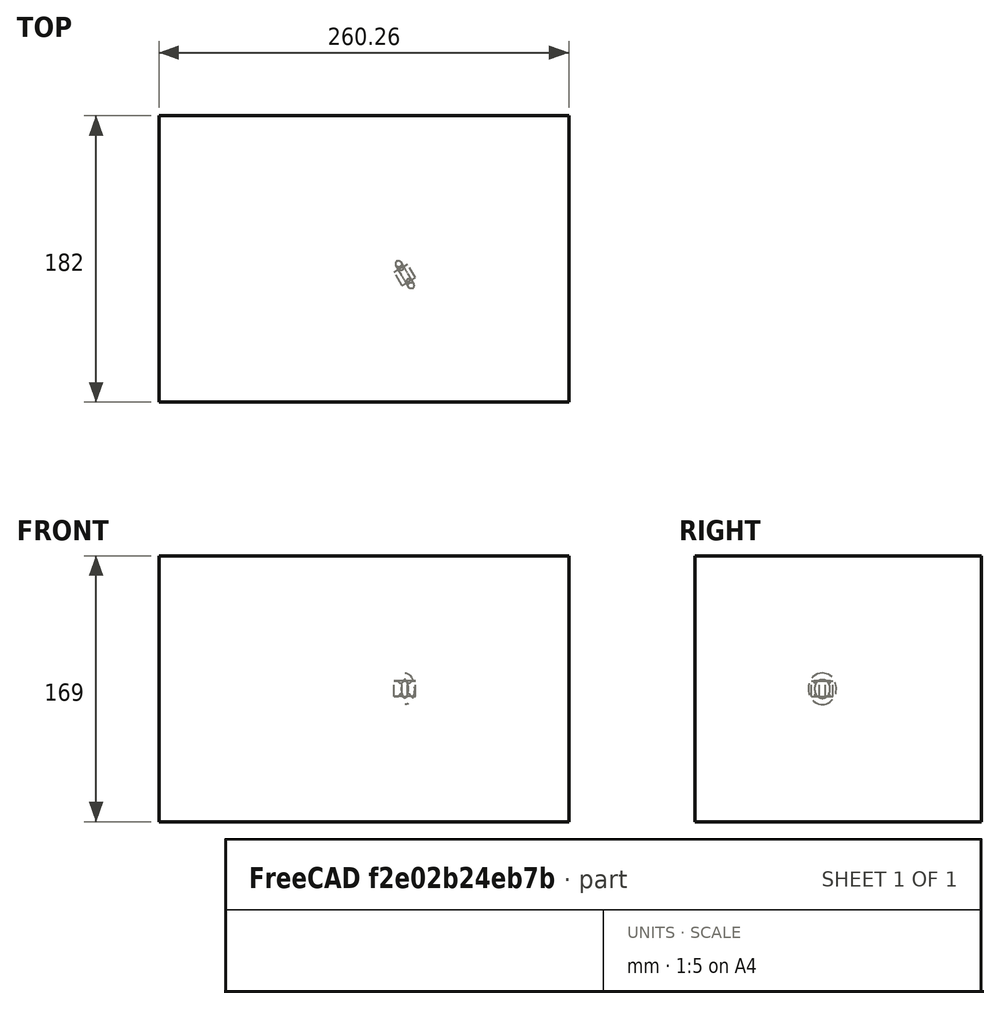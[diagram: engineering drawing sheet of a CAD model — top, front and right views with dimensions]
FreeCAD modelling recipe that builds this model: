
FCSTD DOCUMENT  (FreeCAD 1.0R39109 (Git))
Label: polarArray-7-Base-rotated-translated
License: All rights reserved
objects: App::DocumentObjectGroupPython×1251, Part::FeaturePython×4, App::Part×2, Part::MultiFuse×1
note: 4 computed .brp shape members not serialized (recipe doc carries the construction recipe); baked Part::Feature solids carry a one-line shape summary decoded from their .brp

FEATURE [App::DocumentObjectGroupPython] HALFPI  # scripted group (container) (typed FeaturePython)
  name = HALFPI
  value = pi/2.
FEATURE [App::DocumentObjectGroupPython] PI  # scripted group (container) (typed FeaturePython)
  name = PI
  value = 1.*pi
FEATURE [App::DocumentObjectGroupPython] TWOPI  # scripted group (container) (typed FeaturePython)
  name = TWOPI
  value = 2.*pi
FEATURE [App::DocumentObjectGroupPython] Constants  # scripted group (container) (typed FeaturePython)
  Group = -> [HALFPI,PI,TWOPI]
FEATURE [App::DocumentObjectGroupPython] Variables  # scripted group (container) (typed FeaturePython)
FEATURE [App::DocumentObjectGroupPython] Quantities  # scripted group (container) (typed FeaturePython)
FEATURE [App::DocumentObjectGroupPython] Isotopes  # scripted group (container) (typed FeaturePython)
FEATURE [App::DocumentObjectGroupPython] Elements  # scripted group (container) (typed FeaturePython)
FEATURE [App::DocumentObjectGroupPython] Matrix  # scripted group (container) (typed FeaturePython)
FEATURE [App::DocumentObjectGroupPython] Surfaces  # scripted group (container) (typed FeaturePython)
FEATURE [App::DocumentObjectGroupPython] Opticals  # scripted group (container) (typed FeaturePython)
  Group = -> [Matrix,Surfaces]
FEATURE [App::DocumentObjectGroupPython] G4Isotopes  # scripted group (container) (typed FeaturePython)
FEATURE [App::DocumentObjectGroupPython] H_element  # scripted group (container) (typed FeaturePython)
  Z = 1
  atom_value = 1.008
  formula = H
  name = H_element
FEATURE [App::DocumentObjectGroupPython] He_element  # scripted group (container) (typed FeaturePython)
  Z = 2
  atom_value = 4.0026
  formula = He
  name = He_element
FEATURE [App::DocumentObjectGroupPython] Li_element  # scripted group (container) (typed FeaturePython)
  Z = 3
  atom_value = 6.94
  formula = Li
  name = Li_element
FEATURE [App::DocumentObjectGroupPython] Be_element  # scripted group (container) (typed FeaturePython)
  Z = 4
  atom_value = 9.01218
  formula = Be
  name = Be_element
FEATURE [App::DocumentObjectGroupPython] B_element  # scripted group (container) (typed FeaturePython)
  Z = 5
  atom_value = 10.81
  formula = B
  name = B_element
FEATURE [App::DocumentObjectGroupPython] C_element  # scripted group (container) (typed FeaturePython)
  Z = 6
  atom_value = 12.011
  formula = C
  name = C_element
FEATURE [App::DocumentObjectGroupPython] N_element  # scripted group (container) (typed FeaturePython)
  Z = 7
  atom_value = 14.007
  formula = N
  name = N_element
FEATURE [App::DocumentObjectGroupPython] O_element  # scripted group (container) (typed FeaturePython)
  Z = 8
  atom_value = 15.999
  formula = O
  name = O_element
FEATURE [App::DocumentObjectGroupPython] F_element  # scripted group (container) (typed FeaturePython)
  Z = 9
  atom_value = 18.9984
  formula = F
  name = F_element
FEATURE [App::DocumentObjectGroupPython] Ne_element  # scripted group (container) (typed FeaturePython)
  Z = 10
  atom_value = 20.1797
  formula = Ne
  name = Ne_element
FEATURE [App::DocumentObjectGroupPython] Na_element  # scripted group (container) (typed FeaturePython)
  Z = 11
  atom_value = 22.9898
  formula = Na
  name = Na_element
FEATURE [App::DocumentObjectGroupPython] Mg_element  # scripted group (container) (typed FeaturePython)
  Z = 12
  atom_value = 24.305
  formula = Mg
  name = Mg_element
FEATURE [App::DocumentObjectGroupPython] Al_element  # scripted group (container) (typed FeaturePython)
  Z = 13
  atom_value = 26.9815
  formula = Al
  name = Al_element
FEATURE [App::DocumentObjectGroupPython] Si_element  # scripted group (container) (typed FeaturePython)
  Z = 14
  atom_value = 28.085
  formula = Si
  name = Si_element
FEATURE [App::DocumentObjectGroupPython] P_element  # scripted group (container) (typed FeaturePython)
  Z = 15
  atom_value = 30.9738
  formula = P
  name = P_element
FEATURE [App::DocumentObjectGroupPython] S_element  # scripted group (container) (typed FeaturePython)
  Z = 16
  atom_value = 32.06
  formula = S
  name = S_element
FEATURE [App::DocumentObjectGroupPython] Cl_element  # scripted group (container) (typed FeaturePython)
  Z = 17
  atom_value = 35.45
  formula = Cl
  name = Cl_element
FEATURE [App::DocumentObjectGroupPython] Ar_element  # scripted group (container) (typed FeaturePython)
  Z = 18
  atom_value = 39.95
  formula = Ar
  name = Ar_element
FEATURE [App::DocumentObjectGroupPython] K_element  # scripted group (container) (typed FeaturePython)
  Z = 19
  atom_value = 39.0983
  formula = K
  name = K_element
FEATURE [App::DocumentObjectGroupPython] Ca_element  # scripted group (container) (typed FeaturePython)
  Z = 20
  atom_value = 40.078
  formula = Ca
  name = Ca_element
FEATURE [App::DocumentObjectGroupPython] Sc_element  # scripted group (container) (typed FeaturePython)
  Z = 21
  atom_value = 44.9559
  formula = Sc
  name = Sc_element
FEATURE [App::DocumentObjectGroupPython] Ti_element  # scripted group (container) (typed FeaturePython)
  Z = 22
  atom_value = 47.867
  formula = Ti
  name = Ti_element
FEATURE [App::DocumentObjectGroupPython] V_element  # scripted group (container) (typed FeaturePython)
  Z = 23
  atom_value = 50.9415
  formula = V
  name = V_element
FEATURE [App::DocumentObjectGroupPython] Cr_element  # scripted group (container) (typed FeaturePython)
  Z = 24
  atom_value = 51.9961
  formula = Cr
  name = Cr_element
FEATURE [App::DocumentObjectGroupPython] Mn_element  # scripted group (container) (typed FeaturePython)
  Z = 25
  atom_value = 54.938
  formula = Mn
  name = Mn_element
FEATURE [App::DocumentObjectGroupPython] Fe_element  # scripted group (container) (typed FeaturePython)
  Z = 26
  atom_value = 55.845
  formula = Fe
  name = Fe_element
FEATURE [App::DocumentObjectGroupPython] Co_element  # scripted group (container) (typed FeaturePython)
  Z = 27
  atom_value = 58.9332
  formula = Co
  name = Co_element
FEATURE [App::DocumentObjectGroupPython] Ni_element  # scripted group (container) (typed FeaturePython)
  Z = 28
  atom_value = 58.6934
  formula = Ni
  name = Ni_element
FEATURE [App::DocumentObjectGroupPython] Cu_element  # scripted group (container) (typed FeaturePython)
  Z = 29
  atom_value = 63.546
  formula = Cu
  name = Cu_element
FEATURE [App::DocumentObjectGroupPython] Zn_element  # scripted group (container) (typed FeaturePython)
  Z = 30
  atom_value = 65.38
  formula = Zn
  name = Zn_element
FEATURE [App::DocumentObjectGroupPython] Ga_element  # scripted group (container) (typed FeaturePython)
  Z = 31
  atom_value = 69.723
  formula = Ga
  name = Ga_element
FEATURE [App::DocumentObjectGroupPython] Ge_element  # scripted group (container) (typed FeaturePython)
  Z = 32
  atom_value = 72.63
  formula = Ge
  name = Ge_element
FEATURE [App::DocumentObjectGroupPython] As_element  # scripted group (container) (typed FeaturePython)
  Z = 33
  atom_value = 74.9216
  formula = As
  name = As_element
FEATURE [App::DocumentObjectGroupPython] Se_element  # scripted group (container) (typed FeaturePython)
  Z = 34
  atom_value = 78.971
  formula = Se
  name = Se_element
FEATURE [App::DocumentObjectGroupPython] Br_element  # scripted group (container) (typed FeaturePython)
  Z = 35
  atom_value = 79.904
  formula = Br
  name = Br_element
FEATURE [App::DocumentObjectGroupPython] Kr_element  # scripted group (container) (typed FeaturePython)
  Z = 36
  atom_value = 83.798
  formula = Kr
  name = Kr_element
FEATURE [App::DocumentObjectGroupPython] Rb_element  # scripted group (container) (typed FeaturePython)
  Z = 37
  atom_value = 85.4678
  formula = Rb
  name = Rb_element
FEATURE [App::DocumentObjectGroupPython] Sr_element  # scripted group (container) (typed FeaturePython)
  Z = 38
  atom_value = 87.62
  formula = Sr
  name = Sr_element
FEATURE [App::DocumentObjectGroupPython] Y_element  # scripted group (container) (typed FeaturePython)
  Z = 39
  atom_value = 88.9058
  formula = Y
  name = Y_element
FEATURE [App::DocumentObjectGroupPython] Zr_element  # scripted group (container) (typed FeaturePython)
  Z = 40
  atom_value = 91.224
  formula = Zr
  name = Zr_element
FEATURE [App::DocumentObjectGroupPython] Nb_element  # scripted group (container) (typed FeaturePython)
  Z = 41
  atom_value = 92.9064
  formula = Nb
  name = Nb_element
FEATURE [App::DocumentObjectGroupPython] Mo_element  # scripted group (container) (typed FeaturePython)
  Z = 42
  atom_value = 95.95
  formula = Mo
  name = Mo_element
FEATURE [App::DocumentObjectGroupPython] Tc_element  # scripted group (container) (typed FeaturePython)
  Z = 43
  atom_value = 97
  formula = Tc
  name = Tc_element
FEATURE [App::DocumentObjectGroupPython] Ru_element  # scripted group (container) (typed FeaturePython)
  Z = 44
  atom_value = 101.07
  formula = Ru
  name = Ru_element
FEATURE [App::DocumentObjectGroupPython] Rh_element  # scripted group (container) (typed FeaturePython)
  Z = 45
  atom_value = 102.905
  formula = Rh
  name = Rh_element
FEATURE [App::DocumentObjectGroupPython] Pd_element  # scripted group (container) (typed FeaturePython)
  Z = 46
  atom_value = 106.42
  formula = Pd
  name = Pd_element
FEATURE [App::DocumentObjectGroupPython] Ag_element  # scripted group (container) (typed FeaturePython)
  Z = 47
  atom_value = 107.868
  formula = Ag
  name = Ag_element
FEATURE [App::DocumentObjectGroupPython] Cd_element  # scripted group (container) (typed FeaturePython)
  Z = 48
  atom_value = 112.414
  formula = Cd
  name = Cd_element
FEATURE [App::DocumentObjectGroupPython] In_element  # scripted group (container) (typed FeaturePython)
  Z = 49
  atom_value = 114.818
  formula = In
  name = In_element
FEATURE [App::DocumentObjectGroupPython] Sn_element  # scripted group (container) (typed FeaturePython)
  Z = 50
  atom_value = 118.71
  formula = Sn
  name = Sn_element
FEATURE [App::DocumentObjectGroupPython] Sb_element  # scripted group (container) (typed FeaturePython)
  Z = 51
  atom_value = 121.76
  formula = Sb
  name = Sb_element
FEATURE [App::DocumentObjectGroupPython] Te_element  # scripted group (container) (typed FeaturePython)
  Z = 52
  atom_value = 127.6
  formula = Te
  name = Te_element
FEATURE [App::DocumentObjectGroupPython] I_element  # scripted group (container) (typed FeaturePython)
  Z = 53
  atom_value = 126.904
  formula = I
  name = I_element
FEATURE [App::DocumentObjectGroupPython] Xe_element  # scripted group (container) (typed FeaturePython)
  Z = 54
  atom_value = 131.293
  formula = Xe
  name = Xe_element
FEATURE [App::DocumentObjectGroupPython] Cs_element  # scripted group (container) (typed FeaturePython)
  Z = 55
  atom_value = 132.905
  formula = Cs
  name = Cs_element
FEATURE [App::DocumentObjectGroupPython] Ba_element  # scripted group (container) (typed FeaturePython)
  Z = 56
  atom_value = 137.327
  formula = Ba
  name = Ba_element
FEATURE [App::DocumentObjectGroupPython] La_element  # scripted group (container) (typed FeaturePython)
  Z = 57
  atom_value = 138.905
  formula = La
  name = La_element
FEATURE [App::DocumentObjectGroupPython] Ce_element  # scripted group (container) (typed FeaturePython)
  Z = 58
  atom_value = 140.116
  formula = Ce
  name = Ce_element
FEATURE [App::DocumentObjectGroupPython] Pr_element  # scripted group (container) (typed FeaturePython)
  Z = 59
  atom_value = 140.908
  formula = Pr
  name = Pr_element
FEATURE [App::DocumentObjectGroupPython] Nd_element  # scripted group (container) (typed FeaturePython)
  Z = 60
  atom_value = 144.242
  formula = Nd
  name = Nd_element
FEATURE [App::DocumentObjectGroupPython] Pm_element  # scripted group (container) (typed FeaturePython)
  Z = 61
  atom_value = 145
  formula = Pm
  name = Pm_element
FEATURE [App::DocumentObjectGroupPython] Sm_element  # scripted group (container) (typed FeaturePython)
  Z = 62
  atom_value = 150.36
  formula = Sm
  name = Sm_element
FEATURE [App::DocumentObjectGroupPython] Eu_element  # scripted group (container) (typed FeaturePython)
  Z = 63
  atom_value = 151.964
  formula = Eu
  name = Eu_element
FEATURE [App::DocumentObjectGroupPython] Gd_element  # scripted group (container) (typed FeaturePython)
  Z = 64
  atom_value = 157.25
  formula = Gd
  name = Gd_element
FEATURE [App::DocumentObjectGroupPython] Tb_element  # scripted group (container) (typed FeaturePython)
  Z = 65
  atom_value = 158.925
  formula = Tb
  name = Tb_element
FEATURE [App::DocumentObjectGroupPython] Dy_element  # scripted group (container) (typed FeaturePython)
  Z = 66
  atom_value = 162.5
  formula = Dy
  name = Dy_element
FEATURE [App::DocumentObjectGroupPython] Ho_element  # scripted group (container) (typed FeaturePython)
  Z = 67
  atom_value = 164.93
  formula = Ho
  name = Ho_element
FEATURE [App::DocumentObjectGroupPython] Er_element  # scripted group (container) (typed FeaturePython)
  Z = 68
  atom_value = 167.259
  formula = Er
  name = Er_element
FEATURE [App::DocumentObjectGroupPython] Tm_element  # scripted group (container) (typed FeaturePython)
  Z = 69
  atom_value = 168.934
  formula = Tm
  name = Tm_element
FEATURE [App::DocumentObjectGroupPython] Yb_element  # scripted group (container) (typed FeaturePython)
  Z = 70
  atom_value = 173.045
  formula = Yb
  name = Yb_element
FEATURE [App::DocumentObjectGroupPython] Lu_element  # scripted group (container) (typed FeaturePython)
  Z = 71
  atom_value = 174.967
  formula = Lu
  name = Lu_element
FEATURE [App::DocumentObjectGroupPython] Hf_element  # scripted group (container) (typed FeaturePython)
  Z = 72
  atom_value = 178.49
  formula = Hf
  name = Hf_element
FEATURE [App::DocumentObjectGroupPython] Ta_element  # scripted group (container) (typed FeaturePython)
  Z = 73
  atom_value = 180.948
  formula = Ta
  name = Ta_element
FEATURE [App::DocumentObjectGroupPython] W_element  # scripted group (container) (typed FeaturePython)
  Z = 74
  atom_value = 183.84
  formula = W
  name = W_element
FEATURE [App::DocumentObjectGroupPython] Re_element  # scripted group (container) (typed FeaturePython)
  Z = 75
  atom_value = 186.207
  formula = Re
  name = Re_element
FEATURE [App::DocumentObjectGroupPython] Os_element  # scripted group (container) (typed FeaturePython)
  Z = 76
  atom_value = 190.23
  formula = Os
  name = Os_element
FEATURE [App::DocumentObjectGroupPython] Ir_element  # scripted group (container) (typed FeaturePython)
  Z = 77
  atom_value = 192.217
  formula = Ir
  name = Ir_element
FEATURE [App::DocumentObjectGroupPython] Pt_element  # scripted group (container) (typed FeaturePython)
  Z = 78
  atom_value = 195.084
  formula = Pt
  name = Pt_element
FEATURE [App::DocumentObjectGroupPython] Au_element  # scripted group (container) (typed FeaturePython)
  Z = 79
  atom_value = 196.967
  formula = Au
  name = Au_element
FEATURE [App::DocumentObjectGroupPython] Hg_element  # scripted group (container) (typed FeaturePython)
  Z = 80
  atom_value = 200.592
  formula = Hg
  name = Hg_element
FEATURE [App::DocumentObjectGroupPython] Tl_element  # scripted group (container) (typed FeaturePython)
  Z = 81
  atom_value = 204.38
  formula = Tl
  name = Tl_element
FEATURE [App::DocumentObjectGroupPython] Pb_element  # scripted group (container) (typed FeaturePython)
  Z = 82
  atom_value = 207.2
  formula = Pb
  name = Pb_element
FEATURE [App::DocumentObjectGroupPython] Bi_element  # scripted group (container) (typed FeaturePython)
  Z = 83
  atom_value = 208.98
  formula = Bi
  name = Bi_element
FEATURE [App::DocumentObjectGroupPython] Po_element  # scripted group (container) (typed FeaturePython)
  Z = 84
  atom_value = 209
  formula = Po
  name = Po_element
FEATURE [App::DocumentObjectGroupPython] At_element  # scripted group (container) (typed FeaturePython)
  Z = 85
  atom_value = 210
  formula = At
  name = At_element
FEATURE [App::DocumentObjectGroupPython] Rn_element  # scripted group (container) (typed FeaturePython)
  Z = 86
  atom_value = 222
  formula = Rn
  name = Rn_element
FEATURE [App::DocumentObjectGroupPython] Fr_element  # scripted group (container) (typed FeaturePython)
  Z = 87
  atom_value = 223
  formula = Fr
  name = Fr_element
FEATURE [App::DocumentObjectGroupPython] Ra_element  # scripted group (container) (typed FeaturePython)
  Z = 88
  atom_value = 226
  formula = Ra
  name = Ra_element
FEATURE [App::DocumentObjectGroupPython] Ac_element  # scripted group (container) (typed FeaturePython)
  Z = 89
  atom_value = 227
  formula = Ac
  name = Ac_element
FEATURE [App::DocumentObjectGroupPython] Th_element  # scripted group (container) (typed FeaturePython)
  Z = 90
  atom_value = 232.038
  formula = Th
  name = Th_element
FEATURE [App::DocumentObjectGroupPython] Pa_element  # scripted group (container) (typed FeaturePython)
  Z = 91
  atom_value = 231.036
  formula = Pa
  name = Pa_element
FEATURE [App::DocumentObjectGroupPython] U_element  # scripted group (container) (typed FeaturePython)
  Z = 92
  atom_value = 238.029
  formula = U
  name = U_element
FEATURE [App::DocumentObjectGroupPython] Np_element  # scripted group (container) (typed FeaturePython)
  Z = 93
  atom_value = 237
  formula = Np
  name = Np_element
FEATURE [App::DocumentObjectGroupPython] Pu_element  # scripted group (container) (typed FeaturePython)
  Z = 94
  atom_value = 244
  formula = Pu
  name = Pu_element
FEATURE [App::DocumentObjectGroupPython] Am_element  # scripted group (container) (typed FeaturePython)
  Z = 95
  atom_value = 243
  formula = Am
  name = Am_element
FEATURE [App::DocumentObjectGroupPython] Cm_element  # scripted group (container) (typed FeaturePython)
  Z = 96
  atom_value = 247
  formula = Cm
  name = Cm_element
FEATURE [App::DocumentObjectGroupPython] Bk_element  # scripted group (container) (typed FeaturePython)
  Z = 97
  atom_value = 247
  formula = Bk
  name = Bk_element
FEATURE [App::DocumentObjectGroupPython] Cf_element  # scripted group (container) (typed FeaturePython)
  Z = 98
  atom_value = 251
  formula = Cf
  name = Cf_element
FEATURE [App::DocumentObjectGroupPython] G4Elements  # scripted group (container) (typed FeaturePython)
  Group = -> [H_element,He_element,Li_element,Be_element,B_element,C_element,N_element,O_element,F_element,Ne_element,Na_element,Mg_element,Al_element,Si_element,P_element,S_element,Cl_element,Ar_element,K_element,Ca_element,Sc_element,Ti_element,V_element,Cr_element,Mn_element,Fe_element,Co_element,Ni_element,Cu_element,Zn_element,Ga_element,Ge_element,As_element,Se_element,Br_element,Kr_element,Rb_element,+61 more]
FEATURE [App::DocumentObjectGroupPython] H_element001  label="H_element : 0.101"  # scripted group (container) (typed FeaturePython)
  n = 0.101327
FEATURE [App::DocumentObjectGroupPython] C_element001  label="C_element : 0.775"  # scripted group (container) (typed FeaturePython)
  n = 0.7755
FEATURE [App::DocumentObjectGroupPython] N_element001  label="N_element : 0.035"  # scripted group (container) (typed FeaturePython)
  n = 0.035057
FEATURE [App::DocumentObjectGroupPython] O_element001  label="O_element : 0.052"  # scripted group (container) (typed FeaturePython)
  n = 0.0523159
FEATURE [App::DocumentObjectGroupPython] F_element001  label="F_element : 0.017"  # scripted group (container) (typed FeaturePython)
  n = 0.017422
FEATURE [App::DocumentObjectGroupPython] Ca_element001  label="Ca_element : 0.018"  # scripted group (container) (typed FeaturePython)
  n = 0.018378
FEATURE [App::DocumentObjectGroupPython] G4_A_150_TISSUE  label="G4_A-150_TISSUE"  # scripted group (container) (typed FeaturePython)
  Dunit = g/cm3
  Dvalue = 1.127
  Group = -> [H_element001,C_element001,N_element001,O_element001,F_element001,Ca_element001]
  conduct = 2
  density = 1
  expand = 3
  formula = G4_A-150_TISSUE
  name = G4_A-150_TISSUE
  specific = 4
FEATURE [App::DocumentObjectGroupPython] C_element002  label="C_element : 3"  # scripted group (container) (typed FeaturePython)
  n = 3
  ref = C_element
FEATURE [App::DocumentObjectGroupPython] H_element002  label="H_element : 6"  # scripted group (container) (typed FeaturePython)
  n = 6
  ref = H_element
FEATURE [App::DocumentObjectGroupPython] O_element002  label="O_element : 1"  # scripted group (container) (typed FeaturePython)
  n = 1
  ref = O_element
FEATURE [App::DocumentObjectGroupPython] G4_ACETONE  # scripted group (container) (typed FeaturePython)
  Dunit = g/cm3
  Dvalue = 0.7899
  Group = -> [C_element002,H_element002,O_element002]
  conduct = 2
  density = 1
  expand = 3
  formula = G4_ACETONE
  name = G4_ACETONE
  specific = 4
FEATURE [App::DocumentObjectGroupPython] C_element003  label="C_element : 2"  # scripted group (container) (typed FeaturePython)
  n = 2
  ref = C_element
FEATURE [App::DocumentObjectGroupPython] H_element003  label="H_element : 2"  # scripted group (container) (typed FeaturePython)
  n = 2
  ref = H_element
FEATURE [App::DocumentObjectGroupPython] G4_ACETYLENE  # scripted group (container) (typed FeaturePython)
  Dunit = g/cm3
  Dvalue = 0.0010967
  Group = -> [C_element003,H_element003]
  conduct = 2
  density = 1
  expand = 3
  formula = G4_ACETYLENE
  name = G4_ACETYLENE
  specific = 4
FEATURE [App::DocumentObjectGroupPython] C_element004  label="C_element : 5"  # scripted group (container) (typed FeaturePython)
  n = 5
  ref = C_element
FEATURE [App::DocumentObjectGroupPython] H_element004  label="H_element : 5"  # scripted group (container) (typed FeaturePython)
  n = 5
  ref = H_element
FEATURE [App::DocumentObjectGroupPython] N_element002  label="N_element : 5"  # scripted group (container) (typed FeaturePython)
  n = 5
  ref = N_element
FEATURE [App::DocumentObjectGroupPython] G4_ADENINE  # scripted group (container) (typed FeaturePython)
  Dunit = g/cm3
  Dvalue = 1.6
  Group = -> [C_element004,H_element004,N_element002]
  conduct = 2
  density = 1
  expand = 3
  formula = G4_ADENINE
  name = G4_ADENINE
  specific = 4
FEATURE [App::DocumentObjectGroupPython] H_element005  label="H_element : 0.114"  # scripted group (container) (typed FeaturePython)
  n = 0.114
FEATURE [App::DocumentObjectGroupPython] C_element005  label="C_element : 0.598"  # scripted group (container) (typed FeaturePython)
  n = 0.598
FEATURE [App::DocumentObjectGroupPython] N_element003  label="N_element : 0.007"  # scripted group (container) (typed FeaturePython)
  n = 0.007
FEATURE [App::DocumentObjectGroupPython] O_element003  label="O_element : 0.278"  # scripted group (container) (typed FeaturePython)
  n = 0.278
FEATURE [App::DocumentObjectGroupPython] Na_element001  label="Na_element : 0.001"  # scripted group (container) (typed FeaturePython)
  n = 0.001
FEATURE [App::DocumentObjectGroupPython] S_element001  label="S_element : 0.001"  # scripted group (container) (typed FeaturePython)
  n = 0.001
FEATURE [App::DocumentObjectGroupPython] Cl_element001  label="Cl_element : 0.001"  # scripted group (container) (typed FeaturePython)
  n = 0.001
FEATURE [App::DocumentObjectGroupPython] G4_ADIPOSE_TISSUE_ICRP  # scripted group (container) (typed FeaturePython)
  Dunit = g/cm3
  Dvalue = 0.95
  Group = -> [H_element005,C_element005,N_element003,O_element003,Na_element001,S_element001,Cl_element001]
  conduct = 2
  density = 1
  expand = 3
  formula = G4_ADIPOSE_TISSUE_ICRP
  name = G4_ADIPOSE_TISSUE_ICRP
  specific = 4
FEATURE [App::DocumentObjectGroupPython] C_element006  label="C_element : 0.000"  # scripted group (container) (typed FeaturePython)
  n = 0.000124
FEATURE [App::DocumentObjectGroupPython] N_element004  label="N_element : 0.755"  # scripted group (container) (typed FeaturePython)
  n = 0.755268
FEATURE [App::DocumentObjectGroupPython] O_element004  label="O_element : 0.232"  # scripted group (container) (typed FeaturePython)
  n = 0.231781
FEATURE [App::DocumentObjectGroupPython] Ar_element001  label="Ar_element : 0.013"  # scripted group (container) (typed FeaturePython)
  n = 0.012827
FEATURE [App::DocumentObjectGroupPython] G4_AIR  # scripted group (container) (typed FeaturePython)
  Dunit = g/cm3
  Dvalue = 0.00120479
  Group = -> [C_element006,N_element004,O_element004,Ar_element001]
  conduct = 2
  density = 1
  expand = 3
  formula = G4_AIR
  name = G4_AIR
  specific = 4
FEATURE [App::DocumentObjectGroupPython] C_element007  label="C_element : 006"  # scripted group (container) (typed FeaturePython)
  n = 3
  ref = C_element
FEATURE [App::DocumentObjectGroupPython] H_element006  label="H_element : 7"  # scripted group (container) (typed FeaturePython)
  n = 7
  ref = H_element
FEATURE [App::DocumentObjectGroupPython] N_element005  label="N_element : 1"  # scripted group (container) (typed FeaturePython)
  n = 1
  ref = N_element
FEATURE [App::DocumentObjectGroupPython] O_element005  label="O_element : 2"  # scripted group (container) (typed FeaturePython)
  n = 2
  ref = O_element
FEATURE [App::DocumentObjectGroupPython] G4_ALANINE  # scripted group (container) (typed FeaturePython)
  Dunit = g/cm3
  Dvalue = 1.42
  Group = -> [C_element007,H_element006,N_element005,O_element005]
  conduct = 2
  density = 1
  expand = 3
  formula = G4_ALANINE
  name = G4_ALANINE
  specific = 4
FEATURE [App::DocumentObjectGroupPython] Al_element001  label="Al_element : 2"  # scripted group (container) (typed FeaturePython)
  n = 2
  ref = Al_element
FEATURE [App::DocumentObjectGroupPython] O_element006  label="O_element : 3"  # scripted group (container) (typed FeaturePython)
  n = 3
  ref = O_element
FEATURE [App::DocumentObjectGroupPython] G4_ALUMINUM_OXIDE  # scripted group (container) (typed FeaturePython)
  Dunit = g/cm3
  Dvalue = 3.97
  Group = -> [Al_element001,O_element006]
  conduct = 2
  density = 1
  expand = 3
  formula = G4_ALUMINUM_OXIDE
  name = G4_ALUMINUM_OXIDE
  specific = 4
FEATURE [App::DocumentObjectGroupPython] H_element007  label="H_element : 0.106"  # scripted group (container) (typed FeaturePython)
  n = 0.10593
FEATURE [App::DocumentObjectGroupPython] C_element008  label="C_element : 0.789"  # scripted group (container) (typed FeaturePython)
  n = 0.788974
FEATURE [App::DocumentObjectGroupPython] O_element007  label="O_element : 0.105"  # scripted group (container) (typed FeaturePython)
  n = 0.105096
FEATURE [App::DocumentObjectGroupPython] G4_AMBER  # scripted group (container) (typed FeaturePython)
  Dunit = g/cm3
  Dvalue = 1.1
  Group = -> [H_element007,C_element008,O_element007]
  conduct = 2
  density = 1
  expand = 3
  formula = G4_AMBER
  name = G4_AMBER
  specific = 4
FEATURE [App::DocumentObjectGroupPython] N_element006  label="N_element : 006"  # scripted group (container) (typed FeaturePython)
  n = 1
  ref = N_element
FEATURE [App::DocumentObjectGroupPython] H_element008  label="H_element : 3"  # scripted group (container) (typed FeaturePython)
  n = 3
  ref = H_element
FEATURE [App::DocumentObjectGroupPython] G4_AMMONIA  # scripted group (container) (typed FeaturePython)
  Dunit = g/cm3
  Dvalue = 0.000826019
  Group = -> [N_element006,H_element008]
  conduct = 2
  density = 1
  expand = 3
  formula = G4_AMMONIA
  name = G4_AMMONIA
  specific = 4
FEATURE [App::DocumentObjectGroupPython] C_element009  label="C_element : 6"  # scripted group (container) (typed FeaturePython)
  n = 6
  ref = C_element
FEATURE [App::DocumentObjectGroupPython] H_element009  label="H_element : 008"  # scripted group (container) (typed FeaturePython)
  n = 7
  ref = H_element
FEATURE [App::DocumentObjectGroupPython] N_element007  label="N_element : 007"  # scripted group (container) (typed FeaturePython)
  n = 1
  ref = N_element
FEATURE [App::DocumentObjectGroupPython] G4_ANILINE  # scripted group (container) (typed FeaturePython)
  Dunit = g/cm3
  Dvalue = 1.0235
  Group = -> [C_element009,H_element009,N_element007]
  conduct = 2
  density = 1
  expand = 3
  formula = G4_ANILINE
  name = G4_ANILINE
  specific = 4
FEATURE [App::DocumentObjectGroupPython] C_element010  label="C_element : 14"  # scripted group (container) (typed FeaturePython)
  n = 14
  ref = C_element
FEATURE [App::DocumentObjectGroupPython] H_element010  label="H_element : 10"  # scripted group (container) (typed FeaturePython)
  n = 10
  ref = H_element
FEATURE [App::DocumentObjectGroupPython] G4_ANTHRACENE  # scripted group (container) (typed FeaturePython)
  Dunit = g/cm3
  Dvalue = 1.283
  Group = -> [C_element010,H_element010]
  conduct = 2
  density = 1
  expand = 3
  formula = G4_ANTHRACENE
  name = G4_ANTHRACENE
  specific = 4
FEATURE [App::DocumentObjectGroupPython] H_element011  label="H_element : 0.065"  # scripted group (container) (typed FeaturePython)
  n = 0.0654709
FEATURE [App::DocumentObjectGroupPython] C_element011  label="C_element : 0.537"  # scripted group (container) (typed FeaturePython)
  n = 0.536944
FEATURE [App::DocumentObjectGroupPython] N_element008  label="N_element : 0.021"  # scripted group (container) (typed FeaturePython)
  n = 0.0215
FEATURE [App::DocumentObjectGroupPython] O_element008  label="O_element : 0.032"  # scripted group (container) (typed FeaturePython)
  n = 0.032085
FEATURE [App::DocumentObjectGroupPython] F_element002  label="F_element : 0.167"  # scripted group (container) (typed FeaturePython)
  n = 0.167411
FEATURE [App::DocumentObjectGroupPython] Ca_element002  label="Ca_element : 0.177"  # scripted group (container) (typed FeaturePython)
  n = 0.176589
FEATURE [App::DocumentObjectGroupPython] G4_B_100_BONE  label="G4_B-100_BONE"  # scripted group (container) (typed FeaturePython)
  Dunit = g/cm3
  Dvalue = 1.45
  Group = -> [H_element011,C_element011,N_element008,O_element008,F_element002,Ca_element002]
  conduct = 2
  density = 1
  expand = 3
  formula = G4_B-100_BONE
  name = G4_B-100_BONE
  specific = 4
FEATURE [App::DocumentObjectGroupPython] H_element012  label="H_element : 0.057"  # scripted group (container) (typed FeaturePython)
  n = 0.057441
FEATURE [App::DocumentObjectGroupPython] C_element012  label="C_element : 0.790"  # scripted group (container) (typed FeaturePython)
  n = 0.774591
FEATURE [App::DocumentObjectGroupPython] O_element009  label="O_element : 0.168"  # scripted group (container) (typed FeaturePython)
  n = 0.167968
FEATURE [App::DocumentObjectGroupPython] G4_BAKELITE  # scripted group (container) (typed FeaturePython)
  Dunit = g/cm3
  Dvalue = 1.25
  Group = -> [H_element012,C_element012,O_element009]
  conduct = 2
  density = 1
  expand = 3
  formula = G4_BAKELITE
  name = G4_BAKELITE
  specific = 4
FEATURE [App::DocumentObjectGroupPython] Ba_element001  label="Ba_element : 1"  # scripted group (container) (typed FeaturePython)
  n = 1
  ref = Ba_element
FEATURE [App::DocumentObjectGroupPython] F_element003  label="F_element : 2"  # scripted group (container) (typed FeaturePython)
  n = 2
  ref = F_element
FEATURE [App::DocumentObjectGroupPython] G4_BARIUM_FLUORIDE  # scripted group (container) (typed FeaturePython)
  Dunit = g/cm3
  Dvalue = 4.89
  Group = -> [Ba_element001,F_element003]
  conduct = 2
  density = 1
  expand = 3
  formula = G4_BARIUM_FLUORIDE
  name = G4_BARIUM_FLUORIDE
  specific = 4
FEATURE [App::DocumentObjectGroupPython] Ba_element002  label="Ba_element : 002"  # scripted group (container) (typed FeaturePython)
  n = 1
  ref = Ba_element
FEATURE [App::DocumentObjectGroupPython] S_element002  label="S_element : 1"  # scripted group (container) (typed FeaturePython)
  n = 1
  ref = S_element
FEATURE [App::DocumentObjectGroupPython] O_element010  label="O_element : 4"  # scripted group (container) (typed FeaturePython)
  n = 4
  ref = O_element
FEATURE [App::DocumentObjectGroupPython] G4_BARIUM_SULFATE  # scripted group (container) (typed FeaturePython)
  Dunit = g/cm3
  Dvalue = 4.5
  Group = -> [Ba_element002,S_element002,O_element010]
  conduct = 2
  density = 1
  expand = 3
  formula = G4_BARIUM_SULFATE
  name = G4_BARIUM_SULFATE
  specific = 4
FEATURE [App::DocumentObjectGroupPython] C_element013  label="C_element : 007"  # scripted group (container) (typed FeaturePython)
  n = 6
  ref = C_element
FEATURE [App::DocumentObjectGroupPython] H_element013  label="H_element : 009"  # scripted group (container) (typed FeaturePython)
  n = 6
  ref = H_element
FEATURE [App::DocumentObjectGroupPython] G4_BENZENE  # scripted group (container) (typed FeaturePython)
  Dunit = g/cm3
  Dvalue = 0.87865
  Group = -> [C_element013,H_element013]
  conduct = 2
  density = 1
  expand = 3
  formula = G4_BENZENE
  name = G4_BENZENE
  specific = 4
FEATURE [App::DocumentObjectGroupPython] Be_element001  label="Be_element : 1"  # scripted group (container) (typed FeaturePython)
  n = 1
  ref = Be_element
FEATURE [App::DocumentObjectGroupPython] O_element011  label="O_element : 005"  # scripted group (container) (typed FeaturePython)
  n = 1
  ref = O_element
FEATURE [App::DocumentObjectGroupPython] G4_BERYLLIUM_OXIDE  # scripted group (container) (typed FeaturePython)
  Dunit = g/cm3
  Dvalue = 3.01
  Group = -> [Be_element001,O_element011]
  conduct = 2
  density = 1
  expand = 3
  formula = G4_BERYLLIUM_OXIDE
  name = G4_BERYLLIUM_OXIDE
  specific = 4
FEATURE [App::DocumentObjectGroupPython] Bi_element001  label="Bi_element : 4"  # scripted group (container) (typed FeaturePython)
  n = 4
  ref = Bi_element
FEATURE [App::DocumentObjectGroupPython] Ge_element001  label="Ge_element : 3"  # scripted group (container) (typed FeaturePython)
  n = 3
  ref = Ge_element
FEATURE [App::DocumentObjectGroupPython] O_element012  label="O_element : 12"  # scripted group (container) (typed FeaturePython)
  n = 12
  ref = O_element
FEATURE [App::DocumentObjectGroupPython] G4_BGO  # scripted group (container) (typed FeaturePython)
  Dunit = g/cm3
  Dvalue = 7.13
  Group = -> [Bi_element001,Ge_element001,O_element012]
  conduct = 2
  density = 1
  expand = 3
  formula = G4_BGO
  name = G4_BGO
  specific = 4
FEATURE [App::DocumentObjectGroupPython] H_element014  label="H_element : 0.102"  # scripted group (container) (typed FeaturePython)
  n = 0.102
FEATURE [App::DocumentObjectGroupPython] C_element014  label="C_element : 0.110"  # scripted group (container) (typed FeaturePython)
  n = 0.11
FEATURE [App::DocumentObjectGroupPython] N_element009  label="N_element : 0.033"  # scripted group (container) (typed FeaturePython)
  n = 0.033
FEATURE [App::DocumentObjectGroupPython] O_element013  label="O_element : 0.745"  # scripted group (container) (typed FeaturePython)
  n = 0.745
FEATURE [App::DocumentObjectGroupPython] Na_element002  label="Na_element : 0.002"  # scripted group (container) (typed FeaturePython)
  n = 0.001
FEATURE [App::DocumentObjectGroupPython] P_element001  label="P_element : 0.001"  # scripted group (container) (typed FeaturePython)
  n = 0.001
FEATURE [App::DocumentObjectGroupPython] S_element003  label="S_element : 0.002"  # scripted group (container) (typed FeaturePython)
  n = 0.002
FEATURE [App::DocumentObjectGroupPython] Cl_element002  label="Cl_element : 0.003"  # scripted group (container) (typed FeaturePython)
  n = 0.003
FEATURE [App::DocumentObjectGroupPython] K_element001  label="K_element : 0.002"  # scripted group (container) (typed FeaturePython)
  n = 0.002
FEATURE [App::DocumentObjectGroupPython] Fe_element001  label="Fe_element : 0.001"  # scripted group (container) (typed FeaturePython)
  n = 0.001
FEATURE [App::DocumentObjectGroupPython] G4_BLOOD_ICRP  # scripted group (container) (typed FeaturePython)
  Dunit = g/cm3
  Dvalue = 1.06
  Group = -> [H_element014,C_element014,N_element009,O_element013,Na_element002,P_element001,S_element003,Cl_element002,K_element001,Fe_element001]
  conduct = 2
  density = 1
  expand = 3
  formula = G4_BLOOD_ICRP
  name = G4_BLOOD_ICRP
  specific = 4
FEATURE [App::DocumentObjectGroupPython] H_element015  label="H_element : 0.064"  # scripted group (container) (typed FeaturePython)
  n = 0.064
FEATURE [App::DocumentObjectGroupPython] C_element015  label="C_element : 0.278"  # scripted group (container) (typed FeaturePython)
  n = 0.278
FEATURE [App::DocumentObjectGroupPython] N_element010  label="N_element : 0.027"  # scripted group (container) (typed FeaturePython)
  n = 0.027
FEATURE [App::DocumentObjectGroupPython] O_element014  label="O_element : 0.410"  # scripted group (container) (typed FeaturePython)
  n = 0.41
FEATURE [App::DocumentObjectGroupPython] Mg_element001  label="Mg_element : 0.002"  # scripted group (container) (typed FeaturePython)
  n = 0.002
FEATURE [App::DocumentObjectGroupPython] P_element002  label="P_element : 0.070"  # scripted group (container) (typed FeaturePython)
  n = 0.07
FEATURE [App::DocumentObjectGroupPython] S_element004  label="S_element : 0.003"  # scripted group (container) (typed FeaturePython)
  n = 0.002
FEATURE [App::DocumentObjectGroupPython] Ca_element003  label="Ca_element : 0.147"  # scripted group (container) (typed FeaturePython)
  n = 0.147
FEATURE [App::DocumentObjectGroupPython] G4_BONE_COMPACT_ICRU  # scripted group (container) (typed FeaturePython)
  Dunit = g/cm3
  Dvalue = 1.85
  Group = -> [H_element015,C_element015,N_element010,O_element014,Mg_element001,P_element002,S_element004,Ca_element003]
  conduct = 2
  density = 1
  expand = 3
  formula = G4_BONE_COMPACT_ICRU
  name = G4_BONE_COMPACT_ICRU
  specific = 4
FEATURE [App::DocumentObjectGroupPython] H_element016  label="H_element : 0.034"  # scripted group (container) (typed FeaturePython)
  n = 0.034
FEATURE [App::DocumentObjectGroupPython] C_element016  label="C_element : 0.155"  # scripted group (container) (typed FeaturePython)
  n = 0.155
FEATURE [App::DocumentObjectGroupPython] N_element011  label="N_element : 0.042"  # scripted group (container) (typed FeaturePython)
  n = 0.042
FEATURE [App::DocumentObjectGroupPython] O_element015  label="O_element : 0.435"  # scripted group (container) (typed FeaturePython)
  n = 0.435
FEATURE [App::DocumentObjectGroupPython] Na_element003  label="Na_element : 0.003"  # scripted group (container) (typed FeaturePython)
  n = 0.001
FEATURE [App::DocumentObjectGroupPython] Mg_element002  label="Mg_element : 0.003"  # scripted group (container) (typed FeaturePython)
  n = 0.002
FEATURE [App::DocumentObjectGroupPython] P_element003  label="P_element : 0.103"  # scripted group (container) (typed FeaturePython)
  n = 0.103
FEATURE [App::DocumentObjectGroupPython] S_element005  label="S_element : 0.004"  # scripted group (container) (typed FeaturePython)
  n = 0.003
FEATURE [App::DocumentObjectGroupPython] Ca_element004  label="Ca_element : 0.225"  # scripted group (container) (typed FeaturePython)
  n = 0.225
FEATURE [App::DocumentObjectGroupPython] G4_BONE_CORTICAL_ICRP  # scripted group (container) (typed FeaturePython)
  Dunit = g/cm3
  Dvalue = 1.92
  Group = -> [H_element016,C_element016,N_element011,O_element015,Na_element003,Mg_element002,P_element003,S_element005,Ca_element004]
  conduct = 2
  density = 1
  expand = 3
  formula = G4_BONE_CORTICAL_ICRP
  name = G4_BONE_CORTICAL_ICRP
  specific = 4
FEATURE [App::DocumentObjectGroupPython] B_element001  label="B_element : 4"  # scripted group (container) (typed FeaturePython)
  n = 4
  ref = B_element
FEATURE [App::DocumentObjectGroupPython] C_element017  label="C_element : 1"  # scripted group (container) (typed FeaturePython)
  n = 1
  ref = C_element
FEATURE [App::DocumentObjectGroupPython] G4_BORON_CARBIDE  # scripted group (container) (typed FeaturePython)
  Dunit = g/cm3
  Dvalue = 2.52
  Group = -> [B_element001,C_element017]
  conduct = 2
  density = 1
  expand = 3
  formula = G4_BORON_CARBIDE
  name = G4_BORON_CARBIDE
  specific = 4
FEATURE [App::DocumentObjectGroupPython] B_element002  label="B_element : 2"  # scripted group (container) (typed FeaturePython)
  n = 2
  ref = B_element
FEATURE [App::DocumentObjectGroupPython] O_element016  label="O_element : 006"  # scripted group (container) (typed FeaturePython)
  n = 3
  ref = O_element
FEATURE [App::DocumentObjectGroupPython] G4_BORON_OXIDE  # scripted group (container) (typed FeaturePython)
  Dunit = g/cm3
  Dvalue = 1.812
  Group = -> [B_element002,O_element016]
  conduct = 2
  density = 1
  expand = 3
  formula = G4_BORON_OXIDE
  name = G4_BORON_OXIDE
  specific = 4
FEATURE [App::DocumentObjectGroupPython] H_element017  label="H_element : 0.107"  # scripted group (container) (typed FeaturePython)
  n = 0.107
FEATURE [App::DocumentObjectGroupPython] C_element018  label="C_element : 0.145"  # scripted group (container) (typed FeaturePython)
  n = 0.145
FEATURE [App::DocumentObjectGroupPython] N_element012  label="N_element : 0.022"  # scripted group (container) (typed FeaturePython)
  n = 0.022
FEATURE [App::DocumentObjectGroupPython] O_element017  label="O_element : 0.712"  # scripted group (container) (typed FeaturePython)
  n = 0.712
FEATURE [App::DocumentObjectGroupPython] Na_element004  label="Na_element : 0.004"  # scripted group (container) (typed FeaturePython)
  n = 0.002
FEATURE [App::DocumentObjectGroupPython] P_element004  label="P_element : 0.004"  # scripted group (container) (typed FeaturePython)
  n = 0.004
FEATURE [App::DocumentObjectGroupPython] S_element006  label="S_element : 0.005"  # scripted group (container) (typed FeaturePython)
  n = 0.002
FEATURE [App::DocumentObjectGroupPython] Cl_element003  label="Cl_element : 0.004"  # scripted group (container) (typed FeaturePython)
  n = 0.003
FEATURE [App::DocumentObjectGroupPython] K_element002  label="K_element : 0.003"  # scripted group (container) (typed FeaturePython)
  n = 0.003
FEATURE [App::DocumentObjectGroupPython] G4_BRAIN_ICRP  # scripted group (container) (typed FeaturePython)
  Dunit = g/cm3
  Dvalue = 1.04
  Group = -> [H_element017,C_element018,N_element012,O_element017,Na_element004,P_element004,S_element006,Cl_element003,K_element002]
  conduct = 2
  density = 1
  expand = 3
  formula = G4_BRAIN_ICRP
  name = G4_BRAIN_ICRP
  specific = 4
FEATURE [App::DocumentObjectGroupPython] C_element019  label="C_element : 4"  # scripted group (container) (typed FeaturePython)
  n = 4
  ref = C_element
FEATURE [App::DocumentObjectGroupPython] H_element018  label="H_element : 010"  # scripted group (container) (typed FeaturePython)
  n = 10
  ref = H_element
FEATURE [App::DocumentObjectGroupPython] G4_BUTANE  # scripted group (container) (typed FeaturePython)
  Dunit = g/cm3
  Dvalue = 0.00249343
  Group = -> [C_element019,H_element018]
  conduct = 2
  density = 1
  expand = 3
  formula = G4_BUTANE
  name = G4_BUTANE
  specific = 4
FEATURE [App::DocumentObjectGroupPython] C_element020  label="C_element : 008"  # scripted group (container) (typed FeaturePython)
  n = 4
  ref = C_element
FEATURE [App::DocumentObjectGroupPython] H_element019  label="H_element : 011"  # scripted group (container) (typed FeaturePython)
  n = 10
  ref = H_element
FEATURE [App::DocumentObjectGroupPython] O_element018  label="O_element : 007"  # scripted group (container) (typed FeaturePython)
  n = 1
  ref = O_element
FEATURE [App::DocumentObjectGroupPython] G4_N_BUTYL_ALCOHOL  label="G4_N-BUTYL_ALCOHOL"  # scripted group (container) (typed FeaturePython)
  Dunit = g/cm3
  Dvalue = 0.8098
  Group = -> [C_element020,H_element019,O_element018]
  conduct = 2
  density = 1
  expand = 3
  formula = G4_N-BUTYL_ALCOHOL
  name = G4_N-BUTYL_ALCOHOL
  specific = 4
FEATURE [App::DocumentObjectGroupPython] H_element020  label="H_element : 0.025"  # scripted group (container) (typed FeaturePython)
  n = 0.02468
FEATURE [App::DocumentObjectGroupPython] C_element021  label="C_element : 0.502"  # scripted group (container) (typed FeaturePython)
  n = 0.501611
FEATURE [App::DocumentObjectGroupPython] O_element019  label="O_element : 0.005"  # scripted group (container) (typed FeaturePython)
  n = 0.004527
FEATURE [App::DocumentObjectGroupPython] F_element004  label="F_element : 0.465"  # scripted group (container) (typed FeaturePython)
  n = 0.465209
FEATURE [App::DocumentObjectGroupPython] Si_element001  label="Si_element : 0.004"  # scripted group (container) (typed FeaturePython)
  n = 0.003973
FEATURE [App::DocumentObjectGroupPython] G4_C_552  label="G4_C-552"  # scripted group (container) (typed FeaturePython)
  Dunit = g/cm3
  Dvalue = 1.76
  Group = -> [H_element020,C_element021,O_element019,F_element004,Si_element001]
  conduct = 2
  density = 1
  expand = 3
  formula = G4_C-552
  name = G4_C-552
  specific = 4
FEATURE [App::DocumentObjectGroupPython] Cd_element001  label="Cd_element : 1"  # scripted group (container) (typed FeaturePython)
  n = 1
  ref = Cd_element
FEATURE [App::DocumentObjectGroupPython] Te_element001  label="Te_element : 1"  # scripted group (container) (typed FeaturePython)
  n = 1
  ref = Te_element
FEATURE [App::DocumentObjectGroupPython] G4_CADMIUM_TELLURIDE  # scripted group (container) (typed FeaturePython)
  Dunit = g/cm3
  Dvalue = 6.2
  Group = -> [Cd_element001,Te_element001]
  conduct = 2
  density = 1
  expand = 3
  formula = G4_CADMIUM_TELLURIDE
  name = G4_CADMIUM_TELLURIDE
  specific = 4
FEATURE [App::DocumentObjectGroupPython] Cd_element002  label="Cd_element : 002"  # scripted group (container) (typed FeaturePython)
  n = 1
  ref = Cd_element
FEATURE [App::DocumentObjectGroupPython] W_element001  label="W_element : 1"  # scripted group (container) (typed FeaturePython)
  n = 1
  ref = W_element
FEATURE [App::DocumentObjectGroupPython] O_element020  label="O_element : 008"  # scripted group (container) (typed FeaturePython)
  n = 4
  ref = O_element
FEATURE [App::DocumentObjectGroupPython] G4_CADMIUM_TUNGSTATE  # scripted group (container) (typed FeaturePython)
  Dunit = g/cm3
  Dvalue = 7.9
  Group = -> [Cd_element002,W_element001,O_element020]
  conduct = 2
  density = 1
  expand = 3
  formula = G4_CADMIUM_TUNGSTATE
  name = G4_CADMIUM_TUNGSTATE
  specific = 4
FEATURE [App::DocumentObjectGroupPython] Ca_element005  label="Ca_element : 1"  # scripted group (container) (typed FeaturePython)
  n = 1
  ref = Ca_element
FEATURE [App::DocumentObjectGroupPython] C_element022  label="C_element : 009"  # scripted group (container) (typed FeaturePython)
  n = 1
  ref = C_element
FEATURE [App::DocumentObjectGroupPython] O_element021  label="O_element : 009"  # scripted group (container) (typed FeaturePython)
  n = 3
  ref = O_element
FEATURE [App::DocumentObjectGroupPython] G4_CALCIUM_CARBONATE  # scripted group (container) (typed FeaturePython)
  Dunit = g/cm3
  Dvalue = 2.8
  Group = -> [Ca_element005,C_element022,O_element021]
  conduct = 2
  density = 1
  expand = 3
  formula = G4_CALCIUM_CARBONATE
  name = G4_CALCIUM_CARBONATE
  specific = 4
FEATURE [App::DocumentObjectGroupPython] Ca_element006  label="Ca_element : 002"  # scripted group (container) (typed FeaturePython)
  n = 1
  ref = Ca_element
FEATURE [App::DocumentObjectGroupPython] F_element005  label="F_element : 003"  # scripted group (container) (typed FeaturePython)
  n = 2
  ref = F_element
FEATURE [App::DocumentObjectGroupPython] G4_CALCIUM_FLUORIDE  # scripted group (container) (typed FeaturePython)
  Dunit = g/cm3
  Dvalue = 3.18
  Group = -> [Ca_element006,F_element005]
  conduct = 2
  density = 1
  expand = 3
  formula = G4_CALCIUM_FLUORIDE
  name = G4_CALCIUM_FLUORIDE
  specific = 4
FEATURE [App::DocumentObjectGroupPython] Ca_element007  label="Ca_element : 003"  # scripted group (container) (typed FeaturePython)
  n = 1
  ref = Ca_element
FEATURE [App::DocumentObjectGroupPython] O_element022  label="O_element : 010"  # scripted group (container) (typed FeaturePython)
  n = 1
  ref = O_element
FEATURE [App::DocumentObjectGroupPython] G4_CALCIUM_OXIDE  # scripted group (container) (typed FeaturePython)
  Dunit = g/cm3
  Dvalue = 3.3
  Group = -> [Ca_element007,O_element022]
  conduct = 2
  density = 1
  expand = 3
  formula = G4_CALCIUM_OXIDE
  name = G4_CALCIUM_OXIDE
  specific = 4
FEATURE [App::DocumentObjectGroupPython] Ca_element008  label="Ca_element : 004"  # scripted group (container) (typed FeaturePython)
  n = 1
  ref = Ca_element
FEATURE [App::DocumentObjectGroupPython] S_element007  label="S_element : 002"  # scripted group (container) (typed FeaturePython)
  n = 1
  ref = S_element
FEATURE [App::DocumentObjectGroupPython] O_element023  label="O_element : 011"  # scripted group (container) (typed FeaturePython)
  n = 4
  ref = O_element
FEATURE [App::DocumentObjectGroupPython] G4_CALCIUM_SULFATE  # scripted group (container) (typed FeaturePython)
  Dunit = g/cm3
  Dvalue = 2.96
  Group = -> [Ca_element008,S_element007,O_element023]
  conduct = 2
  density = 1
  expand = 3
  formula = G4_CALCIUM_SULFATE
  name = G4_CALCIUM_SULFATE
  specific = 4
FEATURE [App::DocumentObjectGroupPython] Ca_element009  label="Ca_element : 005"  # scripted group (container) (typed FeaturePython)
  n = 1
  ref = Ca_element
FEATURE [App::DocumentObjectGroupPython] W_element002  label="W_element : 002"  # scripted group (container) (typed FeaturePython)
  n = 1
  ref = W_element
FEATURE [App::DocumentObjectGroupPython] O_element024  label="O_element : 012"  # scripted group (container) (typed FeaturePython)
  n = 4
  ref = O_element
FEATURE [App::DocumentObjectGroupPython] G4_CALCIUM_TUNGSTATE  # scripted group (container) (typed FeaturePython)
  Dunit = g/cm3
  Dvalue = 6.062
  Group = -> [Ca_element009,W_element002,O_element024]
  conduct = 2
  density = 1
  expand = 3
  formula = G4_CALCIUM_TUNGSTATE
  name = G4_CALCIUM_TUNGSTATE
  specific = 4
FEATURE [App::DocumentObjectGroupPython] C_element023  label="C_element : 010"  # scripted group (container) (typed FeaturePython)
  n = 1
  ref = C_element
FEATURE [App::DocumentObjectGroupPython] O_element025  label="O_element : 013"  # scripted group (container) (typed FeaturePython)
  n = 2
  ref = O_element
FEATURE [App::DocumentObjectGroupPython] G4_CARBON_DIOXIDE  # scripted group (container) (typed FeaturePython)
  Dunit = g/cm3
  Dvalue = 0.00184212
  Group = -> [C_element023,O_element025]
  conduct = 2
  density = 1
  expand = 3
  formula = G4_CARBON_DIOXIDE
  name = G4_CARBON_DIOXIDE
  specific = 4
FEATURE [App::DocumentObjectGroupPython] C_element024  label="C_element : 011"  # scripted group (container) (typed FeaturePython)
  n = 1
  ref = C_element
FEATURE [App::DocumentObjectGroupPython] Cl_element004  label="Cl_element : 4"  # scripted group (container) (typed FeaturePython)
  n = 4
  ref = Cl_element
FEATURE [App::DocumentObjectGroupPython] G4_CARBON_TETRACHLORIDE  # scripted group (container) (typed FeaturePython)
  Dunit = g/cm3
  Dvalue = 1.594
  Group = -> [C_element024,Cl_element004]
  conduct = 2
  density = 1
  expand = 3
  formula = G4_CARBON_TETRACHLORIDE
  name = G4_CARBON_TETRACHLORIDE
  specific = 4
FEATURE [App::DocumentObjectGroupPython] C_element025  label="C_element : 012"  # scripted group (container) (typed FeaturePython)
  n = 6
  ref = C_element
FEATURE [App::DocumentObjectGroupPython] H_element021  label="H_element : 012"  # scripted group (container) (typed FeaturePython)
  n = 10
  ref = H_element
FEATURE [App::DocumentObjectGroupPython] O_element026  label="O_element : 5"  # scripted group (container) (typed FeaturePython)
  n = 5
  ref = O_element
FEATURE [App::DocumentObjectGroupPython] G4_CELLULOSE_CELLOPHANE  # scripted group (container) (typed FeaturePython)
  Dunit = g/cm3
  Dvalue = 1.42
  Group = -> [C_element025,H_element021,O_element026]
  conduct = 2
  density = 1
  expand = 3
  formula = G4_CELLULOSE_CELLOPHANE
  name = G4_CELLULOSE_CELLOPHANE
  specific = 4
FEATURE [App::DocumentObjectGroupPython] H_element022  label="H_element : 0.067"  # scripted group (container) (typed FeaturePython)
  n = 0.067125
FEATURE [App::DocumentObjectGroupPython] C_element026  label="C_element : 0.545"  # scripted group (container) (typed FeaturePython)
  n = 0.545403
FEATURE [App::DocumentObjectGroupPython] O_element027  label="O_element : 0.387"  # scripted group (container) (typed FeaturePython)
  n = 0.387472
FEATURE [App::DocumentObjectGroupPython] G4_CELLULOSE_BUTYRATE  # scripted group (container) (typed FeaturePython)
  Dunit = g/cm3
  Dvalue = 1.2
  Group = -> [H_element022,C_element026,O_element027]
  conduct = 2
  density = 1
  expand = 3
  formula = G4_CELLULOSE_BUTYRATE
  name = G4_CELLULOSE_BUTYRATE
  specific = 4
FEATURE [App::DocumentObjectGroupPython] H_element023  label="H_element : 0.029"  # scripted group (container) (typed FeaturePython)
  n = 0.029216
FEATURE [App::DocumentObjectGroupPython] C_element027  label="C_element : 0.271"  # scripted group (container) (typed FeaturePython)
  n = 0.271296
FEATURE [App::DocumentObjectGroupPython] N_element013  label="N_element : 0.121"  # scripted group (container) (typed FeaturePython)
  n = 0.121276
FEATURE [App::DocumentObjectGroupPython] O_element028  label="O_element : 0.578"  # scripted group (container) (typed FeaturePython)
  n = 0.578212
FEATURE [App::DocumentObjectGroupPython] G4_CELLULOSE_NITRATE  # scripted group (container) (typed FeaturePython)
  Dunit = g/cm3
  Dvalue = 1.49
  Group = -> [H_element023,C_element027,N_element013,O_element028]
  conduct = 2
  density = 1
  expand = 3
  formula = G4_CELLULOSE_NITRATE
  name = G4_CELLULOSE_NITRATE
  specific = 4
FEATURE [App::DocumentObjectGroupPython] H_element024  label="H_element : 0.108"  # scripted group (container) (typed FeaturePython)
  n = 0.107596
FEATURE [App::DocumentObjectGroupPython] N_element014  label="N_element : 0.001"  # scripted group (container) (typed FeaturePython)
  n = 0.0008
FEATURE [App::DocumentObjectGroupPython] O_element029  label="O_element : 0.875"  # scripted group (container) (typed FeaturePython)
  n = 0.874976
FEATURE [App::DocumentObjectGroupPython] S_element008  label="S_element : 0.015"  # scripted group (container) (typed FeaturePython)
  n = 0.014627
FEATURE [App::DocumentObjectGroupPython] Ce_element001  label="Ce_element : 0.002"  # scripted group (container) (typed FeaturePython)
  n = 0.002001
FEATURE [App::DocumentObjectGroupPython] G4_CERIC_SULFATE  # scripted group (container) (typed FeaturePython)
  Dunit = g/cm3
  Dvalue = 1.03
  Group = -> [H_element024,N_element014,O_element029,S_element008,Ce_element001]
  conduct = 2
  density = 1
  expand = 3
  formula = G4_CERIC_SULFATE
  name = G4_CERIC_SULFATE
  specific = 4
FEATURE [App::DocumentObjectGroupPython] Cs_element001  label="Cs_element : 1"  # scripted group (container) (typed FeaturePython)
  n = 1
  ref = Cs_element
FEATURE [App::DocumentObjectGroupPython] F_element006  label="F_element : 1"  # scripted group (container) (typed FeaturePython)
  n = 1
  ref = F_element
FEATURE [App::DocumentObjectGroupPython] G4_CESIUM_FLUORIDE  # scripted group (container) (typed FeaturePython)
  Dunit = g/cm3
  Dvalue = 4.115
  Group = -> [Cs_element001,F_element006]
  conduct = 2
  density = 1
  expand = 3
  formula = G4_CESIUM_FLUORIDE
  name = G4_CESIUM_FLUORIDE
  specific = 4
FEATURE [App::DocumentObjectGroupPython] Cs_element002  label="Cs_element : 002"  # scripted group (container) (typed FeaturePython)
  n = 1
  ref = Cs_element
FEATURE [App::DocumentObjectGroupPython] I_element001  label="I_element : 1"  # scripted group (container) (typed FeaturePython)
  n = 1
  ref = I_element
FEATURE [App::DocumentObjectGroupPython] G4_CESIUM_IODIDE  # scripted group (container) (typed FeaturePython)
  Dunit = g/cm3
  Dvalue = 4.51
  Group = -> [Cs_element002,I_element001]
  conduct = 2
  density = 1
  expand = 3
  formula = G4_CESIUM_IODIDE
  name = G4_CESIUM_IODIDE
  specific = 4
FEATURE [App::DocumentObjectGroupPython] C_element028  label="C_element : 013"  # scripted group (container) (typed FeaturePython)
  n = 6
  ref = C_element
FEATURE [App::DocumentObjectGroupPython] H_element025  label="H_element : 013"  # scripted group (container) (typed FeaturePython)
  n = 5
  ref = H_element
FEATURE [App::DocumentObjectGroupPython] Cl_element005  label="Cl_element : 1"  # scripted group (container) (typed FeaturePython)
  n = 1
  ref = Cl_element
FEATURE [App::DocumentObjectGroupPython] G4_CHLOROBENZENE  # scripted group (container) (typed FeaturePython)
  Dunit = g/cm3
  Dvalue = 1.1058
  Group = -> [C_element028,H_element025,Cl_element005]
  conduct = 2
  density = 1
  expand = 3
  formula = G4_CHLOROBENZENE
  name = G4_CHLOROBENZENE
  specific = 4
FEATURE [App::DocumentObjectGroupPython] C_element029  label="C_element : 014"  # scripted group (container) (typed FeaturePython)
  n = 1
  ref = C_element
FEATURE [App::DocumentObjectGroupPython] H_element026  label="H_element : 1"  # scripted group (container) (typed FeaturePython)
  n = 1
  ref = H_element
FEATURE [App::DocumentObjectGroupPython] Cl_element006  label="Cl_element : 3"  # scripted group (container) (typed FeaturePython)
  n = 3
  ref = Cl_element
FEATURE [App::DocumentObjectGroupPython] G4_CHLOROFORM  # scripted group (container) (typed FeaturePython)
  Dunit = g/cm3
  Dvalue = 1.4832
  Group = -> [C_element029,H_element026,Cl_element006]
  conduct = 2
  density = 1
  expand = 3
  formula = G4_CHLOROFORM
  name = G4_CHLOROFORM
  specific = 4
FEATURE [App::DocumentObjectGroupPython] H_element027  label="H_element : 0.010"  # scripted group (container) (typed FeaturePython)
  n = 0.01
FEATURE [App::DocumentObjectGroupPython] C_element030  label="C_element : 0.001"  # scripted group (container) (typed FeaturePython)
  n = 0.001
FEATURE [App::DocumentObjectGroupPython] O_element030  label="O_element : 0.529"  # scripted group (container) (typed FeaturePython)
  n = 0.529107
FEATURE [App::DocumentObjectGroupPython] Na_element005  label="Na_element : 0.016"  # scripted group (container) (typed FeaturePython)
  n = 0.016
FEATURE [App::DocumentObjectGroupPython] Mg_element003  label="Mg_element : 0.004"  # scripted group (container) (typed FeaturePython)
  n = 0.002
FEATURE [App::DocumentObjectGroupPython] Al_element002  label="Al_element : 0.034"  # scripted group (container) (typed FeaturePython)
  n = 0.033872
FEATURE [App::DocumentObjectGroupPython] Si_element002  label="Si_element : 0.337"  # scripted group (container) (typed FeaturePython)
  n = 0.337021
FEATURE [App::DocumentObjectGroupPython] K_element003  label="K_element : 0.013"  # scripted group (container) (typed FeaturePython)
  n = 0.013
FEATURE [App::DocumentObjectGroupPython] Ca_element010  label="Ca_element : 0.044"  # scripted group (container) (typed FeaturePython)
  n = 0.044
FEATURE [App::DocumentObjectGroupPython] Fe_element002  label="Fe_element : 0.014"  # scripted group (container) (typed FeaturePython)
  n = 0.014
FEATURE [App::DocumentObjectGroupPython] G4_CONCRETE  # scripted group (container) (typed FeaturePython)
  Dunit = g/cm3
  Dvalue = 2.3
  Group = -> [H_element027,C_element030,O_element030,Na_element005,Mg_element003,Al_element002,Si_element002,K_element003,Ca_element010,Fe_element002]
  conduct = 2
  density = 1
  expand = 3
  formula = G4_CONCRETE
  name = G4_CONCRETE
  specific = 4
FEATURE [App::DocumentObjectGroupPython] C_element031  label="C_element : 015"  # scripted group (container) (typed FeaturePython)
  n = 6
  ref = C_element
FEATURE [App::DocumentObjectGroupPython] H_element028  label="H_element : 12"  # scripted group (container) (typed FeaturePython)
  n = 12
  ref = H_element
FEATURE [App::DocumentObjectGroupPython] G4_CYCLOHEXANE  # scripted group (container) (typed FeaturePython)
  Dunit = g/cm3
  Dvalue = 0.779
  Group = -> [C_element031,H_element028]
  conduct = 2
  density = 1
  expand = 3
  formula = G4_CYCLOHEXANE
  name = G4_CYCLOHEXANE
  specific = 4
FEATURE [App::DocumentObjectGroupPython] C_element032  label="C_element : 016"  # scripted group (container) (typed FeaturePython)
  n = 6
  ref = C_element
FEATURE [App::DocumentObjectGroupPython] H_element029  label="H_element : 4"  # scripted group (container) (typed FeaturePython)
  n = 4
  ref = H_element
FEATURE [App::DocumentObjectGroupPython] Cl_element007  label="Cl_element : 2"  # scripted group (container) (typed FeaturePython)
  n = 2
  ref = Cl_element
FEATURE [App::DocumentObjectGroupPython] G4_1_2_DICHLOROBENZENE  label="G4_1.2-DICHLOROBENZENE"  # scripted group (container) (typed FeaturePython)
  Dunit = g/cm3
  Dvalue = 1.3048
  Group = -> [C_element032,H_element029,Cl_element007]
  conduct = 2
  density = 1
  expand = 3
  formula = G4_1.2-DICHLOROBENZENE
  name = G4_1.2-DICHLOROBENZENE
  specific = 4
FEATURE [App::DocumentObjectGroupPython] C_element033  label="C_element : 017"  # scripted group (container) (typed FeaturePython)
  n = 4
  ref = C_element
FEATURE [App::DocumentObjectGroupPython] H_element030  label="H_element : 8"  # scripted group (container) (typed FeaturePython)
  n = 8
  ref = H_element
FEATURE [App::DocumentObjectGroupPython] O_element031  label="O_element : 014"  # scripted group (container) (typed FeaturePython)
  n = 1
  ref = O_element
FEATURE [App::DocumentObjectGroupPython] Cl_element008  label="Cl_element : 005"  # scripted group (container) (typed FeaturePython)
  n = 2
  ref = Cl_element
FEATURE [App::DocumentObjectGroupPython] G4_DICHLORODIETHYL_ETHER  # scripted group (container) (typed FeaturePython)
  Dunit = g/cm3
  Dvalue = 1.2199
  Group = -> [C_element033,H_element030,O_element031,Cl_element008]
  conduct = 2
  density = 1
  expand = 3
  formula = G4_DICHLORODIETHYL_ETHER
  name = G4_DICHLORODIETHYL_ETHER
  specific = 4
FEATURE [App::DocumentObjectGroupPython] C_element034  label="C_element : 018"  # scripted group (container) (typed FeaturePython)
  n = 2
  ref = C_element
FEATURE [App::DocumentObjectGroupPython] H_element031  label="H_element : 014"  # scripted group (container) (typed FeaturePython)
  n = 4
  ref = H_element
FEATURE [App::DocumentObjectGroupPython] Cl_element009  label="Cl_element : 006"  # scripted group (container) (typed FeaturePython)
  n = 2
  ref = Cl_element
FEATURE [App::DocumentObjectGroupPython] G4_1_2_DICHLOROETHANE  label="G4_1.2-DICHLOROETHANE"  # scripted group (container) (typed FeaturePython)
  Dunit = g/cm3
  Dvalue = 1.2351
  Group = -> [C_element034,H_element031,Cl_element009]
  conduct = 2
  density = 1
  expand = 3
  formula = G4_1.2-DICHLOROETHANE
  name = G4_1.2-DICHLOROETHANE
  specific = 4
FEATURE [App::DocumentObjectGroupPython] C_element035  label="C_element : 019"  # scripted group (container) (typed FeaturePython)
  n = 4
  ref = C_element
FEATURE [App::DocumentObjectGroupPython] H_element032  label="H_element : 015"  # scripted group (container) (typed FeaturePython)
  n = 10
  ref = H_element
FEATURE [App::DocumentObjectGroupPython] O_element032  label="O_element : 015"  # scripted group (container) (typed FeaturePython)
  n = 1
  ref = O_element
FEATURE [App::DocumentObjectGroupPython] G4_DIETHYL_ETHER  # scripted group (container) (typed FeaturePython)
  Dunit = g/cm3
  Dvalue = 0.71378
  Group = -> [C_element035,H_element032,O_element032]
  conduct = 2
  density = 1
  expand = 3
  formula = G4_DIETHYL_ETHER
  name = G4_DIETHYL_ETHER
  specific = 4
FEATURE [App::DocumentObjectGroupPython] C_element036  label="C_element : 020"  # scripted group (container) (typed FeaturePython)
  n = 3
  ref = C_element
FEATURE [App::DocumentObjectGroupPython] H_element033  label="H_element : 016"  # scripted group (container) (typed FeaturePython)
  n = 7
  ref = H_element
FEATURE [App::DocumentObjectGroupPython] N_element015  label="N_element : 008"  # scripted group (container) (typed FeaturePython)
  n = 1
  ref = N_element
FEATURE [App::DocumentObjectGroupPython] O_element033  label="O_element : 016"  # scripted group (container) (typed FeaturePython)
  n = 1
  ref = O_element
FEATURE [App::DocumentObjectGroupPython] G4_N_N_DIMETHYL_FORMAMIDE  label="G4_N.N-DIMETHYL_FORMAMIDE"  # scripted group (container) (typed FeaturePython)
  Dunit = g/cm3
  Dvalue = 0.9487
  Group = -> [C_element036,H_element033,N_element015,O_element033]
  conduct = 2
  density = 1
  expand = 3
  formula = G4_N.N-DIMETHYL_FORMAMIDE
  name = G4_N.N-DIMETHYL_FORMAMIDE
  specific = 4
FEATURE [App::DocumentObjectGroupPython] C_element037  label="C_element : 021"  # scripted group (container) (typed FeaturePython)
  n = 2
  ref = C_element
FEATURE [App::DocumentObjectGroupPython] H_element034  label="H_element : 017"  # scripted group (container) (typed FeaturePython)
  n = 6
  ref = H_element
FEATURE [App::DocumentObjectGroupPython] O_element034  label="O_element : 017"  # scripted group (container) (typed FeaturePython)
  n = 1
  ref = O_element
FEATURE [App::DocumentObjectGroupPython] S_element009  label="S_element : 003"  # scripted group (container) (typed FeaturePython)
  n = 1
  ref = S_element
FEATURE [App::DocumentObjectGroupPython] G4_DIMETHYL_SULFOXIDE  # scripted group (container) (typed FeaturePython)
  Dunit = g/cm3
  Dvalue = 1.1014
  Group = -> [C_element037,H_element034,O_element034,S_element009]
  conduct = 2
  density = 1
  expand = 3
  formula = G4_DIMETHYL_SULFOXIDE
  name = G4_DIMETHYL_SULFOXIDE
  specific = 4
FEATURE [App::DocumentObjectGroupPython] C_element038  label="C_element : 022"  # scripted group (container) (typed FeaturePython)
  n = 2
  ref = C_element
FEATURE [App::DocumentObjectGroupPython] H_element035  label="H_element : 018"  # scripted group (container) (typed FeaturePython)
  n = 6
  ref = H_element
FEATURE [App::DocumentObjectGroupPython] G4_ETHANE  # scripted group (container) (typed FeaturePython)
  Dunit = g/cm3
  Dvalue = 0.00125324
  Group = -> [C_element038,H_element035]
  conduct = 2
  density = 1
  expand = 3
  formula = G4_ETHANE
  name = G4_ETHANE
  specific = 4
FEATURE [App::DocumentObjectGroupPython] C_element039  label="C_element : 023"  # scripted group (container) (typed FeaturePython)
  n = 2
  ref = C_element
FEATURE [App::DocumentObjectGroupPython] H_element036  label="H_element : 019"  # scripted group (container) (typed FeaturePython)
  n = 6
  ref = H_element
FEATURE [App::DocumentObjectGroupPython] O_element035  label="O_element : 018"  # scripted group (container) (typed FeaturePython)
  n = 1
  ref = O_element
FEATURE [App::DocumentObjectGroupPython] G4_ETHYL_ALCOHOL  # scripted group (container) (typed FeaturePython)
  Dunit = g/cm3
  Dvalue = 0.7893
  Group = -> [C_element039,H_element036,O_element035]
  conduct = 2
  density = 1
  expand = 3
  formula = G4_ETHYL_ALCOHOL
  name = G4_ETHYL_ALCOHOL
  specific = 4
FEATURE [App::DocumentObjectGroupPython] H_element037  label="H_element : 0.090"  # scripted group (container) (typed FeaturePython)
  n = 0.090027
FEATURE [App::DocumentObjectGroupPython] C_element040  label="C_element : 0.585"  # scripted group (container) (typed FeaturePython)
  n = 0.585182
FEATURE [App::DocumentObjectGroupPython] O_element036  label="O_element : 0.325"  # scripted group (container) (typed FeaturePython)
  n = 0.324791
FEATURE [App::DocumentObjectGroupPython] G4_ETHYL_CELLULOSE  # scripted group (container) (typed FeaturePython)
  Dunit = g/cm3
  Dvalue = 1.13
  Group = -> [H_element037,C_element040,O_element036]
  conduct = 2
  density = 1
  expand = 3
  formula = G4_ETHYL_CELLULOSE
  name = G4_ETHYL_CELLULOSE
  specific = 4
FEATURE [App::DocumentObjectGroupPython] C_element041  label="C_element : 024"  # scripted group (container) (typed FeaturePython)
  n = 2
  ref = C_element
FEATURE [App::DocumentObjectGroupPython] H_element038  label="H_element : 020"  # scripted group (container) (typed FeaturePython)
  n = 4
  ref = H_element
FEATURE [App::DocumentObjectGroupPython] G4_ETHYLENE  # scripted group (container) (typed FeaturePython)
  Dunit = g/cm3
  Dvalue = 0.00117497
  Group = -> [C_element041,H_element038]
  conduct = 2
  density = 1
  expand = 3
  formula = G4_ETHYLENE
  name = G4_ETHYLENE
  specific = 4
FEATURE [App::DocumentObjectGroupPython] H_element039  label="H_element : 0.096"  # scripted group (container) (typed FeaturePython)
  n = 0.096
FEATURE [App::DocumentObjectGroupPython] C_element042  label="C_element : 0.195"  # scripted group (container) (typed FeaturePython)
  n = 0.195
FEATURE [App::DocumentObjectGroupPython] N_element016  label="N_element : 0.057"  # scripted group (container) (typed FeaturePython)
  n = 0.057
FEATURE [App::DocumentObjectGroupPython] O_element037  label="O_element : 0.646"  # scripted group (container) (typed FeaturePython)
  n = 0.646
FEATURE [App::DocumentObjectGroupPython] Na_element006  label="Na_element : 0.017"  # scripted group (container) (typed FeaturePython)
  n = 0.001
FEATURE [App::DocumentObjectGroupPython] P_element005  label="P_element : 0.104"  # scripted group (container) (typed FeaturePython)
  n = 0.001
FEATURE [App::DocumentObjectGroupPython] S_element010  label="S_element : 0.016"  # scripted group (container) (typed FeaturePython)
  n = 0.003
FEATURE [App::DocumentObjectGroupPython] Cl_element010  label="Cl_element : 0.005"  # scripted group (container) (typed FeaturePython)
  n = 0.001
FEATURE [App::DocumentObjectGroupPython] G4_EYE_LENS_ICRP  # scripted group (container) (typed FeaturePython)
  Dunit = g/cm3
  Dvalue = 1.07
  Group = -> [H_element039,C_element042,N_element016,O_element037,Na_element006,P_element005,S_element010,Cl_element010]
  conduct = 2
  density = 1
  expand = 3
  formula = G4_EYE_LENS_ICRP
  name = G4_EYE_LENS_ICRP
  specific = 4
FEATURE [App::DocumentObjectGroupPython] Fe_element003  label="Fe_element : 2"  # scripted group (container) (typed FeaturePython)
  n = 2
  ref = Fe_element
FEATURE [App::DocumentObjectGroupPython] O_element038  label="O_element : 019"  # scripted group (container) (typed FeaturePython)
  n = 3
  ref = O_element
FEATURE [App::DocumentObjectGroupPython] G4_FERRIC_OXIDE  # scripted group (container) (typed FeaturePython)
  Dunit = g/cm3
  Dvalue = 5.2
  Group = -> [Fe_element003,O_element038]
  conduct = 2
  density = 1
  expand = 3
  formula = G4_FERRIC_OXIDE
  name = G4_FERRIC_OXIDE
  specific = 4
FEATURE [App::DocumentObjectGroupPython] Fe_element004  label="Fe_element : 1"  # scripted group (container) (typed FeaturePython)
  n = 1
  ref = Fe_element
FEATURE [App::DocumentObjectGroupPython] B_element003  label="B_element : 1"  # scripted group (container) (typed FeaturePython)
  n = 1
  ref = B_element
FEATURE [App::DocumentObjectGroupPython] G4_FERROBORIDE  # scripted group (container) (typed FeaturePython)
  Dunit = g/cm3
  Dvalue = 7.15
  Group = -> [Fe_element004,B_element003]
  conduct = 2
  density = 1
  expand = 3
  formula = G4_FERROBORIDE
  name = G4_FERROBORIDE
  specific = 4
FEATURE [App::DocumentObjectGroupPython] Fe_element005  label="Fe_element : 003"  # scripted group (container) (typed FeaturePython)
  n = 1
  ref = Fe_element
FEATURE [App::DocumentObjectGroupPython] O_element039  label="O_element : 020"  # scripted group (container) (typed FeaturePython)
  n = 1
  ref = O_element
FEATURE [App::DocumentObjectGroupPython] G4_FERROUS_OXIDE  # scripted group (container) (typed FeaturePython)
  Dunit = g/cm3
  Dvalue = 5.7
  Group = -> [Fe_element005,O_element039]
  conduct = 2
  density = 1
  expand = 3
  formula = G4_FERROUS_OXIDE
  name = G4_FERROUS_OXIDE
  specific = 4
FEATURE [App::DocumentObjectGroupPython] H_element040  label="H_element : 0.115"  # scripted group (container) (typed FeaturePython)
  n = 0.108259
FEATURE [App::DocumentObjectGroupPython] N_element017  label="N_element : 0.000"  # scripted group (container) (typed FeaturePython)
  n = 2.7e-05
FEATURE [App::DocumentObjectGroupPython] O_element040  label="O_element : 0.879"  # scripted group (container) (typed FeaturePython)
  n = 0.878636
FEATURE [App::DocumentObjectGroupPython] Na_element007  label="Na_element : 0.000"  # scripted group (container) (typed FeaturePython)
  n = 2.2e-05
FEATURE [App::DocumentObjectGroupPython] S_element011  label="S_element : 0.013"  # scripted group (container) (typed FeaturePython)
  n = 0.012968
FEATURE [App::DocumentObjectGroupPython] Cl_element011  label="Cl_element : 0.000"  # scripted group (container) (typed FeaturePython)
  n = 3.4e-05
FEATURE [App::DocumentObjectGroupPython] Fe_element006  label="Fe_element : 0.000"  # scripted group (container) (typed FeaturePython)
  n = 5.4e-05
FEATURE [App::DocumentObjectGroupPython] G4_FERROUS_SULFATE  # scripted group (container) (typed FeaturePython)
  Dunit = g/cm3
  Dvalue = 1.024
  Group = -> [H_element040,N_element017,O_element040,Na_element007,S_element011,Cl_element011,Fe_element006]
  conduct = 2
  density = 1
  expand = 3
  formula = G4_FERROUS_SULFATE
  name = G4_FERROUS_SULFATE
  specific = 4
FEATURE [App::DocumentObjectGroupPython] C_element043  label="C_element : 0.099"  # scripted group (container) (typed FeaturePython)
  n = 0.099335
FEATURE [App::DocumentObjectGroupPython] F_element007  label="F_element : 0.314"  # scripted group (container) (typed FeaturePython)
  n = 0.314247
FEATURE [App::DocumentObjectGroupPython] Cl_element012  label="Cl_element : 0.586"  # scripted group (container) (typed FeaturePython)
  n = 0.586418
FEATURE [App::DocumentObjectGroupPython] G4_FREON_12  label="G4_FREON-12"  # scripted group (container) (typed FeaturePython)
  Dunit = g/cm3
  Dvalue = 1.12
  Group = -> [C_element043,F_element007,Cl_element012]
  conduct = 2
  density = 1
  expand = 3
  formula = G4_FREON-12
  name = G4_FREON-12
  specific = 4
FEATURE [App::DocumentObjectGroupPython] C_element044  label="C_element : 0.057"  # scripted group (container) (typed FeaturePython)
  n = 0.057245
FEATURE [App::DocumentObjectGroupPython] F_element008  label="F_element : 0.181"  # scripted group (container) (typed FeaturePython)
  n = 0.181096
FEATURE [App::DocumentObjectGroupPython] Br_element001  label="Br_element : 0.762"  # scripted group (container) (typed FeaturePython)
  n = 0.761659
FEATURE [App::DocumentObjectGroupPython] G4_FREON_12B2  label="G4_FREON-12B2"  # scripted group (container) (typed FeaturePython)
  Dunit = g/cm3
  Dvalue = 1.8
  Group = -> [C_element044,F_element008,Br_element001]
  conduct = 2
  density = 1
  expand = 3
  formula = G4_FREON-12B2
  name = G4_FREON-12B2
  specific = 4
FEATURE [App::DocumentObjectGroupPython] C_element045  label="C_element : 0.115"  # scripted group (container) (typed FeaturePython)
  n = 0.114983
FEATURE [App::DocumentObjectGroupPython] F_element009  label="F_element : 0.546"  # scripted group (container) (typed FeaturePython)
  n = 0.545621
FEATURE [App::DocumentObjectGroupPython] Cl_element013  label="Cl_element : 0.339"  # scripted group (container) (typed FeaturePython)
  n = 0.339396
FEATURE [App::DocumentObjectGroupPython] G4_FREON_13  label="G4_FREON-13"  # scripted group (container) (typed FeaturePython)
  Dunit = g/cm3
  Dvalue = 0.95
  Group = -> [C_element045,F_element009,Cl_element013]
  conduct = 2
  density = 1
  expand = 3
  formula = G4_FREON-13
  name = G4_FREON-13
  specific = 4
FEATURE [App::DocumentObjectGroupPython] C_element046  label="C_element : 025"  # scripted group (container) (typed FeaturePython)
  n = 1
  ref = C_element
FEATURE [App::DocumentObjectGroupPython] F_element010  label="F_element : 3"  # scripted group (container) (typed FeaturePython)
  n = 3
  ref = F_element
FEATURE [App::DocumentObjectGroupPython] Br_element002  label="Br_element : 1"  # scripted group (container) (typed FeaturePython)
  n = 1
  ref = Br_element
FEATURE [App::DocumentObjectGroupPython] G4_FREON_13B1  label="G4_FREON-13B1"  # scripted group (container) (typed FeaturePython)
  Dunit = g/cm3
  Dvalue = 1.5
  Group = -> [C_element046,F_element010,Br_element002]
  conduct = 2
  density = 1
  expand = 3
  formula = G4_FREON-13B1
  name = G4_FREON-13B1
  specific = 4
FEATURE [App::DocumentObjectGroupPython] C_element047  label="C_element : 0.061"  # scripted group (container) (typed FeaturePython)
  n = 0.061309
FEATURE [App::DocumentObjectGroupPython] F_element011  label="F_element : 0.291"  # scripted group (container) (typed FeaturePython)
  n = 0.290924
FEATURE [App::DocumentObjectGroupPython] I_element002  label="I_element : 0.648"  # scripted group (container) (typed FeaturePython)
  n = 0.647767
FEATURE [App::DocumentObjectGroupPython] G4_FREON_13I1  label="G4_FREON-13I1"  # scripted group (container) (typed FeaturePython)
  Dunit = g/cm3
  Dvalue = 1.8
  Group = -> [C_element047,F_element011,I_element002]
  conduct = 2
  density = 1
  expand = 3
  formula = G4_FREON-13I1
  name = G4_FREON-13I1
  specific = 4
FEATURE [App::DocumentObjectGroupPython] Gd_element001  label="Gd_element : 2"  # scripted group (container) (typed FeaturePython)
  n = 2
  ref = Gd_element
FEATURE [App::DocumentObjectGroupPython] O_element041  label="O_element : 021"  # scripted group (container) (typed FeaturePython)
  n = 2
  ref = O_element
FEATURE [App::DocumentObjectGroupPython] S_element012  label="S_element : 004"  # scripted group (container) (typed FeaturePython)
  n = 1
  ref = S_element
FEATURE [App::DocumentObjectGroupPython] G4_GADOLINIUM_OXYSULFIDE  # scripted group (container) (typed FeaturePython)
  Dunit = g/cm3
  Dvalue = 7.44
  Group = -> [Gd_element001,O_element041,S_element012]
  conduct = 2
  density = 1
  expand = 3
  formula = G4_GADOLINIUM_OXYSULFIDE
  name = G4_GADOLINIUM_OXYSULFIDE
  specific = 4
FEATURE [App::DocumentObjectGroupPython] Ga_element001  label="Ga_element : 1"  # scripted group (container) (typed FeaturePython)
  n = 1
  ref = Ga_element
FEATURE [App::DocumentObjectGroupPython] As_element001  label="As_element : 1"  # scripted group (container) (typed FeaturePython)
  n = 1
  ref = As_element
FEATURE [App::DocumentObjectGroupPython] G4_GALLIUM_ARSENIDE  # scripted group (container) (typed FeaturePython)
  Dunit = g/cm3
  Dvalue = 5.31
  Group = -> [Ga_element001,As_element001]
  conduct = 2
  density = 1
  expand = 3
  formula = G4_GALLIUM_ARSENIDE
  name = G4_GALLIUM_ARSENIDE
  specific = 4
FEATURE [App::DocumentObjectGroupPython] H_element041  label="H_element : 0.081"  # scripted group (container) (typed FeaturePython)
  n = 0.08118
FEATURE [App::DocumentObjectGroupPython] C_element048  label="C_element : 0.416"  # scripted group (container) (typed FeaturePython)
  n = 0.41606
FEATURE [App::DocumentObjectGroupPython] N_element018  label="N_element : 0.111"  # scripted group (container) (typed FeaturePython)
  n = 0.11124
FEATURE [App::DocumentObjectGroupPython] O_element042  label="O_element : 0.381"  # scripted group (container) (typed FeaturePython)
  n = 0.38064
FEATURE [App::DocumentObjectGroupPython] S_element013  label="S_element : 0.011"  # scripted group (container) (typed FeaturePython)
  n = 0.01088
FEATURE [App::DocumentObjectGroupPython] G4_GEL_PHOTO_EMULSION  # scripted group (container) (typed FeaturePython)
  Dunit = g/cm3
  Dvalue = 1.2914
  Group = -> [H_element041,C_element048,N_element018,O_element042,S_element013]
  conduct = 2
  density = 1
  expand = 3
  formula = G4_GEL_PHOTO_EMULSION
  name = G4_GEL_PHOTO_EMULSION
  specific = 4
FEATURE [App::DocumentObjectGroupPython] B_element004  label="B_element : 0.040"  # scripted group (container) (typed FeaturePython)
  n = 0.0400639
FEATURE [App::DocumentObjectGroupPython] O_element043  label="O_element : 0.540"  # scripted group (container) (typed FeaturePython)
  n = 0.539561
FEATURE [App::DocumentObjectGroupPython] Na_element008  label="Na_element : 0.028"  # scripted group (container) (typed FeaturePython)
  n = 0.0281909
FEATURE [App::DocumentObjectGroupPython] Al_element003  label="Al_element : 0.012"  # scripted group (container) (typed FeaturePython)
  n = 0.011644
FEATURE [App::DocumentObjectGroupPython] Si_element003  label="Si_element : 0.377"  # scripted group (container) (typed FeaturePython)
  n = 0.377219
FEATURE [App::DocumentObjectGroupPython] K_element004  label="K_element : 0.014"  # scripted group (container) (typed FeaturePython)
  n = 0.00332099
FEATURE [App::DocumentObjectGroupPython] G4_Pyrex_Glass  # scripted group (container) (typed FeaturePython)
  Dunit = g/cm3
  Dvalue = 2.23
  Group = -> [B_element004,O_element043,Na_element008,Al_element003,Si_element003,K_element004]
  conduct = 2
  density = 1
  expand = 3
  formula = G4_Pyrex_Glass
  name = G4_Pyrex_Glass
  specific = 4
FEATURE [App::DocumentObjectGroupPython] O_element044  label="O_element : 0.156"  # scripted group (container) (typed FeaturePython)
  n = 0.156453
FEATURE [App::DocumentObjectGroupPython] Si_element004  label="Si_element : 0.081"  # scripted group (container) (typed FeaturePython)
  n = 0.080866
FEATURE [App::DocumentObjectGroupPython] Ti_element001  label="Ti_element : 0.008"  # scripted group (container) (typed FeaturePython)
  n = 0.008092
FEATURE [App::DocumentObjectGroupPython] As_element002  label="As_element : 0.003"  # scripted group (container) (typed FeaturePython)
  n = 0.002651
FEATURE [App::DocumentObjectGroupPython] Pb_element001  label="Pb_element : 0.752"  # scripted group (container) (typed FeaturePython)
  n = 0.751938
FEATURE [App::DocumentObjectGroupPython] G4_GLASS_LEAD  # scripted group (container) (typed FeaturePython)
  Dunit = g/cm3
  Dvalue = 6.22
  Group = -> [O_element044,Si_element004,Ti_element001,As_element002,Pb_element001]
  conduct = 2
  density = 1
  expand = 3
  formula = G4_GLASS_LEAD
  name = G4_GLASS_LEAD
  specific = 4
FEATURE [App::DocumentObjectGroupPython] O_element045  label="O_element : 0.460"  # scripted group (container) (typed FeaturePython)
  n = 0.4598
FEATURE [App::DocumentObjectGroupPython] Na_element009  label="Na_element : 0.096"  # scripted group (container) (typed FeaturePython)
  n = 0.0964411
FEATURE [App::DocumentObjectGroupPython] Si_element005  label="Si_element : 0.378"  # scripted group (container) (typed FeaturePython)
  n = 0.336553
FEATURE [App::DocumentObjectGroupPython] Ca_element011  label="Ca_element : 0.107"  # scripted group (container) (typed FeaturePython)
  n = 0.107205
FEATURE [App::DocumentObjectGroupPython] G4_GLASS_PLATE  # scripted group (container) (typed FeaturePython)
  Dunit = g/cm3
  Dvalue = 2.4
  Group = -> [O_element045,Na_element009,Si_element005,Ca_element011]
  conduct = 2
  density = 1
  expand = 3
  formula = G4_GLASS_PLATE
  name = G4_GLASS_PLATE
  specific = 4
FEATURE [App::DocumentObjectGroupPython] C_element049  label="C_element : 026"  # scripted group (container) (typed FeaturePython)
  n = 5
  ref = C_element
FEATURE [App::DocumentObjectGroupPython] H_element042  label="H_element : 021"  # scripted group (container) (typed FeaturePython)
  n = 10
  ref = H_element
FEATURE [App::DocumentObjectGroupPython] N_element019  label="N_element : 2"  # scripted group (container) (typed FeaturePython)
  n = 2
  ref = N_element
FEATURE [App::DocumentObjectGroupPython] O_element046  label="O_element : 022"  # scripted group (container) (typed FeaturePython)
  n = 3
  ref = O_element
FEATURE [App::DocumentObjectGroupPython] G4_GLUTAMINE  # scripted group (container) (typed FeaturePython)
  Dunit = g/cm3
  Dvalue = 1.46
  Group = -> [C_element049,H_element042,N_element019,O_element046]
  conduct = 2
  density = 1
  expand = 3
  formula = G4_GLUTAMINE
  name = G4_GLUTAMINE
  specific = 4
FEATURE [App::DocumentObjectGroupPython] C_element050  label="C_element : 027"  # scripted group (container) (typed FeaturePython)
  n = 3
  ref = C_element
FEATURE [App::DocumentObjectGroupPython] H_element043  label="H_element : 022"  # scripted group (container) (typed FeaturePython)
  n = 8
  ref = H_element
FEATURE [App::DocumentObjectGroupPython] O_element047  label="O_element : 023"  # scripted group (container) (typed FeaturePython)
  n = 3
  ref = O_element
FEATURE [App::DocumentObjectGroupPython] G4_GLYCEROL  # scripted group (container) (typed FeaturePython)
  Dunit = g/cm3
  Dvalue = 1.2613
  Group = -> [C_element050,H_element043,O_element047]
  conduct = 2
  density = 1
  expand = 3
  formula = G4_GLYCEROL
  name = G4_GLYCEROL
  specific = 4
FEATURE [App::DocumentObjectGroupPython] C_element051  label="C_element : 028"  # scripted group (container) (typed FeaturePython)
  n = 5
  ref = C_element
FEATURE [App::DocumentObjectGroupPython] H_element044  label="H_element : 023"  # scripted group (container) (typed FeaturePython)
  n = 5
  ref = H_element
FEATURE [App::DocumentObjectGroupPython] N_element020  label="N_element : 009"  # scripted group (container) (typed FeaturePython)
  n = 5
  ref = N_element
FEATURE [App::DocumentObjectGroupPython] O_element048  label="O_element : 024"  # scripted group (container) (typed FeaturePython)
  n = 1
  ref = O_element
FEATURE [App::DocumentObjectGroupPython] G4_GUANINE  # scripted group (container) (typed FeaturePython)
  Dunit = g/cm3
  Dvalue = 2.2
  Group = -> [C_element051,H_element044,N_element020,O_element048]
  conduct = 2
  density = 1
  expand = 3
  formula = G4_GUANINE
  name = G4_GUANINE
  specific = 4
FEATURE [App::DocumentObjectGroupPython] Ca_element012  label="Ca_element : 006"  # scripted group (container) (typed FeaturePython)
  n = 1
  ref = Ca_element
FEATURE [App::DocumentObjectGroupPython] S_element014  label="S_element : 005"  # scripted group (container) (typed FeaturePython)
  n = 1
  ref = S_element
FEATURE [App::DocumentObjectGroupPython] O_element049  label="O_element : 6"  # scripted group (container) (typed FeaturePython)
  n = 6
  ref = O_element
FEATURE [App::DocumentObjectGroupPython] H_element045  label="H_element : 024"  # scripted group (container) (typed FeaturePython)
  n = 4
  ref = H_element
FEATURE [App::DocumentObjectGroupPython] G4_GYPSUM  # scripted group (container) (typed FeaturePython)
  Dunit = g/cm3
  Dvalue = 2.32
  Group = -> [Ca_element012,S_element014,O_element049,H_element045]
  conduct = 2
  density = 1
  expand = 3
  formula = G4_GYPSUM
  name = G4_GYPSUM
  specific = 4
FEATURE [App::DocumentObjectGroupPython] C_element052  label="C_element : 7"  # scripted group (container) (typed FeaturePython)
  n = 7
  ref = C_element
FEATURE [App::DocumentObjectGroupPython] H_element046  label="H_element : 16"  # scripted group (container) (typed FeaturePython)
  n = 16
  ref = H_element
FEATURE [App::DocumentObjectGroupPython] G4_N_HEPTANE  label="G4_N-HEPTANE"  # scripted group (container) (typed FeaturePython)
  Dunit = g/cm3
  Dvalue = 0.68376
  Group = -> [C_element052,H_element046]
  conduct = 2
  density = 1
  expand = 3
  formula = G4_N-HEPTANE
  name = G4_N-HEPTANE
  specific = 4
FEATURE [App::DocumentObjectGroupPython] C_element053  label="C_element : 029"  # scripted group (container) (typed FeaturePython)
  n = 6
  ref = C_element
FEATURE [App::DocumentObjectGroupPython] H_element047  label="H_element : 14"  # scripted group (container) (typed FeaturePython)
  n = 14
  ref = H_element
FEATURE [App::DocumentObjectGroupPython] G4_N_HEXANE  label="G4_N-HEXANE"  # scripted group (container) (typed FeaturePython)
  Dunit = g/cm3
  Dvalue = 0.6603
  Group = -> [C_element053,H_element047]
  conduct = 2
  density = 1
  expand = 3
  formula = G4_N-HEXANE
  name = G4_N-HEXANE
  specific = 4
FEATURE [App::DocumentObjectGroupPython] C_element054  label="C_element : 22"  # scripted group (container) (typed FeaturePython)
  n = 22
  ref = C_element
FEATURE [App::DocumentObjectGroupPython] H_element048  label="H_element : 025"  # scripted group (container) (typed FeaturePython)
  n = 10
  ref = H_element
FEATURE [App::DocumentObjectGroupPython] N_element021  label="N_element : 010"  # scripted group (container) (typed FeaturePython)
  n = 2
  ref = N_element
FEATURE [App::DocumentObjectGroupPython] O_element050  label="O_element : 025"  # scripted group (container) (typed FeaturePython)
  n = 5
  ref = O_element
FEATURE [App::DocumentObjectGroupPython] G4_KAPTON  # scripted group (container) (typed FeaturePython)
  Dunit = g/cm3
  Dvalue = 1.42
  Group = -> [C_element054,H_element048,N_element021,O_element050]
  conduct = 2
  density = 1
  expand = 3
  formula = G4_KAPTON
  name = G4_KAPTON
  specific = 4
FEATURE [App::DocumentObjectGroupPython] La_element001  label="La_element : 1"  # scripted group (container) (typed FeaturePython)
  n = 1
  ref = La_element
FEATURE [App::DocumentObjectGroupPython] Br_element003  label="Br_element : 002"  # scripted group (container) (typed FeaturePython)
  n = 1
  ref = Br_element
FEATURE [App::DocumentObjectGroupPython] O_element051  label="O_element : 026"  # scripted group (container) (typed FeaturePython)
  n = 1
  ref = O_element
FEATURE [App::DocumentObjectGroupPython] G4_LANTHANUM_OXYBROMIDE  # scripted group (container) (typed FeaturePython)
  Dunit = g/cm3
  Dvalue = 6.28
  Group = -> [La_element001,Br_element003,O_element051]
  conduct = 2
  density = 1
  expand = 3
  formula = G4_LANTHANUM_OXYBROMIDE
  name = G4_LANTHANUM_OXYBROMIDE
  specific = 4
FEATURE [App::DocumentObjectGroupPython] La_element002  label="La_element : 2"  # scripted group (container) (typed FeaturePython)
  n = 2
  ref = La_element
FEATURE [App::DocumentObjectGroupPython] O_element052  label="O_element : 027"  # scripted group (container) (typed FeaturePython)
  n = 2
  ref = O_element
FEATURE [App::DocumentObjectGroupPython] S_element015  label="S_element : 006"  # scripted group (container) (typed FeaturePython)
  n = 1
  ref = S_element
FEATURE [App::DocumentObjectGroupPython] G4_LANTHANUM_OXYSULFIDE  # scripted group (container) (typed FeaturePython)
  Dunit = g/cm3
  Dvalue = 5.86
  Group = -> [La_element002,O_element052,S_element015]
  conduct = 2
  density = 1
  expand = 3
  formula = G4_LANTHANUM_OXYSULFIDE
  name = G4_LANTHANUM_OXYSULFIDE
  specific = 4
FEATURE [App::DocumentObjectGroupPython] O_element053  label="O_element : 0.072"  # scripted group (container) (typed FeaturePython)
  n = 0.071682
FEATURE [App::DocumentObjectGroupPython] Pb_element002  label="Pb_element : 0.928"  # scripted group (container) (typed FeaturePython)
  n = 0.928318
FEATURE [App::DocumentObjectGroupPython] G4_LEAD_OXIDE  # scripted group (container) (typed FeaturePython)
  Dunit = g/cm3
  Dvalue = 9.53
  Group = -> [O_element053,Pb_element002]
  conduct = 2
  density = 1
  expand = 3
  formula = G4_LEAD_OXIDE
  name = G4_LEAD_OXIDE
  specific = 4
FEATURE [App::DocumentObjectGroupPython] Li_element001  label="Li_element : 1"  # scripted group (container) (typed FeaturePython)
  n = 1
  ref = Li_element
FEATURE [App::DocumentObjectGroupPython] N_element022  label="N_element : 011"  # scripted group (container) (typed FeaturePython)
  n = 1
  ref = N_element
FEATURE [App::DocumentObjectGroupPython] H_element049  label="H_element : 026"  # scripted group (container) (typed FeaturePython)
  n = 2
  ref = H_element
FEATURE [App::DocumentObjectGroupPython] G4_LITHIUM_AMIDE  # scripted group (container) (typed FeaturePython)
  Dunit = g/cm3
  Dvalue = 1.178
  Group = -> [Li_element001,N_element022,H_element049]
  conduct = 2
  density = 1
  expand = 3
  formula = G4_LITHIUM_AMIDE
  name = G4_LITHIUM_AMIDE
  specific = 4
FEATURE [App::DocumentObjectGroupPython] Li_element002  label="Li_element : 2"  # scripted group (container) (typed FeaturePython)
  n = 2
  ref = Li_element
FEATURE [App::DocumentObjectGroupPython] C_element055  label="C_element : 030"  # scripted group (container) (typed FeaturePython)
  n = 1
  ref = C_element
FEATURE [App::DocumentObjectGroupPython] O_element054  label="O_element : 028"  # scripted group (container) (typed FeaturePython)
  n = 3
  ref = O_element
FEATURE [App::DocumentObjectGroupPython] G4_LITHIUM_CARBONATE  # scripted group (container) (typed FeaturePython)
  Dunit = g/cm3
  Dvalue = 2.11
  Group = -> [Li_element002,C_element055,O_element054]
  conduct = 2
  density = 1
  expand = 3
  formula = G4_LITHIUM_CARBONATE
  name = G4_LITHIUM_CARBONATE
  specific = 4
FEATURE [App::DocumentObjectGroupPython] Li_element003  label="Li_element : 003"  # scripted group (container) (typed FeaturePython)
  n = 1
  ref = Li_element
FEATURE [App::DocumentObjectGroupPython] F_element012  label="F_element : 004"  # scripted group (container) (typed FeaturePython)
  n = 1
  ref = F_element
FEATURE [App::DocumentObjectGroupPython] G4_LITHIUM_FLUORIDE  # scripted group (container) (typed FeaturePython)
  Dunit = g/cm3
  Dvalue = 2.635
  Group = -> [Li_element003,F_element012]
  conduct = 2
  density = 1
  expand = 3
  formula = G4_LITHIUM_FLUORIDE
  name = G4_LITHIUM_FLUORIDE
  specific = 4
FEATURE [App::DocumentObjectGroupPython] Li_element004  label="Li_element : 004"  # scripted group (container) (typed FeaturePython)
  n = 1
  ref = Li_element
FEATURE [App::DocumentObjectGroupPython] H_element050  label="H_element : 027"  # scripted group (container) (typed FeaturePython)
  n = 1
  ref = H_element
FEATURE [App::DocumentObjectGroupPython] G4_LITHIUM_HYDRIDE  # scripted group (container) (typed FeaturePython)
  Dunit = g/cm3
  Dvalue = 0.82
  Group = -> [Li_element004,H_element050]
  conduct = 2
  density = 1
  expand = 3
  formula = G4_LITHIUM_HYDRIDE
  name = G4_LITHIUM_HYDRIDE
  specific = 4
FEATURE [App::DocumentObjectGroupPython] Li_element005  label="Li_element : 005"  # scripted group (container) (typed FeaturePython)
  n = 1
  ref = Li_element
FEATURE [App::DocumentObjectGroupPython] I_element003  label="I_element : 002"  # scripted group (container) (typed FeaturePython)
  n = 1
  ref = I_element
FEATURE [App::DocumentObjectGroupPython] G4_LITHIUM_IODIDE  # scripted group (container) (typed FeaturePython)
  Dunit = g/cm3
  Dvalue = 3.494
  Group = -> [Li_element005,I_element003]
  conduct = 2
  density = 1
  expand = 3
  formula = G4_LITHIUM_IODIDE
  name = G4_LITHIUM_IODIDE
  specific = 4
FEATURE [App::DocumentObjectGroupPython] Li_element006  label="Li_element : 006"  # scripted group (container) (typed FeaturePython)
  n = 2
  ref = Li_element
FEATURE [App::DocumentObjectGroupPython] O_element055  label="O_element : 029"  # scripted group (container) (typed FeaturePython)
  n = 1
  ref = O_element
FEATURE [App::DocumentObjectGroupPython] G4_LITHIUM_OXIDE  # scripted group (container) (typed FeaturePython)
  Dunit = g/cm3
  Dvalue = 2.013
  Group = -> [Li_element006,O_element055]
  conduct = 2
  density = 1
  expand = 3
  formula = G4_LITHIUM_OXIDE
  name = G4_LITHIUM_OXIDE
  specific = 4
FEATURE [App::DocumentObjectGroupPython] Li_element007  label="Li_element : 007"  # scripted group (container) (typed FeaturePython)
  n = 2
  ref = Li_element
FEATURE [App::DocumentObjectGroupPython] B_element005  label="B_element : 005"  # scripted group (container) (typed FeaturePython)
  n = 4
  ref = B_element
FEATURE [App::DocumentObjectGroupPython] O_element056  label="O_element : 7"  # scripted group (container) (typed FeaturePython)
  n = 7
  ref = O_element
FEATURE [App::DocumentObjectGroupPython] G4_LITHIUM_TETRABORATE  # scripted group (container) (typed FeaturePython)
  Dunit = g/cm3
  Dvalue = 2.44
  Group = -> [Li_element007,B_element005,O_element056]
  conduct = 2
  density = 1
  expand = 3
  formula = G4_LITHIUM_TETRABORATE
  name = G4_LITHIUM_TETRABORATE
  specific = 4
FEATURE [App::DocumentObjectGroupPython] H_element051  label="H_element : 0.105"  # scripted group (container) (typed FeaturePython)
  n = 0.105
FEATURE [App::DocumentObjectGroupPython] C_element056  label="C_element : 0.083"  # scripted group (container) (typed FeaturePython)
  n = 0.083
FEATURE [App::DocumentObjectGroupPython] N_element023  label="N_element : 0.023"  # scripted group (container) (typed FeaturePython)
  n = 0.023
FEATURE [App::DocumentObjectGroupPython] O_element057  label="O_element : 0.779"  # scripted group (container) (typed FeaturePython)
  n = 0.779
FEATURE [App::DocumentObjectGroupPython] Na_element010  label="Na_element : 0.097"  # scripted group (container) (typed FeaturePython)
  n = 0.002
FEATURE [App::DocumentObjectGroupPython] P_element006  label="P_element : 0.105"  # scripted group (container) (typed FeaturePython)
  n = 0.001
FEATURE [App::DocumentObjectGroupPython] S_element016  label="S_element : 0.017"  # scripted group (container) (typed FeaturePython)
  n = 0.002
FEATURE [App::DocumentObjectGroupPython] Cl_element014  label="Cl_element : 0.587"  # scripted group (container) (typed FeaturePython)
  n = 0.003
FEATURE [App::DocumentObjectGroupPython] K_element005  label="K_element : 0.015"  # scripted group (container) (typed FeaturePython)
  n = 0.002
FEATURE [App::DocumentObjectGroupPython] G4_LUNG_ICRP  # scripted group (container) (typed FeaturePython)
  Dunit = g/cm3
  Dvalue = 1.04
  Group = -> [H_element051,C_element056,N_element023,O_element057,Na_element010,P_element006,S_element016,Cl_element014,K_element005]
  conduct = 2
  density = 1
  expand = 3
  formula = G4_LUNG_ICRP
  name = G4_LUNG_ICRP
  specific = 4
FEATURE [App::DocumentObjectGroupPython] H_element052  label="H_element : 0.116"  # scripted group (container) (typed FeaturePython)
  n = 0.114318
FEATURE [App::DocumentObjectGroupPython] C_element057  label="C_element : 0.656"  # scripted group (container) (typed FeaturePython)
  n = 0.655824
FEATURE [App::DocumentObjectGroupPython] O_element058  label="O_element : 0.092"  # scripted group (container) (typed FeaturePython)
  n = 0.0921831
FEATURE [App::DocumentObjectGroupPython] Mg_element004  label="Mg_element : 0.135"  # scripted group (container) (typed FeaturePython)
  n = 0.134792
FEATURE [App::DocumentObjectGroupPython] Ca_element013  label="Ca_element : 0.003"  # scripted group (container) (typed FeaturePython)
  n = 0.002883
FEATURE [App::DocumentObjectGroupPython] G4_M3_WAX  # scripted group (container) (typed FeaturePython)
  Dunit = g/cm3
  Dvalue = 1.05
  Group = -> [H_element052,C_element057,O_element058,Mg_element004,Ca_element013]
  conduct = 2
  density = 1
  expand = 3
  formula = G4_M3_WAX
  name = G4_M3_WAX
  specific = 4
FEATURE [App::DocumentObjectGroupPython] Mg_element005  label="Mg_element : 1"  # scripted group (container) (typed FeaturePython)
  n = 1
  ref = Mg_element
FEATURE [App::DocumentObjectGroupPython] C_element058  label="C_element : 031"  # scripted group (container) (typed FeaturePython)
  n = 1
  ref = C_element
FEATURE [App::DocumentObjectGroupPython] O_element059  label="O_element : 030"  # scripted group (container) (typed FeaturePython)
  n = 3
  ref = O_element
FEATURE [App::DocumentObjectGroupPython] G4_MAGNESIUM_CARBONATE  # scripted group (container) (typed FeaturePython)
  Dunit = g/cm3
  Dvalue = 2.958
  Group = -> [Mg_element005,C_element058,O_element059]
  conduct = 2
  density = 1
  expand = 3
  formula = G4_MAGNESIUM_CARBONATE
  name = G4_MAGNESIUM_CARBONATE
  specific = 4
FEATURE [App::DocumentObjectGroupPython] Mg_element006  label="Mg_element : 002"  # scripted group (container) (typed FeaturePython)
  n = 1
  ref = Mg_element
FEATURE [App::DocumentObjectGroupPython] F_element013  label="F_element : 005"  # scripted group (container) (typed FeaturePython)
  n = 2
  ref = F_element
FEATURE [App::DocumentObjectGroupPython] G4_MAGNESIUM_FLUORIDE  # scripted group (container) (typed FeaturePython)
  Dunit = g/cm3
  Dvalue = 3
  Group = -> [Mg_element006,F_element013]
  conduct = 2
  density = 1
  expand = 3
  formula = G4_MAGNESIUM_FLUORIDE
  name = G4_MAGNESIUM_FLUORIDE
  specific = 4
FEATURE [App::DocumentObjectGroupPython] Mg_element007  label="Mg_element : 003"  # scripted group (container) (typed FeaturePython)
  n = 1
  ref = Mg_element
FEATURE [App::DocumentObjectGroupPython] O_element060  label="O_element : 031"  # scripted group (container) (typed FeaturePython)
  n = 1
  ref = O_element
FEATURE [App::DocumentObjectGroupPython] G4_MAGNESIUM_OXIDE  # scripted group (container) (typed FeaturePython)
  Dunit = g/cm3
  Dvalue = 3.58
  Group = -> [Mg_element007,O_element060]
  conduct = 2
  density = 1
  expand = 3
  formula = G4_MAGNESIUM_OXIDE
  name = G4_MAGNESIUM_OXIDE
  specific = 4
FEATURE [App::DocumentObjectGroupPython] Mg_element008  label="Mg_element : 004"  # scripted group (container) (typed FeaturePython)
  n = 1
  ref = Mg_element
FEATURE [App::DocumentObjectGroupPython] B_element006  label="B_element : 006"  # scripted group (container) (typed FeaturePython)
  n = 4
  ref = B_element
FEATURE [App::DocumentObjectGroupPython] O_element061  label="O_element : 032"  # scripted group (container) (typed FeaturePython)
  n = 7
  ref = O_element
FEATURE [App::DocumentObjectGroupPython] G4_MAGNESIUM_TETRABORATE  # scripted group (container) (typed FeaturePython)
  Dunit = g/cm3
  Dvalue = 2.53
  Group = -> [Mg_element008,B_element006,O_element061]
  conduct = 2
  density = 1
  expand = 3
  formula = G4_MAGNESIUM_TETRABORATE
  name = G4_MAGNESIUM_TETRABORATE
  specific = 4
FEATURE [App::DocumentObjectGroupPython] Hg_element001  label="Hg_element : 1"  # scripted group (container) (typed FeaturePython)
  n = 1
  ref = Hg_element
FEATURE [App::DocumentObjectGroupPython] I_element004  label="I_element : 2"  # scripted group (container) (typed FeaturePython)
  n = 2
  ref = I_element
FEATURE [App::DocumentObjectGroupPython] G4_MERCURIC_IODIDE  # scripted group (container) (typed FeaturePython)
  Dunit = g/cm3
  Dvalue = 6.36
  Group = -> [Hg_element001,I_element004]
  conduct = 2
  density = 1
  expand = 3
  formula = G4_MERCURIC_IODIDE
  name = G4_MERCURIC_IODIDE
  specific = 4
FEATURE [App::DocumentObjectGroupPython] C_element059  label="C_element : 032"  # scripted group (container) (typed FeaturePython)
  n = 1
  ref = C_element
FEATURE [App::DocumentObjectGroupPython] H_element053  label="H_element : 028"  # scripted group (container) (typed FeaturePython)
  n = 4
  ref = H_element
FEATURE [App::DocumentObjectGroupPython] G4_METHANE  # scripted group (container) (typed FeaturePython)
  Dunit = g/cm3
  Dvalue = 0.000667151
  Group = -> [C_element059,H_element053]
  conduct = 2
  density = 1
  expand = 3
  formula = G4_METHANE
  name = G4_METHANE
  specific = 4
FEATURE [App::DocumentObjectGroupPython] C_element060  label="C_element : 033"  # scripted group (container) (typed FeaturePython)
  n = 1
  ref = C_element
FEATURE [App::DocumentObjectGroupPython] H_element054  label="H_element : 029"  # scripted group (container) (typed FeaturePython)
  n = 4
  ref = H_element
FEATURE [App::DocumentObjectGroupPython] O_element062  label="O_element : 033"  # scripted group (container) (typed FeaturePython)
  n = 1
  ref = O_element
FEATURE [App::DocumentObjectGroupPython] G4_METHANOL  # scripted group (container) (typed FeaturePython)
  Dunit = g/cm3
  Dvalue = 0.7914
  Group = -> [C_element060,H_element054,O_element062]
  conduct = 2
  density = 1
  expand = 3
  formula = G4_METHANOL
  name = G4_METHANOL
  specific = 4
FEATURE [App::DocumentObjectGroupPython] H_element055  label="H_element : 0.134"  # scripted group (container) (typed FeaturePython)
  n = 0.13404
FEATURE [App::DocumentObjectGroupPython] C_element061  label="C_element : 0.778"  # scripted group (container) (typed FeaturePython)
  n = 0.77796
FEATURE [App::DocumentObjectGroupPython] O_element063  label="O_element : 0.035"  # scripted group (container) (typed FeaturePython)
  n = 0.03502
FEATURE [App::DocumentObjectGroupPython] Mg_element009  label="Mg_element : 0.039"  # scripted group (container) (typed FeaturePython)
  n = 0.038594
FEATURE [App::DocumentObjectGroupPython] Ti_element002  label="Ti_element : 0.014"  # scripted group (container) (typed FeaturePython)
  n = 0.014386
FEATURE [App::DocumentObjectGroupPython] G4_MIX_D_WAX  # scripted group (container) (typed FeaturePython)
  Dunit = g/cm3
  Dvalue = 0.99
  Group = -> [H_element055,C_element061,O_element063,Mg_element009,Ti_element002]
  conduct = 2
  density = 1
  expand = 3
  formula = G4_MIX_D_WAX
  name = G4_MIX_D_WAX
  specific = 4
FEATURE [App::DocumentObjectGroupPython] H_element056  label="H_element : 0.135"  # scripted group (container) (typed FeaturePython)
  n = 0.081192
FEATURE [App::DocumentObjectGroupPython] C_element062  label="C_element : 0.583"  # scripted group (container) (typed FeaturePython)
  n = 0.583442
FEATURE [App::DocumentObjectGroupPython] N_element024  label="N_element : 0.018"  # scripted group (container) (typed FeaturePython)
  n = 0.017798
FEATURE [App::DocumentObjectGroupPython] O_element064  label="O_element : 0.186"  # scripted group (container) (typed FeaturePython)
  n = 0.186381
FEATURE [App::DocumentObjectGroupPython] Mg_element010  label="Mg_element : 0.130"  # scripted group (container) (typed FeaturePython)
  n = 0.130287
FEATURE [App::DocumentObjectGroupPython] Cl_element015  label="Cl_element : 0.588"  # scripted group (container) (typed FeaturePython)
  n = 0.0009
FEATURE [App::DocumentObjectGroupPython] G4_MS20_TISSUE  # scripted group (container) (typed FeaturePython)
  Dunit = g/cm3
  Dvalue = 1
  Group = -> [H_element056,C_element062,N_element024,O_element064,Mg_element010,Cl_element015]
  conduct = 2
  density = 1
  expand = 3
  formula = G4_MS20_TISSUE
  name = G4_MS20_TISSUE
  specific = 4
FEATURE [App::DocumentObjectGroupPython] H_element057  label="H_element : 0.136"  # scripted group (container) (typed FeaturePython)
  n = 0.102
FEATURE [App::DocumentObjectGroupPython] C_element063  label="C_element : 0.143"  # scripted group (container) (typed FeaturePython)
  n = 0.143
FEATURE [App::DocumentObjectGroupPython] N_element025  label="N_element : 0.034"  # scripted group (container) (typed FeaturePython)
  n = 0.034
FEATURE [App::DocumentObjectGroupPython] O_element065  label="O_element : 0.710"  # scripted group (container) (typed FeaturePython)
  n = 0.71
FEATURE [App::DocumentObjectGroupPython] Na_element011  label="Na_element : 0.098"  # scripted group (container) (typed FeaturePython)
  n = 0.001
FEATURE [App::DocumentObjectGroupPython] P_element007  label="P_element : 0.002"  # scripted group (container) (typed FeaturePython)
  n = 0.002
FEATURE [App::DocumentObjectGroupPython] S_element017  label="S_element : 0.018"  # scripted group (container) (typed FeaturePython)
  n = 0.003
FEATURE [App::DocumentObjectGroupPython] Cl_element016  label="Cl_element : 0.589"  # scripted group (container) (typed FeaturePython)
  n = 0.001
FEATURE [App::DocumentObjectGroupPython] K_element006  label="K_element : 0.004"  # scripted group (container) (typed FeaturePython)
  n = 0.004
FEATURE [App::DocumentObjectGroupPython] G4_MUSCLE_SKELETAL_ICRP  # scripted group (container) (typed FeaturePython)
  Dunit = g/cm3
  Dvalue = 1.05
  Group = -> [H_element057,C_element063,N_element025,O_element065,Na_element011,P_element007,S_element017,Cl_element016,K_element006]
  conduct = 2
  density = 1
  expand = 3
  formula = G4_MUSCLE_SKELETAL_ICRP
  name = G4_MUSCLE_SKELETAL_ICRP
  specific = 4
FEATURE [App::DocumentObjectGroupPython] H_element058  label="H_element : 0.137"  # scripted group (container) (typed FeaturePython)
  n = 0.102102
FEATURE [App::DocumentObjectGroupPython] C_element064  label="C_element : 0.123"  # scripted group (container) (typed FeaturePython)
  n = 0.123123
FEATURE [App::DocumentObjectGroupPython] N_element026  label="N_element : 0.756"  # scripted group (container) (typed FeaturePython)
  n = 0.035035
FEATURE [App::DocumentObjectGroupPython] O_element066  label="O_element : 0.730"  # scripted group (container) (typed FeaturePython)
  n = 0.72973
FEATURE [App::DocumentObjectGroupPython] Na_element012  label="Na_element : 0.099"  # scripted group (container) (typed FeaturePython)
  n = 0.001001
FEATURE [App::DocumentObjectGroupPython] P_element008  label="P_element : 0.106"  # scripted group (container) (typed FeaturePython)
  n = 0.002002
FEATURE [App::DocumentObjectGroupPython] S_element018  label="S_element : 0.019"  # scripted group (container) (typed FeaturePython)
  n = 0.004004
FEATURE [App::DocumentObjectGroupPython] K_element007  label="K_element : 0.016"  # scripted group (container) (typed FeaturePython)
  n = 0.003003
FEATURE [App::DocumentObjectGroupPython] G4_MUSCLE_STRIATED_ICRU  # scripted group (container) (typed FeaturePython)
  Dunit = g/cm3
  Dvalue = 1.04
  Group = -> [H_element058,C_element064,N_element026,O_element066,Na_element012,P_element008,S_element018,K_element007]
  conduct = 2
  density = 1
  expand = 3
  formula = G4_MUSCLE_STRIATED_ICRU
  name = G4_MUSCLE_STRIATED_ICRU
  specific = 4
FEATURE [App::DocumentObjectGroupPython] H_element059  label="H_element : 0.098"  # scripted group (container) (typed FeaturePython)
  n = 0.0982341
FEATURE [App::DocumentObjectGroupPython] C_element065  label="C_element : 0.156"  # scripted group (container) (typed FeaturePython)
  n = 0.156214
FEATURE [App::DocumentObjectGroupPython] N_element027  label="N_element : 0.757"  # scripted group (container) (typed FeaturePython)
  n = 0.035451
FEATURE [App::DocumentObjectGroupPython] O_element067  label="O_element : 0.880"  # scripted group (container) (typed FeaturePython)
  n = 0.710101
FEATURE [App::DocumentObjectGroupPython] G4_MUSCLE_WITH_SUCROSE  # scripted group (container) (typed FeaturePython)
  Dunit = g/cm3
  Dvalue = 1.11
  Group = -> [H_element059,C_element065,N_element027,O_element067]
  conduct = 2
  density = 1
  expand = 3
  formula = G4_MUSCLE_WITH_SUCROSE
  name = G4_MUSCLE_WITH_SUCROSE
  specific = 4
FEATURE [App::DocumentObjectGroupPython] H_element060  label="H_element : 0.138"  # scripted group (container) (typed FeaturePython)
  n = 0.101969
FEATURE [App::DocumentObjectGroupPython] C_element066  label="C_element : 0.120"  # scripted group (container) (typed FeaturePython)
  n = 0.120058
FEATURE [App::DocumentObjectGroupPython] N_element028  label="N_element : 0.758"  # scripted group (container) (typed FeaturePython)
  n = 0.035451
FEATURE [App::DocumentObjectGroupPython] O_element068  label="O_element : 0.743"  # scripted group (container) (typed FeaturePython)
  n = 0.742522
FEATURE [App::DocumentObjectGroupPython] G4_MUSCLE_WITHOUT_SUCROSE  # scripted group (container) (typed FeaturePython)
  Dunit = g/cm3
  Dvalue = 1.07
  Group = -> [H_element060,C_element066,N_element028,O_element068]
  conduct = 2
  density = 1
  expand = 3
  formula = G4_MUSCLE_WITHOUT_SUCROSE
  name = G4_MUSCLE_WITHOUT_SUCROSE
  specific = 4
FEATURE [App::DocumentObjectGroupPython] C_element067  label="C_element : 10"  # scripted group (container) (typed FeaturePython)
  n = 10
  ref = C_element
FEATURE [App::DocumentObjectGroupPython] H_element061  label="H_element : 030"  # scripted group (container) (typed FeaturePython)
  n = 8
  ref = H_element
FEATURE [App::DocumentObjectGroupPython] G4_NAPHTHALENE  # scripted group (container) (typed FeaturePython)
  Dunit = g/cm3
  Dvalue = 1.145
  Group = -> [C_element067,H_element061]
  conduct = 2
  density = 1
  expand = 3
  formula = G4_NAPHTHALENE
  name = G4_NAPHTHALENE
  specific = 4
FEATURE [App::DocumentObjectGroupPython] C_element068  label="C_element : 034"  # scripted group (container) (typed FeaturePython)
  n = 6
  ref = C_element
FEATURE [App::DocumentObjectGroupPython] H_element062  label="H_element : 031"  # scripted group (container) (typed FeaturePython)
  n = 5
  ref = H_element
FEATURE [App::DocumentObjectGroupPython] N_element029  label="N_element : 012"  # scripted group (container) (typed FeaturePython)
  n = 1
  ref = N_element
FEATURE [App::DocumentObjectGroupPython] O_element069  label="O_element : 034"  # scripted group (container) (typed FeaturePython)
  n = 2
  ref = O_element
FEATURE [App::DocumentObjectGroupPython] G4_NITROBENZENE  # scripted group (container) (typed FeaturePython)
  Dunit = g/cm3
  Dvalue = 1.19867
  Group = -> [C_element068,H_element062,N_element029,O_element069]
  conduct = 2
  density = 1
  expand = 3
  formula = G4_NITROBENZENE
  name = G4_NITROBENZENE
  specific = 4
FEATURE [App::DocumentObjectGroupPython] N_element030  label="N_element : 013"  # scripted group (container) (typed FeaturePython)
  n = 2
  ref = N_element
FEATURE [App::DocumentObjectGroupPython] O_element070  label="O_element : 035"  # scripted group (container) (typed FeaturePython)
  n = 1
  ref = O_element
FEATURE [App::DocumentObjectGroupPython] G4_NITROUS_OXIDE  # scripted group (container) (typed FeaturePython)
  Dunit = g/cm3
  Dvalue = 0.00183094
  Group = -> [N_element030,O_element070]
  conduct = 2
  density = 1
  expand = 3
  formula = G4_NITROUS_OXIDE
  name = G4_NITROUS_OXIDE
  specific = 4
FEATURE [App::DocumentObjectGroupPython] H_element063  label="H_element : 0.104"  # scripted group (container) (typed FeaturePython)
  n = 0.103509
FEATURE [App::DocumentObjectGroupPython] C_element069  label="C_element : 0.648"  # scripted group (container) (typed FeaturePython)
  n = 0.648416
FEATURE [App::DocumentObjectGroupPython] N_element031  label="N_element : 0.100"  # scripted group (container) (typed FeaturePython)
  n = 0.0995361
FEATURE [App::DocumentObjectGroupPython] O_element071  label="O_element : 0.149"  # scripted group (container) (typed FeaturePython)
  n = 0.148539
FEATURE [App::DocumentObjectGroupPython] G4_NYLON_8062  label="G4_NYLON-8062"  # scripted group (container) (typed FeaturePython)
  Dunit = g/cm3
  Dvalue = 1.08
  Group = -> [H_element063,C_element069,N_element031,O_element071]
  conduct = 2
  density = 1
  expand = 3
  formula = G4_NYLON-8062
  name = G4_NYLON-8062
  specific = 4
FEATURE [App::DocumentObjectGroupPython] C_element070  label="C_element : 035"  # scripted group (container) (typed FeaturePython)
  n = 6
  ref = C_element
FEATURE [App::DocumentObjectGroupPython] H_element064  label="H_element : 11"  # scripted group (container) (typed FeaturePython)
  n = 11
  ref = H_element
FEATURE [App::DocumentObjectGroupPython] N_element032  label="N_element : 014"  # scripted group (container) (typed FeaturePython)
  n = 1
  ref = N_element
FEATURE [App::DocumentObjectGroupPython] O_element072  label="O_element : 036"  # scripted group (container) (typed FeaturePython)
  n = 1
  ref = O_element
FEATURE [App::DocumentObjectGroupPython] G4_NYLON_6_6  label="G4_NYLON-6-6"  # scripted group (container) (typed FeaturePython)
  Dunit = g/cm3
  Dvalue = 1.14
  Group = -> [C_element070,H_element064,N_element032,O_element072]
  conduct = 2
  density = 1
  expand = 3
  formula = G4_NYLON-6-6
  name = G4_NYLON-6-6
  specific = 4
FEATURE [App::DocumentObjectGroupPython] H_element065  label="H_element : 0.139"  # scripted group (container) (typed FeaturePython)
  n = 0.107062
FEATURE [App::DocumentObjectGroupPython] C_element071  label="C_element : 0.680"  # scripted group (container) (typed FeaturePython)
  n = 0.680449
FEATURE [App::DocumentObjectGroupPython] N_element033  label="N_element : 0.099"  # scripted group (container) (typed FeaturePython)
  n = 0.099189
FEATURE [App::DocumentObjectGroupPython] O_element073  label="O_element : 0.113"  # scripted group (container) (typed FeaturePython)
  n = 0.1133
FEATURE [App::DocumentObjectGroupPython] G4_NYLON_6_10  label="G4_NYLON-6-10"  # scripted group (container) (typed FeaturePython)
  Dunit = g/cm3
  Dvalue = 1.14
  Group = -> [H_element065,C_element071,N_element033,O_element073]
  conduct = 2
  density = 1
  expand = 3
  formula = G4_NYLON-6-10
  name = G4_NYLON-6-10
  specific = 4
FEATURE [App::DocumentObjectGroupPython] H_element066  label="H_element : 0.140"  # scripted group (container) (typed FeaturePython)
  n = 0.115476
FEATURE [App::DocumentObjectGroupPython] C_element072  label="C_element : 0.721"  # scripted group (container) (typed FeaturePython)
  n = 0.720818
FEATURE [App::DocumentObjectGroupPython] N_element034  label="N_element : 0.076"  # scripted group (container) (typed FeaturePython)
  n = 0.0764169
FEATURE [App::DocumentObjectGroupPython] O_element074  label="O_element : 0.087"  # scripted group (container) (typed FeaturePython)
  n = 0.0872889
FEATURE [App::DocumentObjectGroupPython] G4_NYLON_11_RILSAN  label="G4_NYLON-11_RILSAN"  # scripted group (container) (typed FeaturePython)
  Dunit = g/cm3
  Dvalue = 1.425
  Group = -> [H_element066,C_element072,N_element034,O_element074]
  conduct = 2
  density = 1
  expand = 3
  formula = G4_NYLON-11_RILSAN
  name = G4_NYLON-11_RILSAN
  specific = 4
FEATURE [App::DocumentObjectGroupPython] C_element073  label="C_element : 8"  # scripted group (container) (typed FeaturePython)
  n = 8
  ref = C_element
FEATURE [App::DocumentObjectGroupPython] H_element067  label="H_element : 18"  # scripted group (container) (typed FeaturePython)
  n = 18
  ref = H_element
FEATURE [App::DocumentObjectGroupPython] G4_OCTANE  # scripted group (container) (typed FeaturePython)
  Dunit = g/cm3
  Dvalue = 0.7026
  Group = -> [C_element073,H_element067]
  conduct = 2
  density = 1
  expand = 3
  formula = G4_OCTANE
  name = G4_OCTANE
  specific = 4
FEATURE [App::DocumentObjectGroupPython] C_element074  label="C_element : 25"  # scripted group (container) (typed FeaturePython)
  n = 25
  ref = C_element
FEATURE [App::DocumentObjectGroupPython] H_element068  label="H_element : 52"  # scripted group (container) (typed FeaturePython)
  n = 52
  ref = H_element
FEATURE [App::DocumentObjectGroupPython] G4_PARAFFIN  # scripted group (container) (typed FeaturePython)
  Dunit = g/cm3
  Dvalue = 0.93
  Group = -> [C_element074,H_element068]
  conduct = 2
  density = 1
  expand = 3
  formula = G4_PARAFFIN
  name = G4_PARAFFIN
  specific = 4
FEATURE [App::DocumentObjectGroupPython] C_element075  label="C_element : 036"  # scripted group (container) (typed FeaturePython)
  n = 5
  ref = C_element
FEATURE [App::DocumentObjectGroupPython] H_element069  label="H_element : 032"  # scripted group (container) (typed FeaturePython)
  n = 12
  ref = H_element
FEATURE [App::DocumentObjectGroupPython] G4_N_PENTANE  label="G4_N-PENTANE"  # scripted group (container) (typed FeaturePython)
  Dunit = g/cm3
  Dvalue = 0.6262
  Group = -> [C_element075,H_element069]
  conduct = 2
  density = 1
  expand = 3
  formula = G4_N-PENTANE
  name = G4_N-PENTANE
  specific = 4
FEATURE [App::DocumentObjectGroupPython] H_element070  label="H_element : 0.014"  # scripted group (container) (typed FeaturePython)
  n = 0.0141
FEATURE [App::DocumentObjectGroupPython] C_element076  label="C_element : 0.072"  # scripted group (container) (typed FeaturePython)
  n = 0.072261
FEATURE [App::DocumentObjectGroupPython] N_element035  label="N_element : 0.019"  # scripted group (container) (typed FeaturePython)
  n = 0.01932
FEATURE [App::DocumentObjectGroupPython] O_element075  label="O_element : 0.066"  # scripted group (container) (typed FeaturePython)
  n = 0.066101
FEATURE [App::DocumentObjectGroupPython] S_element019  label="S_element : 0.020"  # scripted group (container) (typed FeaturePython)
  n = 0.00189
FEATURE [App::DocumentObjectGroupPython] Br_element004  label="Br_element : 0.349"  # scripted group (container) (typed FeaturePython)
  n = 0.349103
FEATURE [App::DocumentObjectGroupPython] Ag_element001  label="Ag_element : 0.474"  # scripted group (container) (typed FeaturePython)
  n = 0.474105
FEATURE [App::DocumentObjectGroupPython] I_element005  label="I_element : 0.003"  # scripted group (container) (typed FeaturePython)
  n = 0.00312
FEATURE [App::DocumentObjectGroupPython] G4_PHOTO_EMULSION  # scripted group (container) (typed FeaturePython)
  Dunit = g/cm3
  Dvalue = 3.815
  Group = -> [H_element070,C_element076,N_element035,O_element075,S_element019,Br_element004,Ag_element001,I_element005]
  conduct = 2
  density = 1
  expand = 3
  formula = G4_PHOTO_EMULSION
  name = G4_PHOTO_EMULSION
  specific = 4
FEATURE [App::DocumentObjectGroupPython] C_element077  label="C_element : 9"  # scripted group (container) (typed FeaturePython)
  n = 9
  ref = C_element
FEATURE [App::DocumentObjectGroupPython] H_element071  label="H_element : 033"  # scripted group (container) (typed FeaturePython)
  n = 10
  ref = H_element
FEATURE [App::DocumentObjectGroupPython] G4_PLASTIC_SC_VINYLTOLUENE  # scripted group (container) (typed FeaturePython)
  Dunit = g/cm3
  Dvalue = 1.032
  Group = -> [C_element077,H_element071]
  conduct = 2
  density = 1
  expand = 3
  formula = G4_PLASTIC_SC_VINYLTOLUENE
  name = G4_PLASTIC_SC_VINYLTOLUENE
  specific = 4
FEATURE [App::DocumentObjectGroupPython] Pu_element001  label="Pu_element : 1"  # scripted group (container) (typed FeaturePython)
  n = 1
  ref = Pu_element
FEATURE [App::DocumentObjectGroupPython] O_element076  label="O_element : 037"  # scripted group (container) (typed FeaturePython)
  n = 2
  ref = O_element
FEATURE [App::DocumentObjectGroupPython] G4_PLUTONIUM_DIOXIDE  # scripted group (container) (typed FeaturePython)
  Dunit = g/cm3
  Dvalue = 11.46
  Group = -> [Pu_element001,O_element076]
  conduct = 2
  density = 1
  expand = 3
  formula = G4_PLUTONIUM_DIOXIDE
  name = G4_PLUTONIUM_DIOXIDE
  specific = 4
FEATURE [App::DocumentObjectGroupPython] C_element078  label="C_element : 037"  # scripted group (container) (typed FeaturePython)
  n = 3
  ref = C_element
FEATURE [App::DocumentObjectGroupPython] H_element072  label="H_element : 034"  # scripted group (container) (typed FeaturePython)
  n = 3
  ref = H_element
FEATURE [App::DocumentObjectGroupPython] N_element036  label="N_element : 015"  # scripted group (container) (typed FeaturePython)
  n = 1
  ref = N_element
FEATURE [App::DocumentObjectGroupPython] G4_POLYACRYLONITRILE  # scripted group (container) (typed FeaturePython)
  Dunit = g/cm3
  Dvalue = 1.17
  Group = -> [C_element078,H_element072,N_element036]
  conduct = 2
  density = 1
  expand = 3
  formula = G4_POLYACRYLONITRILE
  name = G4_POLYACRYLONITRILE
  specific = 4
FEATURE [App::DocumentObjectGroupPython] C_element079  label="C_element : 16"  # scripted group (container) (typed FeaturePython)
  n = 16
  ref = C_element
FEATURE [App::DocumentObjectGroupPython] H_element073  label="H_element : 035"  # scripted group (container) (typed FeaturePython)
  n = 14
  ref = H_element
FEATURE [App::DocumentObjectGroupPython] O_element077  label="O_element : 038"  # scripted group (container) (typed FeaturePython)
  n = 3
  ref = O_element
FEATURE [App::DocumentObjectGroupPython] G4_POLYCARBONATE  # scripted group (container) (typed FeaturePython)
  Dunit = g/cm3
  Dvalue = 1.2
  Group = -> [C_element079,H_element073,O_element077]
  conduct = 2
  density = 1
  expand = 3
  formula = G4_POLYCARBONATE
  name = G4_POLYCARBONATE
  specific = 4
FEATURE [App::DocumentObjectGroupPython] C_element080  label="C_element : 038"  # scripted group (container) (typed FeaturePython)
  n = 8
  ref = C_element
FEATURE [App::DocumentObjectGroupPython] H_element074  label="H_element : 036"  # scripted group (container) (typed FeaturePython)
  n = 7
  ref = H_element
FEATURE [App::DocumentObjectGroupPython] Cl_element017  label="Cl_element : 007"  # scripted group (container) (typed FeaturePython)
  n = 1
  ref = Cl_element
FEATURE [App::DocumentObjectGroupPython] G4_POLYCHLOROSTYRENE  # scripted group (container) (typed FeaturePython)
  Dunit = g/cm3
  Dvalue = 1.3
  Group = -> [C_element080,H_element074,Cl_element017]
  conduct = 2
  density = 1
  expand = 3
  formula = G4_POLYCHLOROSTYRENE
  name = G4_POLYCHLOROSTYRENE
  specific = 4
FEATURE [App::DocumentObjectGroupPython] C_element081  label="C_element : 039"  # scripted group (container) (typed FeaturePython)
  n = 1
  ref = C_element
FEATURE [App::DocumentObjectGroupPython] H_element075  label="H_element : 037"  # scripted group (container) (typed FeaturePython)
  n = 2
  ref = H_element
FEATURE [App::DocumentObjectGroupPython] G4_POLYETHYLENE  # scripted group (container) (typed FeaturePython)
  Dunit = g/cm3
  Dvalue = 0.94
  Group = -> [C_element081,H_element075]
  conduct = 2
  density = 1
  expand = 3
  formula = G4_POLYETHYLENE
  name = G4_POLYETHYLENE
  specific = 4
FEATURE [App::DocumentObjectGroupPython] C_element082  label="C_element : 040"  # scripted group (container) (typed FeaturePython)
  n = 10
  ref = C_element
FEATURE [App::DocumentObjectGroupPython] H_element076  label="H_element : 038"  # scripted group (container) (typed FeaturePython)
  n = 8
  ref = H_element
FEATURE [App::DocumentObjectGroupPython] O_element078  label="O_element : 039"  # scripted group (container) (typed FeaturePython)
  n = 4
  ref = O_element
FEATURE [App::DocumentObjectGroupPython] G4_MYLAR  # scripted group (container) (typed FeaturePython)
  Dunit = g/cm3
  Dvalue = 1.4
  Group = -> [C_element082,H_element076,O_element078]
  conduct = 2
  density = 1
  expand = 3
  formula = G4_MYLAR
  name = G4_MYLAR
  specific = 4
FEATURE [App::DocumentObjectGroupPython] C_element083  label="C_element : 041"  # scripted group (container) (typed FeaturePython)
  n = 5
  ref = C_element
FEATURE [App::DocumentObjectGroupPython] H_element077  label="H_element : 039"  # scripted group (container) (typed FeaturePython)
  n = 8
  ref = H_element
FEATURE [App::DocumentObjectGroupPython] O_element079  label="O_element : 040"  # scripted group (container) (typed FeaturePython)
  n = 2
  ref = O_element
FEATURE [App::DocumentObjectGroupPython] G4_PLEXIGLASS  # scripted group (container) (typed FeaturePython)
  Dunit = g/cm3
  Dvalue = 1.19
  Group = -> [C_element083,H_element077,O_element079]
  conduct = 2
  density = 1
  expand = 3
  formula = G4_PLEXIGLASS
  name = G4_PLEXIGLASS
  specific = 4
FEATURE [App::DocumentObjectGroupPython] C_element084  label="C_element : 042"  # scripted group (container) (typed FeaturePython)
  n = 1
  ref = C_element
FEATURE [App::DocumentObjectGroupPython] H_element078  label="H_element : 040"  # scripted group (container) (typed FeaturePython)
  n = 2
  ref = H_element
FEATURE [App::DocumentObjectGroupPython] O_element080  label="O_element : 041"  # scripted group (container) (typed FeaturePython)
  n = 1
  ref = O_element
FEATURE [App::DocumentObjectGroupPython] G4_POLYOXYMETHYLENE  # scripted group (container) (typed FeaturePython)
  Dunit = g/cm3
  Dvalue = 1.425
  Group = -> [C_element084,H_element078,O_element080]
  conduct = 2
  density = 1
  expand = 3
  formula = G4_POLYOXYMETHYLENE
  name = G4_POLYOXYMETHYLENE
  specific = 4
FEATURE [App::DocumentObjectGroupPython] C_element085  label="C_element : 043"  # scripted group (container) (typed FeaturePython)
  n = 2
  ref = C_element
FEATURE [App::DocumentObjectGroupPython] H_element079  label="H_element : 041"  # scripted group (container) (typed FeaturePython)
  n = 4
  ref = H_element
FEATURE [App::DocumentObjectGroupPython] G4_POLYPROPYLENE  # scripted group (container) (typed FeaturePython)
  Dunit = g/cm3
  Dvalue = 0.9
  Group = -> [C_element085,H_element079]
  conduct = 2
  density = 1
  expand = 3
  formula = G4_POLYPROPYLENE
  name = G4_POLYPROPYLENE
  specific = 4
FEATURE [App::DocumentObjectGroupPython] C_element086  label="C_element : 044"  # scripted group (container) (typed FeaturePython)
  n = 8
  ref = C_element
FEATURE [App::DocumentObjectGroupPython] H_element080  label="H_element : 042"  # scripted group (container) (typed FeaturePython)
  n = 8
  ref = H_element
FEATURE [App::DocumentObjectGroupPython] G4_POLYSTYRENE  # scripted group (container) (typed FeaturePython)
  Dunit = g/cm3
  Dvalue = 1.06
  Group = -> [C_element086,H_element080]
  conduct = 2
  density = 1
  expand = 3
  formula = G4_POLYSTYRENE
  name = G4_POLYSTYRENE
  specific = 4
FEATURE [App::DocumentObjectGroupPython] C_element087  label="C_element : 045"  # scripted group (container) (typed FeaturePython)
  n = 2
  ref = C_element
FEATURE [App::DocumentObjectGroupPython] F_element014  label="F_element : 4"  # scripted group (container) (typed FeaturePython)
  n = 4
  ref = F_element
FEATURE [App::DocumentObjectGroupPython] G4_TEFLON  # scripted group (container) (typed FeaturePython)
  Dunit = g/cm3
  Dvalue = 2.2
  Group = -> [C_element087,F_element014]
  conduct = 2
  density = 1
  expand = 3
  formula = G4_TEFLON
  name = G4_TEFLON
  specific = 4
FEATURE [App::DocumentObjectGroupPython] C_element088  label="C_element : 046"  # scripted group (container) (typed FeaturePython)
  n = 2
  ref = C_element
FEATURE [App::DocumentObjectGroupPython] F_element015  label="F_element : 006"  # scripted group (container) (typed FeaturePython)
  n = 3
  ref = F_element
FEATURE [App::DocumentObjectGroupPython] Cl_element018  label="Cl_element : 008"  # scripted group (container) (typed FeaturePython)
  n = 1
  ref = Cl_element
FEATURE [App::DocumentObjectGroupPython] G4_POLYTRIFLUOROCHLOROETHYLENE  # scripted group (container) (typed FeaturePython)
  Dunit = g/cm3
  Dvalue = 2.1
  Group = -> [C_element088,F_element015,Cl_element018]
  conduct = 2
  density = 1
  expand = 3
  formula = G4_POLYTRIFLUOROCHLOROETHYLENE
  name = G4_POLYTRIFLUOROCHLOROETHYLENE
  specific = 4
FEATURE [App::DocumentObjectGroupPython] C_element089  label="C_element : 047"  # scripted group (container) (typed FeaturePython)
  n = 4
  ref = C_element
FEATURE [App::DocumentObjectGroupPython] H_element081  label="H_element : 043"  # scripted group (container) (typed FeaturePython)
  n = 6
  ref = H_element
FEATURE [App::DocumentObjectGroupPython] O_element081  label="O_element : 042"  # scripted group (container) (typed FeaturePython)
  n = 2
  ref = O_element
FEATURE [App::DocumentObjectGroupPython] G4_POLYVINYL_ACETATE  # scripted group (container) (typed FeaturePython)
  Dunit = g/cm3
  Dvalue = 1.19
  Group = -> [C_element089,H_element081,O_element081]
  conduct = 2
  density = 1
  expand = 3
  formula = G4_POLYVINYL_ACETATE
  name = G4_POLYVINYL_ACETATE
  specific = 4
FEATURE [App::DocumentObjectGroupPython] C_element090  label="C_element : 048"  # scripted group (container) (typed FeaturePython)
  n = 2
  ref = C_element
FEATURE [App::DocumentObjectGroupPython] H_element082  label="H_element : 044"  # scripted group (container) (typed FeaturePython)
  n = 4
  ref = H_element
FEATURE [App::DocumentObjectGroupPython] O_element082  label="O_element : 043"  # scripted group (container) (typed FeaturePython)
  n = 1
  ref = O_element
FEATURE [App::DocumentObjectGroupPython] G4_POLYVINYL_ALCOHOL  # scripted group (container) (typed FeaturePython)
  Dunit = g/cm3
  Dvalue = 1.3
  Group = -> [C_element090,H_element082,O_element082]
  conduct = 2
  density = 1
  expand = 3
  formula = G4_POLYVINYL_ALCOHOL
  name = G4_POLYVINYL_ALCOHOL
  specific = 4
FEATURE [App::DocumentObjectGroupPython] C_element091  label="C_element : 049"  # scripted group (container) (typed FeaturePython)
  n = 8
  ref = C_element
FEATURE [App::DocumentObjectGroupPython] H_element083  label="H_element : 045"  # scripted group (container) (typed FeaturePython)
  n = 14
  ref = H_element
FEATURE [App::DocumentObjectGroupPython] O_element083  label="O_element : 044"  # scripted group (container) (typed FeaturePython)
  n = 2
  ref = O_element
FEATURE [App::DocumentObjectGroupPython] G4_POLYVINYL_BUTYRAL  # scripted group (container) (typed FeaturePython)
  Dunit = g/cm3
  Dvalue = 1.12
  Group = -> [C_element091,H_element083,O_element083]
  conduct = 2
  density = 1
  expand = 3
  formula = G4_POLYVINYL_BUTYRAL
  name = G4_POLYVINYL_BUTYRAL
  specific = 4
FEATURE [App::DocumentObjectGroupPython] C_element092  label="C_element : 050"  # scripted group (container) (typed FeaturePython)
  n = 2
  ref = C_element
FEATURE [App::DocumentObjectGroupPython] H_element084  label="H_element : 046"  # scripted group (container) (typed FeaturePython)
  n = 3
  ref = H_element
FEATURE [App::DocumentObjectGroupPython] Cl_element019  label="Cl_element : 009"  # scripted group (container) (typed FeaturePython)
  n = 1
  ref = Cl_element
FEATURE [App::DocumentObjectGroupPython] G4_POLYVINYL_CHLORIDE  # scripted group (container) (typed FeaturePython)
  Dunit = g/cm3
  Dvalue = 1.3
  Group = -> [C_element092,H_element084,Cl_element019]
  conduct = 2
  density = 1
  expand = 3
  formula = G4_POLYVINYL_CHLORIDE
  name = G4_POLYVINYL_CHLORIDE
  specific = 4
FEATURE [App::DocumentObjectGroupPython] C_element093  label="C_element : 051"  # scripted group (container) (typed FeaturePython)
  n = 2
  ref = C_element
FEATURE [App::DocumentObjectGroupPython] H_element085  label="H_element : 047"  # scripted group (container) (typed FeaturePython)
  n = 2
  ref = H_element
FEATURE [App::DocumentObjectGroupPython] Cl_element020  label="Cl_element : 010"  # scripted group (container) (typed FeaturePython)
  n = 2
  ref = Cl_element
FEATURE [App::DocumentObjectGroupPython] G4_POLYVINYLIDENE_CHLORIDE  # scripted group (container) (typed FeaturePython)
  Dunit = g/cm3
  Dvalue = 1.7
  Group = -> [C_element093,H_element085,Cl_element020]
  conduct = 2
  density = 1
  expand = 3
  formula = G4_POLYVINYLIDENE_CHLORIDE
  name = G4_POLYVINYLIDENE_CHLORIDE
  specific = 4
FEATURE [App::DocumentObjectGroupPython] C_element094  label="C_element : 052"  # scripted group (container) (typed FeaturePython)
  n = 2
  ref = C_element
FEATURE [App::DocumentObjectGroupPython] H_element086  label="H_element : 048"  # scripted group (container) (typed FeaturePython)
  n = 2
  ref = H_element
FEATURE [App::DocumentObjectGroupPython] F_element016  label="F_element : 007"  # scripted group (container) (typed FeaturePython)
  n = 2
  ref = F_element
FEATURE [App::DocumentObjectGroupPython] G4_POLYVINYLIDENE_FLUORIDE  # scripted group (container) (typed FeaturePython)
  Dunit = g/cm3
  Dvalue = 1.76
  Group = -> [C_element094,H_element086,F_element016]
  conduct = 2
  density = 1
  expand = 3
  formula = G4_POLYVINYLIDENE_FLUORIDE
  name = G4_POLYVINYLIDENE_FLUORIDE
  specific = 4
FEATURE [App::DocumentObjectGroupPython] C_element095  label="C_element : 053"  # scripted group (container) (typed FeaturePython)
  n = 6
  ref = C_element
FEATURE [App::DocumentObjectGroupPython] H_element087  label="H_element : 9"  # scripted group (container) (typed FeaturePython)
  n = 9
  ref = H_element
FEATURE [App::DocumentObjectGroupPython] N_element037  label="N_element : 016"  # scripted group (container) (typed FeaturePython)
  n = 1
  ref = N_element
FEATURE [App::DocumentObjectGroupPython] O_element084  label="O_element : 045"  # scripted group (container) (typed FeaturePython)
  n = 1
  ref = O_element
FEATURE [App::DocumentObjectGroupPython] G4_POLYVINYL_PYRROLIDONE  # scripted group (container) (typed FeaturePython)
  Dunit = g/cm3
  Dvalue = 1.25
  Group = -> [C_element095,H_element087,N_element037,O_element084]
  conduct = 2
  density = 1
  expand = 3
  formula = G4_POLYVINYL_PYRROLIDONE
  name = G4_POLYVINYL_PYRROLIDONE
  specific = 4
FEATURE [App::DocumentObjectGroupPython] K_element008  label="K_element : 1"  # scripted group (container) (typed FeaturePython)
  n = 1
  ref = K_element
FEATURE [App::DocumentObjectGroupPython] I_element006  label="I_element : 003"  # scripted group (container) (typed FeaturePython)
  n = 1
  ref = I_element
FEATURE [App::DocumentObjectGroupPython] G4_POTASSIUM_IODIDE  # scripted group (container) (typed FeaturePython)
  Dunit = g/cm3
  Dvalue = 3.13
  Group = -> [K_element008,I_element006]
  conduct = 2
  density = 1
  expand = 3
  formula = G4_POTASSIUM_IODIDE
  name = G4_POTASSIUM_IODIDE
  specific = 4
FEATURE [App::DocumentObjectGroupPython] K_element009  label="K_element : 2"  # scripted group (container) (typed FeaturePython)
  n = 2
  ref = K_element
FEATURE [App::DocumentObjectGroupPython] O_element085  label="O_element : 046"  # scripted group (container) (typed FeaturePython)
  n = 1
  ref = O_element
FEATURE [App::DocumentObjectGroupPython] G4_POTASSIUM_OXIDE  # scripted group (container) (typed FeaturePython)
  Dunit = g/cm3
  Dvalue = 2.32
  Group = -> [K_element009,O_element085]
  conduct = 2
  density = 1
  expand = 3
  formula = G4_POTASSIUM_OXIDE
  name = G4_POTASSIUM_OXIDE
  specific = 4
FEATURE [App::DocumentObjectGroupPython] C_element096  label="C_element : 054"  # scripted group (container) (typed FeaturePython)
  n = 3
  ref = C_element
FEATURE [App::DocumentObjectGroupPython] H_element088  label="H_element : 049"  # scripted group (container) (typed FeaturePython)
  n = 8
  ref = H_element
FEATURE [App::DocumentObjectGroupPython] G4_PROPANE  # scripted group (container) (typed FeaturePython)
  Dunit = g/cm3
  Dvalue = 0.00187939
  Group = -> [C_element096,H_element088]
  conduct = 2
  density = 1
  expand = 3
  formula = G4_PROPANE
  name = G4_PROPANE
  specific = 4
FEATURE [App::DocumentObjectGroupPython] C_element097  label="C_element : 055"  # scripted group (container) (typed FeaturePython)
  n = 3
  ref = C_element
FEATURE [App::DocumentObjectGroupPython] H_element089  label="H_element : 050"  # scripted group (container) (typed FeaturePython)
  n = 8
  ref = H_element
FEATURE [App::DocumentObjectGroupPython] G4_lPROPANE  # scripted group (container) (typed FeaturePython)
  Dunit = g/cm3
  Dvalue = 0.43
  Group = -> [C_element097,H_element089]
  conduct = 2
  density = 1
  expand = 3
  formula = G4_lPROPANE
  name = G4_lPROPANE
  specific = 4
FEATURE [App::DocumentObjectGroupPython] C_element098  label="C_element : 056"  # scripted group (container) (typed FeaturePython)
  n = 3
  ref = C_element
FEATURE [App::DocumentObjectGroupPython] H_element090  label="H_element : 051"  # scripted group (container) (typed FeaturePython)
  n = 8
  ref = H_element
FEATURE [App::DocumentObjectGroupPython] O_element086  label="O_element : 047"  # scripted group (container) (typed FeaturePython)
  n = 1
  ref = O_element
FEATURE [App::DocumentObjectGroupPython] G4_N_PROPYL_ALCOHOL  label="G4_N-PROPYL_ALCOHOL"  # scripted group (container) (typed FeaturePython)
  Dunit = g/cm3
  Dvalue = 0.8035
  Group = -> [C_element098,H_element090,O_element086]
  conduct = 2
  density = 1
  expand = 3
  formula = G4_N-PROPYL_ALCOHOL
  name = G4_N-PROPYL_ALCOHOL
  specific = 4
FEATURE [App::DocumentObjectGroupPython] C_element099  label="C_element : 057"  # scripted group (container) (typed FeaturePython)
  n = 5
  ref = C_element
FEATURE [App::DocumentObjectGroupPython] H_element091  label="H_element : 052"  # scripted group (container) (typed FeaturePython)
  n = 5
  ref = H_element
FEATURE [App::DocumentObjectGroupPython] N_element038  label="N_element : 017"  # scripted group (container) (typed FeaturePython)
  n = 1
  ref = N_element
FEATURE [App::DocumentObjectGroupPython] G4_PYRIDINE  # scripted group (container) (typed FeaturePython)
  Dunit = g/cm3
  Dvalue = 0.9819
  Group = -> [C_element099,H_element091,N_element038]
  conduct = 2
  density = 1
  expand = 3
  formula = G4_PYRIDINE
  name = G4_PYRIDINE
  specific = 4
FEATURE [App::DocumentObjectGroupPython] H_element092  label="H_element : 0.144"  # scripted group (container) (typed FeaturePython)
  n = 0.143711
FEATURE [App::DocumentObjectGroupPython] C_element100  label="C_element : 0.856"  # scripted group (container) (typed FeaturePython)
  n = 0.856289
FEATURE [App::DocumentObjectGroupPython] G4_RUBBER_BUTYL  # scripted group (container) (typed FeaturePython)
  Dunit = g/cm3
  Dvalue = 0.92
  Group = -> [H_element092,C_element100]
  conduct = 2
  density = 1
  expand = 3
  formula = G4_RUBBER_BUTYL
  name = G4_RUBBER_BUTYL
  specific = 4
FEATURE [App::DocumentObjectGroupPython] H_element093  label="H_element : 0.118"  # scripted group (container) (typed FeaturePython)
  n = 0.118371
FEATURE [App::DocumentObjectGroupPython] C_element101  label="C_element : 0.882"  # scripted group (container) (typed FeaturePython)
  n = 0.881629
FEATURE [App::DocumentObjectGroupPython] G4_RUBBER_NATURAL  # scripted group (container) (typed FeaturePython)
  Dunit = g/cm3
  Dvalue = 0.92
  Group = -> [H_element093,C_element101]
  conduct = 2
  density = 1
  expand = 3
  formula = G4_RUBBER_NATURAL
  name = G4_RUBBER_NATURAL
  specific = 4
FEATURE [App::DocumentObjectGroupPython] H_element094  label="H_element : 0.145"  # scripted group (container) (typed FeaturePython)
  n = 0.05692
FEATURE [App::DocumentObjectGroupPython] C_element102  label="C_element : 0.543"  # scripted group (container) (typed FeaturePython)
  n = 0.542646
FEATURE [App::DocumentObjectGroupPython] Cl_element021  label="Cl_element : 0.400"  # scripted group (container) (typed FeaturePython)
  n = 0.400434
FEATURE [App::DocumentObjectGroupPython] G4_RUBBER_NEOPRENE  # scripted group (container) (typed FeaturePython)
  Dunit = g/cm3
  Dvalue = 1.23
  Group = -> [H_element094,C_element102,Cl_element021]
  conduct = 2
  density = 1
  expand = 3
  formula = G4_RUBBER_NEOPRENE
  name = G4_RUBBER_NEOPRENE
  specific = 4
FEATURE [App::DocumentObjectGroupPython] Si_element006  label="Si_element : 1"  # scripted group (container) (typed FeaturePython)
  n = 1
  ref = Si_element
FEATURE [App::DocumentObjectGroupPython] O_element087  label="O_element : 048"  # scripted group (container) (typed FeaturePython)
  n = 2
  ref = O_element
FEATURE [App::DocumentObjectGroupPython] G4_SILICON_DIOXIDE  # scripted group (container) (typed FeaturePython)
  Dunit = g/cm3
  Dvalue = 2.32
  Group = -> [Si_element006,O_element087]
  conduct = 2
  density = 1
  expand = 3
  formula = G4_SILICON_DIOXIDE
  name = G4_SILICON_DIOXIDE
  specific = 4
FEATURE [App::DocumentObjectGroupPython] Ag_element002  label="Ag_element : 1"  # scripted group (container) (typed FeaturePython)
  n = 1
  ref = Ag_element
FEATURE [App::DocumentObjectGroupPython] Br_element005  label="Br_element : 003"  # scripted group (container) (typed FeaturePython)
  n = 1
  ref = Br_element
FEATURE [App::DocumentObjectGroupPython] G4_SILVER_BROMIDE  # scripted group (container) (typed FeaturePython)
  Dunit = g/cm3
  Dvalue = 6.473
  Group = -> [Ag_element002,Br_element005]
  conduct = 2
  density = 1
  expand = 3
  formula = G4_SILVER_BROMIDE
  name = G4_SILVER_BROMIDE
  specific = 4
FEATURE [App::DocumentObjectGroupPython] Ag_element003  label="Ag_element : 002"  # scripted group (container) (typed FeaturePython)
  n = 1
  ref = Ag_element
FEATURE [App::DocumentObjectGroupPython] Cl_element022  label="Cl_element : 011"  # scripted group (container) (typed FeaturePython)
  n = 1
  ref = Cl_element
FEATURE [App::DocumentObjectGroupPython] G4_SILVER_CHLORIDE  # scripted group (container) (typed FeaturePython)
  Dunit = g/cm3
  Dvalue = 5.56
  Group = -> [Ag_element003,Cl_element022]
  conduct = 2
  density = 1
  expand = 3
  formula = G4_SILVER_CHLORIDE
  name = G4_SILVER_CHLORIDE
  specific = 4
FEATURE [App::DocumentObjectGroupPython] Br_element006  label="Br_element : 0.423"  # scripted group (container) (typed FeaturePython)
  n = 0.422895
FEATURE [App::DocumentObjectGroupPython] Ag_element004  label="Ag_element : 0.574"  # scripted group (container) (typed FeaturePython)
  n = 0.573748
FEATURE [App::DocumentObjectGroupPython] I_element007  label="I_element : 0.649"  # scripted group (container) (typed FeaturePython)
  n = 0.003357
FEATURE [App::DocumentObjectGroupPython] G4_SILVER_HALIDES  # scripted group (container) (typed FeaturePython)
  Dunit = g/cm3
  Dvalue = 6.47
  Group = -> [Br_element006,Ag_element004,I_element007]
  conduct = 2
  density = 1
  expand = 3
  formula = G4_SILVER_HALIDES
  name = G4_SILVER_HALIDES
  specific = 4
FEATURE [App::DocumentObjectGroupPython] Ag_element005  label="Ag_element : 003"  # scripted group (container) (typed FeaturePython)
  n = 1
  ref = Ag_element
FEATURE [App::DocumentObjectGroupPython] I_element008  label="I_element : 004"  # scripted group (container) (typed FeaturePython)
  n = 1
  ref = I_element
FEATURE [App::DocumentObjectGroupPython] G4_SILVER_IODIDE  # scripted group (container) (typed FeaturePython)
  Dunit = g/cm3
  Dvalue = 6.01
  Group = -> [Ag_element005,I_element008]
  conduct = 2
  density = 1
  expand = 3
  formula = G4_SILVER_IODIDE
  name = G4_SILVER_IODIDE
  specific = 4
FEATURE [App::DocumentObjectGroupPython] H_element095  label="H_element : 0.100"  # scripted group (container) (typed FeaturePython)
  n = 0.1
FEATURE [App::DocumentObjectGroupPython] C_element103  label="C_element : 0.204"  # scripted group (container) (typed FeaturePython)
  n = 0.204
FEATURE [App::DocumentObjectGroupPython] N_element039  label="N_element : 0.759"  # scripted group (container) (typed FeaturePython)
  n = 0.042
FEATURE [App::DocumentObjectGroupPython] O_element088  label="O_element : 0.645"  # scripted group (container) (typed FeaturePython)
  n = 0.645
FEATURE [App::DocumentObjectGroupPython] Na_element013  label="Na_element : 0.100"  # scripted group (container) (typed FeaturePython)
  n = 0.002
FEATURE [App::DocumentObjectGroupPython] P_element009  label="P_element : 0.107"  # scripted group (container) (typed FeaturePython)
  n = 0.001
FEATURE [App::DocumentObjectGroupPython] S_element020  label="S_element : 0.021"  # scripted group (container) (typed FeaturePython)
  n = 0.002
FEATURE [App::DocumentObjectGroupPython] Cl_element023  label="Cl_element : 0.590"  # scripted group (container) (typed FeaturePython)
  n = 0.003
FEATURE [App::DocumentObjectGroupPython] K_element010  label="K_element : 0.001"  # scripted group (container) (typed FeaturePython)
  n = 0.001
FEATURE [App::DocumentObjectGroupPython] G4_SKIN_ICRP  # scripted group (container) (typed FeaturePython)
  Dunit = g/cm3
  Dvalue = 1.09
  Group = -> [H_element095,C_element103,N_element039,O_element088,Na_element013,P_element009,S_element020,Cl_element023,K_element010]
  conduct = 2
  density = 1
  expand = 3
  formula = G4_SKIN_ICRP
  name = G4_SKIN_ICRP
  specific = 4
FEATURE [App::DocumentObjectGroupPython] Na_element014  label="Na_element : 2"  # scripted group (container) (typed FeaturePython)
  n = 2
  ref = Na_element
FEATURE [App::DocumentObjectGroupPython] C_element104  label="C_element : 058"  # scripted group (container) (typed FeaturePython)
  n = 1
  ref = C_element
FEATURE [App::DocumentObjectGroupPython] O_element089  label="O_element : 049"  # scripted group (container) (typed FeaturePython)
  n = 3
  ref = O_element
FEATURE [App::DocumentObjectGroupPython] G4_SODIUM_CARBONATE  # scripted group (container) (typed FeaturePython)
  Dunit = g/cm3
  Dvalue = 2.532
  Group = -> [Na_element014,C_element104,O_element089]
  conduct = 2
  density = 1
  expand = 3
  formula = G4_SODIUM_CARBONATE
  name = G4_SODIUM_CARBONATE
  specific = 4
FEATURE [App::DocumentObjectGroupPython] Na_element015  label="Na_element : 1"  # scripted group (container) (typed FeaturePython)
  n = 1
  ref = Na_element
FEATURE [App::DocumentObjectGroupPython] I_element009  label="I_element : 005"  # scripted group (container) (typed FeaturePython)
  n = 1
  ref = I_element
FEATURE [App::DocumentObjectGroupPython] G4_SODIUM_IODIDE  # scripted group (container) (typed FeaturePython)
  Dunit = g/cm3
  Dvalue = 3.667
  Group = -> [Na_element015,I_element009]
  conduct = 2
  density = 1
  expand = 3
  formula = G4_SODIUM_IODIDE
  name = G4_SODIUM_IODIDE
  specific = 4
FEATURE [App::DocumentObjectGroupPython] Na_element016  label="Na_element : 003"  # scripted group (container) (typed FeaturePython)
  n = 2
  ref = Na_element
FEATURE [App::DocumentObjectGroupPython] O_element090  label="O_element : 050"  # scripted group (container) (typed FeaturePython)
  n = 1
  ref = O_element
FEATURE [App::DocumentObjectGroupPython] G4_SODIUM_MONOXIDE  # scripted group (container) (typed FeaturePython)
  Dunit = g/cm3
  Dvalue = 2.27
  Group = -> [Na_element016,O_element090]
  conduct = 2
  density = 1
  expand = 3
  formula = G4_SODIUM_MONOXIDE
  name = G4_SODIUM_MONOXIDE
  specific = 4
FEATURE [App::DocumentObjectGroupPython] Na_element017  label="Na_element : 004"  # scripted group (container) (typed FeaturePython)
  n = 1
  ref = Na_element
FEATURE [App::DocumentObjectGroupPython] N_element040  label="N_element : 018"  # scripted group (container) (typed FeaturePython)
  n = 1
  ref = N_element
FEATURE [App::DocumentObjectGroupPython] O_element091  label="O_element : 051"  # scripted group (container) (typed FeaturePython)
  n = 3
  ref = O_element
FEATURE [App::DocumentObjectGroupPython] G4_SODIUM_NITRATE  # scripted group (container) (typed FeaturePython)
  Dunit = g/cm3
  Dvalue = 2.261
  Group = -> [Na_element017,N_element040,O_element091]
  conduct = 2
  density = 1
  expand = 3
  formula = G4_SODIUM_NITRATE
  name = G4_SODIUM_NITRATE
  specific = 4
FEATURE [App::DocumentObjectGroupPython] C_element105  label="C_element : 059"  # scripted group (container) (typed FeaturePython)
  n = 14
  ref = C_element
FEATURE [App::DocumentObjectGroupPython] H_element096  label="H_element : 053"  # scripted group (container) (typed FeaturePython)
  n = 12
  ref = H_element
FEATURE [App::DocumentObjectGroupPython] G4_STILBENE  # scripted group (container) (typed FeaturePython)
  Dunit = g/cm3
  Dvalue = 0.9707
  Group = -> [C_element105,H_element096]
  conduct = 2
  density = 1
  expand = 3
  formula = G4_STILBENE
  name = G4_STILBENE
  specific = 4
FEATURE [App::DocumentObjectGroupPython] C_element106  label="C_element : 12"  # scripted group (container) (typed FeaturePython)
  n = 12
  ref = C_element
FEATURE [App::DocumentObjectGroupPython] H_element097  label="H_element : 22"  # scripted group (container) (typed FeaturePython)
  n = 22
  ref = H_element
FEATURE [App::DocumentObjectGroupPython] O_element092  label="O_element : 11"  # scripted group (container) (typed FeaturePython)
  n = 11
  ref = O_element
FEATURE [App::DocumentObjectGroupPython] G4_SUCROSE  # scripted group (container) (typed FeaturePython)
  Dunit = g/cm3
  Dvalue = 1.5805
  Group = -> [C_element106,H_element097,O_element092]
  conduct = 2
  density = 1
  expand = 3
  formula = G4_SUCROSE
  name = G4_SUCROSE
  specific = 4
FEATURE [App::DocumentObjectGroupPython] C_element107  label="C_element : 18"  # scripted group (container) (typed FeaturePython)
  n = 18
  ref = C_element
FEATURE [App::DocumentObjectGroupPython] H_element098  label="H_element : 054"  # scripted group (container) (typed FeaturePython)
  n = 14
  ref = H_element
FEATURE [App::DocumentObjectGroupPython] G4_TERPHENYL  # scripted group (container) (typed FeaturePython)
  Dunit = g/cm3
  Dvalue = 1.24
  Group = -> [C_element107,H_element098]
  conduct = 2
  density = 1
  expand = 3
  formula = G4_TERPHENYL
  name = G4_TERPHENYL
  specific = 4
FEATURE [App::DocumentObjectGroupPython] H_element099  label="H_element : 0.146"  # scripted group (container) (typed FeaturePython)
  n = 0.106
FEATURE [App::DocumentObjectGroupPython] C_element108  label="C_element : 0.883"  # scripted group (container) (typed FeaturePython)
  n = 0.099
FEATURE [App::DocumentObjectGroupPython] N_element041  label="N_element : 0.020"  # scripted group (container) (typed FeaturePython)
  n = 0.02
FEATURE [App::DocumentObjectGroupPython] O_element093  label="O_element : 0.766"  # scripted group (container) (typed FeaturePython)
  n = 0.766
FEATURE [App::DocumentObjectGroupPython] Na_element018  label="Na_element : 0.101"  # scripted group (container) (typed FeaturePython)
  n = 0.002
FEATURE [App::DocumentObjectGroupPython] P_element010  label="P_element : 0.108"  # scripted group (container) (typed FeaturePython)
  n = 0.001
FEATURE [App::DocumentObjectGroupPython] S_element021  label="S_element : 0.022"  # scripted group (container) (typed FeaturePython)
  n = 0.002
FEATURE [App::DocumentObjectGroupPython] Cl_element024  label="Cl_element : 0.002"  # scripted group (container) (typed FeaturePython)
  n = 0.002
FEATURE [App::DocumentObjectGroupPython] K_element011  label="K_element : 0.017"  # scripted group (container) (typed FeaturePython)
  n = 0.002
FEATURE [App::DocumentObjectGroupPython] G4_TESTIS_ICRP  # scripted group (container) (typed FeaturePython)
  Dunit = g/cm3
  Dvalue = 1.04
  Group = -> [H_element099,C_element108,N_element041,O_element093,Na_element018,P_element010,S_element021,Cl_element024,K_element011]
  conduct = 2
  density = 1
  expand = 3
  formula = G4_TESTIS_ICRP
  name = G4_TESTIS_ICRP
  specific = 4
FEATURE [App::DocumentObjectGroupPython] C_element109  label="C_element : 060"  # scripted group (container) (typed FeaturePython)
  n = 2
  ref = C_element
FEATURE [App::DocumentObjectGroupPython] Cl_element025  label="Cl_element : 012"  # scripted group (container) (typed FeaturePython)
  n = 4
  ref = Cl_element
FEATURE [App::DocumentObjectGroupPython] G4_TETRACHLOROETHYLENE  # scripted group (container) (typed FeaturePython)
  Dunit = g/cm3
  Dvalue = 1.625
  Group = -> [C_element109,Cl_element025]
  conduct = 2
  density = 1
  expand = 3
  formula = G4_TETRACHLOROETHYLENE
  name = G4_TETRACHLOROETHYLENE
  specific = 4
FEATURE [App::DocumentObjectGroupPython] Tl_element001  label="Tl_element : 1"  # scripted group (container) (typed FeaturePython)
  n = 1
  ref = Tl_element
FEATURE [App::DocumentObjectGroupPython] Cl_element026  label="Cl_element : 013"  # scripted group (container) (typed FeaturePython)
  n = 1
  ref = Cl_element
FEATURE [App::DocumentObjectGroupPython] G4_THALLIUM_CHLORIDE  # scripted group (container) (typed FeaturePython)
  Dunit = g/cm3
  Dvalue = 7.004
  Group = -> [Tl_element001,Cl_element026]
  conduct = 2
  density = 1
  expand = 3
  formula = G4_THALLIUM_CHLORIDE
  name = G4_THALLIUM_CHLORIDE
  specific = 4
FEATURE [App::DocumentObjectGroupPython] H_element100  label="H_element : 0.147"  # scripted group (container) (typed FeaturePython)
  n = 0.105
FEATURE [App::DocumentObjectGroupPython] C_element110  label="C_element : 0.256"  # scripted group (container) (typed FeaturePython)
  n = 0.256
FEATURE [App::DocumentObjectGroupPython] N_element042  label="N_element : 0.760"  # scripted group (container) (typed FeaturePython)
  n = 0.027
FEATURE [App::DocumentObjectGroupPython] O_element094  label="O_element : 0.602"  # scripted group (container) (typed FeaturePython)
  n = 0.602
FEATURE [App::DocumentObjectGroupPython] Na_element019  label="Na_element : 0.102"  # scripted group (container) (typed FeaturePython)
  n = 0.001
FEATURE [App::DocumentObjectGroupPython] P_element011  label="P_element : 0.109"  # scripted group (container) (typed FeaturePython)
  n = 0.002
FEATURE [App::DocumentObjectGroupPython] S_element022  label="S_element : 0.023"  # scripted group (container) (typed FeaturePython)
  n = 0.003
FEATURE [App::DocumentObjectGroupPython] Cl_element027  label="Cl_element : 0.591"  # scripted group (container) (typed FeaturePython)
  n = 0.002
FEATURE [App::DocumentObjectGroupPython] K_element012  label="K_element : 0.018"  # scripted group (container) (typed FeaturePython)
  n = 0.002
FEATURE [App::DocumentObjectGroupPython] G4_TISSUE_SOFT_ICRP  # scripted group (container) (typed FeaturePython)
  Dunit = g/cm3
  Dvalue = 1.03
  Group = -> [H_element100,C_element110,N_element042,O_element094,Na_element019,P_element011,S_element022,Cl_element027,K_element012]
  conduct = 2
  density = 1
  expand = 3
  formula = G4_TISSUE_SOFT_ICRP
  name = G4_TISSUE_SOFT_ICRP
  specific = 4
FEATURE [App::DocumentObjectGroupPython] H_element101  label="H_element : 0.148"  # scripted group (container) (typed FeaturePython)
  n = 0.101
FEATURE [App::DocumentObjectGroupPython] C_element111  label="C_element : 0.111"  # scripted group (container) (typed FeaturePython)
  n = 0.111
FEATURE [App::DocumentObjectGroupPython] N_element043  label="N_element : 0.026"  # scripted group (container) (typed FeaturePython)
  n = 0.026
FEATURE [App::DocumentObjectGroupPython] O_element095  label="O_element : 0.762"  # scripted group (container) (typed FeaturePython)
  n = 0.762
FEATURE [App::DocumentObjectGroupPython] G4_TISSUE_SOFT_ICRU_4  label="G4_TISSUE_SOFT_ICRU-4"  # scripted group (container) (typed FeaturePython)
  Dunit = g/cm3
  Dvalue = 1
  Group = -> [H_element101,C_element111,N_element043,O_element095]
  conduct = 2
  density = 1
  expand = 3
  formula = G4_TISSUE_SOFT_ICRU-4
  name = G4_TISSUE_SOFT_ICRU-4
  specific = 4
FEATURE [App::DocumentObjectGroupPython] H_element102  label="H_element : 0.149"  # scripted group (container) (typed FeaturePython)
  n = 0.101869
FEATURE [App::DocumentObjectGroupPython] C_element112  label="C_element : 0.456"  # scripted group (container) (typed FeaturePython)
  n = 0.456179
FEATURE [App::DocumentObjectGroupPython] N_element044  label="N_element : 0.761"  # scripted group (container) (typed FeaturePython)
  n = 0.035172
FEATURE [App::DocumentObjectGroupPython] O_element096  label="O_element : 0.407"  # scripted group (container) (typed FeaturePython)
  n = 0.40678
FEATURE [App::DocumentObjectGroupPython] G4_TISSUE_METHANE  label="G4_TISSUE-METHANE"  # scripted group (container) (typed FeaturePython)
  Dunit = g/cm3
  Dvalue = 0.00106409
  Group = -> [H_element102,C_element112,N_element044,O_element096]
  conduct = 2
  density = 1
  expand = 3
  formula = G4_TISSUE-METHANE
  name = G4_TISSUE-METHANE
  specific = 4
FEATURE [App::DocumentObjectGroupPython] H_element103  label="H_element : 0.103"  # scripted group (container) (typed FeaturePython)
  n = 0.102672
FEATURE [App::DocumentObjectGroupPython] C_element113  label="C_element : 0.569"  # scripted group (container) (typed FeaturePython)
  n = 0.56894
FEATURE [App::DocumentObjectGroupPython] N_element045  label="N_element : 0.762"  # scripted group (container) (typed FeaturePython)
  n = 0.035022
FEATURE [App::DocumentObjectGroupPython] O_element097  label="O_element : 0.293"  # scripted group (container) (typed FeaturePython)
  n = 0.293366
FEATURE [App::DocumentObjectGroupPython] G4_TISSUE_PROPANE  label="G4_TISSUE-PROPANE"  # scripted group (container) (typed FeaturePython)
  Dunit = g/cm3
  Dvalue = 0.00182628
  Group = -> [H_element103,C_element113,N_element045,O_element097]
  conduct = 2
  density = 1
  expand = 3
  formula = G4_TISSUE-PROPANE
  name = G4_TISSUE-PROPANE
  specific = 4
FEATURE [App::DocumentObjectGroupPython] Ti_element003  label="Ti_element : 1"  # scripted group (container) (typed FeaturePython)
  n = 1
  ref = Ti_element
FEATURE [App::DocumentObjectGroupPython] O_element098  label="O_element : 052"  # scripted group (container) (typed FeaturePython)
  n = 2
  ref = O_element
FEATURE [App::DocumentObjectGroupPython] G4_TITANIUM_DIOXIDE  # scripted group (container) (typed FeaturePython)
  Dunit = g/cm3
  Dvalue = 4.26
  Group = -> [Ti_element003,O_element098]
  conduct = 2
  density = 1
  expand = 3
  formula = G4_TITANIUM_DIOXIDE
  name = G4_TITANIUM_DIOXIDE
  specific = 4
FEATURE [App::DocumentObjectGroupPython] C_element114  label="C_element : 061"  # scripted group (container) (typed FeaturePython)
  n = 7
  ref = C_element
FEATURE [App::DocumentObjectGroupPython] H_element104  label="H_element : 055"  # scripted group (container) (typed FeaturePython)
  n = 8
  ref = H_element
FEATURE [App::DocumentObjectGroupPython] G4_TOLUENE  # scripted group (container) (typed FeaturePython)
  Dunit = g/cm3
  Dvalue = 0.8669
  Group = -> [C_element114,H_element104]
  conduct = 2
  density = 1
  expand = 3
  formula = G4_TOLUENE
  name = G4_TOLUENE
  specific = 4
FEATURE [App::DocumentObjectGroupPython] C_element115  label="C_element : 062"  # scripted group (container) (typed FeaturePython)
  n = 2
  ref = C_element
FEATURE [App::DocumentObjectGroupPython] H_element105  label="H_element : 056"  # scripted group (container) (typed FeaturePython)
  n = 1
  ref = H_element
FEATURE [App::DocumentObjectGroupPython] Cl_element028  label="Cl_element : 014"  # scripted group (container) (typed FeaturePython)
  n = 3
  ref = Cl_element
FEATURE [App::DocumentObjectGroupPython] G4_TRICHLOROETHYLENE  # scripted group (container) (typed FeaturePython)
  Dunit = g/cm3
  Dvalue = 1.46
  Group = -> [C_element115,H_element105,Cl_element028]
  conduct = 2
  density = 1
  expand = 3
  formula = G4_TRICHLOROETHYLENE
  name = G4_TRICHLOROETHYLENE
  specific = 4
FEATURE [App::DocumentObjectGroupPython] C_element116  label="C_element : 063"  # scripted group (container) (typed FeaturePython)
  n = 6
  ref = C_element
FEATURE [App::DocumentObjectGroupPython] H_element106  label="H_element : 15"  # scripted group (container) (typed FeaturePython)
  n = 15
  ref = H_element
FEATURE [App::DocumentObjectGroupPython] O_element099  label="O_element : 053"  # scripted group (container) (typed FeaturePython)
  n = 4
  ref = O_element
FEATURE [App::DocumentObjectGroupPython] P_element012  label="P_element : 1"  # scripted group (container) (typed FeaturePython)
  n = 1
  ref = P_element
FEATURE [App::DocumentObjectGroupPython] G4_TRIETHYL_PHOSPHATE  # scripted group (container) (typed FeaturePython)
  Dunit = g/cm3
  Dvalue = 1.07
  Group = -> [C_element116,H_element106,O_element099,P_element012]
  conduct = 2
  density = 1
  expand = 3
  formula = G4_TRIETHYL_PHOSPHATE
  name = G4_TRIETHYL_PHOSPHATE
  specific = 4
FEATURE [App::DocumentObjectGroupPython] W_element003  label="W_element : 003"  # scripted group (container) (typed FeaturePython)
  n = 1
  ref = W_element
FEATURE [App::DocumentObjectGroupPython] F_element017  label="F_element : 6"  # scripted group (container) (typed FeaturePython)
  n = 6
  ref = F_element
FEATURE [App::DocumentObjectGroupPython] G4_TUNGSTEN_HEXAFLUORIDE  # scripted group (container) (typed FeaturePython)
  Dunit = g/cm3
  Dvalue = 2.4
  Group = -> [W_element003,F_element017]
  conduct = 2
  density = 1
  expand = 3
  formula = G4_TUNGSTEN_HEXAFLUORIDE
  name = G4_TUNGSTEN_HEXAFLUORIDE
  specific = 4
FEATURE [App::DocumentObjectGroupPython] U_element001  label="U_element : 1"  # scripted group (container) (typed FeaturePython)
  n = 1
  ref = U_element
FEATURE [App::DocumentObjectGroupPython] C_element117  label="C_element : 064"  # scripted group (container) (typed FeaturePython)
  n = 2
  ref = C_element
FEATURE [App::DocumentObjectGroupPython] G4_URANIUM_DICARBIDE  # scripted group (container) (typed FeaturePython)
  Dunit = g/cm3
  Dvalue = 11.28
  Group = -> [U_element001,C_element117]
  conduct = 2
  density = 1
  expand = 3
  formula = G4_URANIUM_DICARBIDE
  name = G4_URANIUM_DICARBIDE
  specific = 4
FEATURE [App::DocumentObjectGroupPython] U_element002  label="U_element : 002"  # scripted group (container) (typed FeaturePython)
  n = 1
  ref = U_element
FEATURE [App::DocumentObjectGroupPython] C_element118  label="C_element : 065"  # scripted group (container) (typed FeaturePython)
  n = 1
  ref = C_element
FEATURE [App::DocumentObjectGroupPython] G4_URANIUM_MONOCARBIDE  # scripted group (container) (typed FeaturePython)
  Dunit = g/cm3
  Dvalue = 13.63
  Group = -> [U_element002,C_element118]
  conduct = 2
  density = 1
  expand = 3
  formula = G4_URANIUM_MONOCARBIDE
  name = G4_URANIUM_MONOCARBIDE
  specific = 4
FEATURE [App::DocumentObjectGroupPython] U_element003  label="U_element : 003"  # scripted group (container) (typed FeaturePython)
  n = 1
  ref = U_element
FEATURE [App::DocumentObjectGroupPython] O_element100  label="O_element : 054"  # scripted group (container) (typed FeaturePython)
  n = 2
  ref = O_element
FEATURE [App::DocumentObjectGroupPython] G4_URANIUM_OXIDE  # scripted group (container) (typed FeaturePython)
  Dunit = g/cm3
  Dvalue = 10.96
  Group = -> [U_element003,O_element100]
  conduct = 2
  density = 1
  expand = 3
  formula = G4_URANIUM_OXIDE
  name = G4_URANIUM_OXIDE
  specific = 4
FEATURE [App::DocumentObjectGroupPython] C_element119  label="C_element : 066"  # scripted group (container) (typed FeaturePython)
  n = 1
  ref = C_element
FEATURE [App::DocumentObjectGroupPython] H_element107  label="H_element : 057"  # scripted group (container) (typed FeaturePython)
  n = 4
  ref = H_element
FEATURE [App::DocumentObjectGroupPython] N_element046  label="N_element : 019"  # scripted group (container) (typed FeaturePython)
  n = 2
  ref = N_element
FEATURE [App::DocumentObjectGroupPython] O_element101  label="O_element : 055"  # scripted group (container) (typed FeaturePython)
  n = 1
  ref = O_element
FEATURE [App::DocumentObjectGroupPython] G4_UREA  # scripted group (container) (typed FeaturePython)
  Dunit = g/cm3
  Dvalue = 1.323
  Group = -> [C_element119,H_element107,N_element046,O_element101]
  conduct = 2
  density = 1
  expand = 3
  formula = G4_UREA
  name = G4_UREA
  specific = 4
FEATURE [App::DocumentObjectGroupPython] C_element120  label="C_element : 067"  # scripted group (container) (typed FeaturePython)
  n = 5
  ref = C_element
FEATURE [App::DocumentObjectGroupPython] H_element108  label="H_element : 058"  # scripted group (container) (typed FeaturePython)
  n = 11
  ref = H_element
FEATURE [App::DocumentObjectGroupPython] N_element047  label="N_element : 020"  # scripted group (container) (typed FeaturePython)
  n = 1
  ref = N_element
FEATURE [App::DocumentObjectGroupPython] O_element102  label="O_element : 056"  # scripted group (container) (typed FeaturePython)
  n = 2
  ref = O_element
FEATURE [App::DocumentObjectGroupPython] G4_VALINE  # scripted group (container) (typed FeaturePython)
  Dunit = g/cm3
  Dvalue = 1.23
  Group = -> [C_element120,H_element108,N_element047,O_element102]
  conduct = 2
  density = 1
  expand = 3
  formula = G4_VALINE
  name = G4_VALINE
  specific = 4
FEATURE [App::DocumentObjectGroupPython] H_element109  label="H_element : 0.009"  # scripted group (container) (typed FeaturePython)
  n = 0.009417
FEATURE [App::DocumentObjectGroupPython] C_element121  label="C_element : 0.281"  # scripted group (container) (typed FeaturePython)
  n = 0.280555
FEATURE [App::DocumentObjectGroupPython] F_element018  label="F_element : 0.710"  # scripted group (container) (typed FeaturePython)
  n = 0.710028
FEATURE [App::DocumentObjectGroupPython] G4_VITON  # scripted group (container) (typed FeaturePython)
  Dunit = g/cm3
  Dvalue = 1.8
  Group = -> [H_element109,C_element121,F_element018]
  conduct = 2
  density = 1
  expand = 3
  formula = G4_VITON
  name = G4_VITON
  specific = 4
FEATURE [App::DocumentObjectGroupPython] H_element110  label="H_element : 059"  # scripted group (container) (typed FeaturePython)
  n = 2
  ref = H_element
FEATURE [App::DocumentObjectGroupPython] O_element103  label="O_element : 057"  # scripted group (container) (typed FeaturePython)
  n = 1
  ref = O_element
FEATURE [App::DocumentObjectGroupPython] G4_WATER  # scripted group (container) (typed FeaturePython)
  Dunit = g/cm3
  Dvalue = 1
  Group = -> [H_element110,O_element103]
  conduct = 2
  density = 1
  expand = 3
  formula = G4_WATER
  name = G4_WATER
  specific = 4
FEATURE [App::DocumentObjectGroupPython] H_element111  label="H_element : 060"  # scripted group (container) (typed FeaturePython)
  n = 2
  ref = H_element
FEATURE [App::DocumentObjectGroupPython] O_element104  label="O_element : 058"  # scripted group (container) (typed FeaturePython)
  n = 1
  ref = O_element
FEATURE [App::DocumentObjectGroupPython] G4_WATER_VAPOR  # scripted group (container) (typed FeaturePython)
  Dunit = g/cm3
  Dvalue = 0.000756182
  Group = -> [H_element111,O_element104]
  conduct = 2
  density = 1
  expand = 3
  formula = G4_WATER_VAPOR
  name = G4_WATER_VAPOR
  specific = 4
FEATURE [App::DocumentObjectGroupPython] C_element122  label="C_element : 068"  # scripted group (container) (typed FeaturePython)
  n = 8
  ref = C_element
FEATURE [App::DocumentObjectGroupPython] H_element112  label="H_element : 061"  # scripted group (container) (typed FeaturePython)
  n = 10
  ref = H_element
FEATURE [App::DocumentObjectGroupPython] G4_XYLENE  # scripted group (container) (typed FeaturePython)
  Dunit = g/cm3
  Dvalue = 0.87
  Group = -> [C_element122,H_element112]
  conduct = 2
  density = 1
  expand = 3
  formula = G4_XYLENE
  name = G4_XYLENE
  specific = 4
FEATURE [App::DocumentObjectGroupPython] C_element123  label="C_element : 069"  # scripted group (container) (typed FeaturePython)
  n = 1
  ref = C_element
FEATURE [App::DocumentObjectGroupPython] G4_GRAPHITE  # scripted group (container) (typed FeaturePython)
  Dunit = g/cm3
  Dvalue = 2.21
  Group = -> [C_element123]
  conduct = 2
  density = 1
  expand = 3
  formula = G4_GRAPHITE
  name = G4_GRAPHITE
  specific = 4
FEATURE [App::DocumentObjectGroupPython] NIST  # scripted group (container) (typed FeaturePython)
  Group = -> [G4_A_150_TISSUE,G4_ACETONE,G4_ACETYLENE,G4_ADENINE,G4_ADIPOSE_TISSUE_ICRP,G4_AIR,G4_ALANINE,G4_ALUMINUM_OXIDE,G4_AMBER,G4_AMMONIA,G4_ANILINE,G4_ANTHRACENE,G4_B_100_BONE,G4_BAKELITE,G4_BARIUM_FLUORIDE,G4_BARIUM_SULFATE,G4_BENZENE,G4_BERYLLIUM_OXIDE,G4_BGO,G4_BLOOD_ICRP,G4_BONE_COMPACT_ICRU,G4_BONE_CORTICAL_ICRP,G4_BORON_CARBIDE,G4_BORON_OXIDE,G4_BRAIN_ICRP,G4_BUTANE,G4_N_BUTYL_ALCOHOL,G4_C_552,+152 more]
FEATURE [App::DocumentObjectGroupPython] H_element113  label="H_element : 062"  # scripted group (container) (typed FeaturePython)
  n = 1
  ref = H_element
FEATURE [App::DocumentObjectGroupPython] G4_H  # scripted group (container) (typed FeaturePython)
  Dunit = g/cm3
  Dvalue = 8.3748e-05
  Group = -> [H_element113]
  conduct = 2
  density = 1
  expand = 3
  formula = H
  name = G4_H
  specific = 4
FEATURE [App::DocumentObjectGroupPython] He_element001  label="He_element : 1"  # scripted group (container) (typed FeaturePython)
  n = 1
  ref = He_element
FEATURE [App::DocumentObjectGroupPython] G4_He  # scripted group (container) (typed FeaturePython)
  Dunit = g/cm3
  Dvalue = 0.000166322
  Group = -> [He_element001]
  conduct = 2
  density = 1
  expand = 3
  formula = He
  name = G4_He
  specific = 4
FEATURE [App::DocumentObjectGroupPython] Li_element008  label="Li_element : 008"  # scripted group (container) (typed FeaturePython)
  n = 1
  ref = Li_element
FEATURE [App::DocumentObjectGroupPython] G4_Li  # scripted group (container) (typed FeaturePython)
  Dunit = g/cm3
  Dvalue = 0.534
  Group = -> [Li_element008]
  conduct = 2
  density = 1
  expand = 3
  formula = Li
  name = G4_Li
  specific = 4
FEATURE [App::DocumentObjectGroupPython] Be_element002  label="Be_element : 002"  # scripted group (container) (typed FeaturePython)
  n = 1
  ref = Be_element
FEATURE [App::DocumentObjectGroupPython] G4_Be  # scripted group (container) (typed FeaturePython)
  Dunit = g/cm3
  Dvalue = 1.848
  Group = -> [Be_element002]
  conduct = 2
  density = 1
  expand = 3
  formula = Be
  name = G4_Be
  specific = 4
FEATURE [App::DocumentObjectGroupPython] B_element007  label="B_element : 007"  # scripted group (container) (typed FeaturePython)
  n = 1
  ref = B_element
FEATURE [App::DocumentObjectGroupPython] G4_B  # scripted group (container) (typed FeaturePython)
  Dunit = g/cm3
  Dvalue = 2.37
  Group = -> [B_element007]
  conduct = 2
  density = 1
  expand = 3
  formula = B
  name = G4_B
  specific = 4
FEATURE [App::DocumentObjectGroupPython] C_element124  label="C_element : 070"  # scripted group (container) (typed FeaturePython)
  n = 1
  ref = C_element
FEATURE [App::DocumentObjectGroupPython] G4_C  # scripted group (container) (typed FeaturePython)
  Dunit = g/cm3
  Dvalue = 2
  Group = -> [C_element124]
  conduct = 2
  density = 1
  expand = 3
  formula = C
  name = G4_C
  specific = 4
FEATURE [App::DocumentObjectGroupPython] N_element048  label="N_element : 021"  # scripted group (container) (typed FeaturePython)
  n = 1
  ref = N_element
FEATURE [App::DocumentObjectGroupPython] G4_N  # scripted group (container) (typed FeaturePython)
  Dunit = g/cm3
  Dvalue = 0.0011652
  Group = -> [N_element048]
  conduct = 2
  density = 1
  expand = 3
  formula = N
  name = G4_N
  specific = 4
FEATURE [App::DocumentObjectGroupPython] O_element105  label="O_element : 059"  # scripted group (container) (typed FeaturePython)
  n = 1
  ref = O_element
FEATURE [App::DocumentObjectGroupPython] G4_O  # scripted group (container) (typed FeaturePython)
  Dunit = g/cm3
  Dvalue = 0.00133151
  Group = -> [O_element105]
  conduct = 2
  density = 1
  expand = 3
  formula = O
  name = G4_O
  specific = 4
FEATURE [App::DocumentObjectGroupPython] F_element019  label="F_element : 008"  # scripted group (container) (typed FeaturePython)
  n = 1
  ref = F_element
FEATURE [App::DocumentObjectGroupPython] G4_F  # scripted group (container) (typed FeaturePython)
  Dunit = g/cm3
  Dvalue = 0.00158029
  Group = -> [F_element019]
  conduct = 2
  density = 1
  expand = 3
  formula = F
  name = G4_F
  specific = 4
FEATURE [App::DocumentObjectGroupPython] Ne_element001  label="Ne_element : 1"  # scripted group (container) (typed FeaturePython)
  n = 1
  ref = Ne_element
FEATURE [App::DocumentObjectGroupPython] G4_Ne  # scripted group (container) (typed FeaturePython)
  Dunit = g/cm3
  Dvalue = 0.000838505
  Group = -> [Ne_element001]
  conduct = 2
  density = 1
  expand = 3
  formula = Ne
  name = G4_Ne
  specific = 4
FEATURE [App::DocumentObjectGroupPython] Na_element020  label="Na_element : 005"  # scripted group (container) (typed FeaturePython)
  n = 1
  ref = Na_element
FEATURE [App::DocumentObjectGroupPython] G4_Na  # scripted group (container) (typed FeaturePython)
  Dunit = g/cm3
  Dvalue = 0.971
  Group = -> [Na_element020]
  conduct = 2
  density = 1
  expand = 3
  formula = Na
  name = G4_Na
  specific = 4
FEATURE [App::DocumentObjectGroupPython] Mg_element011  label="Mg_element : 005"  # scripted group (container) (typed FeaturePython)
  n = 1
  ref = Mg_element
FEATURE [App::DocumentObjectGroupPython] G4_Mg  # scripted group (container) (typed FeaturePython)
  Dunit = g/cm3
  Dvalue = 1.74
  Group = -> [Mg_element011]
  conduct = 2
  density = 1
  expand = 3
  formula = Mg
  name = G4_Mg
  specific = 4
FEATURE [App::DocumentObjectGroupPython] Al_element004  label="Al_element : 1"  # scripted group (container) (typed FeaturePython)
  n = 1
  ref = Al_element
FEATURE [App::DocumentObjectGroupPython] G4_Al  # scripted group (container) (typed FeaturePython)
  Dunit = g/cm3
  Dvalue = 2.699
  Group = -> [Al_element004]
  conduct = 2
  density = 1
  expand = 3
  formula = Al
  name = G4_Al
  specific = 4
FEATURE [App::DocumentObjectGroupPython] Si_element007  label="Si_element : 002"  # scripted group (container) (typed FeaturePython)
  n = 1
  ref = Si_element
FEATURE [App::DocumentObjectGroupPython] G4_Si  # scripted group (container) (typed FeaturePython)
  Dunit = g/cm3
  Dvalue = 2.33
  Group = -> [Si_element007]
  conduct = 2
  density = 1
  expand = 3
  formula = Si
  name = G4_Si
  specific = 4
FEATURE [App::DocumentObjectGroupPython] P_element013  label="P_element : 002"  # scripted group (container) (typed FeaturePython)
  n = 1
  ref = P_element
FEATURE [App::DocumentObjectGroupPython] G4_P  # scripted group (container) (typed FeaturePython)
  Dunit = g/cm3
  Dvalue = 2.2
  Group = -> [P_element013]
  conduct = 2
  density = 1
  expand = 3
  formula = P
  name = G4_P
  specific = 4
FEATURE [App::DocumentObjectGroupPython] S_element023  label="S_element : 007"  # scripted group (container) (typed FeaturePython)
  n = 1
  ref = S_element
FEATURE [App::DocumentObjectGroupPython] G4_S  # scripted group (container) (typed FeaturePython)
  Dunit = g/cm3
  Dvalue = 2
  Group = -> [S_element023]
  conduct = 2
  density = 1
  expand = 3
  formula = S
  name = G4_S
  specific = 4
FEATURE [App::DocumentObjectGroupPython] Cl_element029  label="Cl_element : 015"  # scripted group (container) (typed FeaturePython)
  n = 1
  ref = Cl_element
FEATURE [App::DocumentObjectGroupPython] G4_Cl  # scripted group (container) (typed FeaturePython)
  Dunit = g/cm3
  Dvalue = 0.00299473
  Group = -> [Cl_element029]
  conduct = 2
  density = 1
  expand = 3
  formula = Cl
  name = G4_Cl
  specific = 4
FEATURE [App::DocumentObjectGroupPython] Ar_element002  label="Ar_element : 1"  # scripted group (container) (typed FeaturePython)
  n = 1
  ref = Ar_element
FEATURE [App::DocumentObjectGroupPython] G4_Ar  # scripted group (container) (typed FeaturePython)
  Dunit = g/cm3
  Dvalue = 0.00166201
  Group = -> [Ar_element002]
  conduct = 2
  density = 1
  expand = 3
  formula = Ar
  name = G4_Ar
  specific = 4
FEATURE [App::DocumentObjectGroupPython] K_element013  label="K_element : 003"  # scripted group (container) (typed FeaturePython)
  n = 1
  ref = K_element
FEATURE [App::DocumentObjectGroupPython] G4_K  # scripted group (container) (typed FeaturePython)
  Dunit = g/cm3
  Dvalue = 0.862
  Group = -> [K_element013]
  conduct = 2
  density = 1
  expand = 3
  formula = K
  name = G4_K
  specific = 4
FEATURE [App::DocumentObjectGroupPython] Ca_element014  label="Ca_element : 007"  # scripted group (container) (typed FeaturePython)
  n = 1
  ref = Ca_element
FEATURE [App::DocumentObjectGroupPython] G4_Ca  # scripted group (container) (typed FeaturePython)
  Dunit = g/cm3
  Dvalue = 1.55
  Group = -> [Ca_element014]
  conduct = 2
  density = 1
  expand = 3
  formula = Ca
  name = G4_Ca
  specific = 4
FEATURE [App::DocumentObjectGroupPython] Sc_element001  label="Sc_element : 1"  # scripted group (container) (typed FeaturePython)
  n = 1
  ref = Sc_element
FEATURE [App::DocumentObjectGroupPython] G4_Sc  # scripted group (container) (typed FeaturePython)
  Dunit = g/cm3
  Dvalue = 2.989
  Group = -> [Sc_element001]
  conduct = 2
  density = 1
  expand = 3
  formula = Sc
  name = G4_Sc
  specific = 4
FEATURE [App::DocumentObjectGroupPython] Ti_element004  label="Ti_element : 002"  # scripted group (container) (typed FeaturePython)
  n = 1
  ref = Ti_element
FEATURE [App::DocumentObjectGroupPython] G4_Ti  # scripted group (container) (typed FeaturePython)
  Dunit = g/cm3
  Dvalue = 4.54
  Group = -> [Ti_element004]
  conduct = 2
  density = 1
  expand = 3
  formula = Ti
  name = G4_Ti
  specific = 4
FEATURE [App::DocumentObjectGroupPython] V_element001  label="V_element : 1"  # scripted group (container) (typed FeaturePython)
  n = 1
  ref = V_element
FEATURE [App::DocumentObjectGroupPython] G4_V  # scripted group (container) (typed FeaturePython)
  Dunit = g/cm3
  Dvalue = 6.11
  Group = -> [V_element001]
  conduct = 2
  density = 1
  expand = 3
  formula = V
  name = G4_V
  specific = 4
FEATURE [App::DocumentObjectGroupPython] Cr_element001  label="Cr_element : 1"  # scripted group (container) (typed FeaturePython)
  n = 1
  ref = Cr_element
FEATURE [App::DocumentObjectGroupPython] G4_Cr  # scripted group (container) (typed FeaturePython)
  Dunit = g/cm3
  Dvalue = 7.18
  Group = -> [Cr_element001]
  conduct = 2
  density = 1
  expand = 3
  formula = Cr
  name = G4_Cr
  specific = 4
FEATURE [App::DocumentObjectGroupPython] Mn_element001  label="Mn_element : 1"  # scripted group (container) (typed FeaturePython)
  n = 1
  ref = Mn_element
FEATURE [App::DocumentObjectGroupPython] G4_Mn  # scripted group (container) (typed FeaturePython)
  Dunit = g/cm3
  Dvalue = 7.44
  Group = -> [Mn_element001]
  conduct = 2
  density = 1
  expand = 3
  formula = Mn
  name = G4_Mn
  specific = 4
FEATURE [App::DocumentObjectGroupPython] Fe_element007  label="Fe_element : 004"  # scripted group (container) (typed FeaturePython)
  n = 1
  ref = Fe_element
FEATURE [App::DocumentObjectGroupPython] G4_Fe  # scripted group (container) (typed FeaturePython)
  Dunit = g/cm3
  Dvalue = 7.874
  Group = -> [Fe_element007]
  conduct = 2
  density = 1
  expand = 3
  formula = Fe
  name = G4_Fe
  specific = 4
FEATURE [App::DocumentObjectGroupPython] Co_element001  label="Co_element : 1"  # scripted group (container) (typed FeaturePython)
  n = 1
  ref = Co_element
FEATURE [App::DocumentObjectGroupPython] G4_Co  # scripted group (container) (typed FeaturePython)
  Dunit = g/cm3
  Dvalue = 8.9
  Group = -> [Co_element001]
  conduct = 2
  density = 1
  expand = 3
  formula = Co
  name = G4_Co
  specific = 4
FEATURE [App::DocumentObjectGroupPython] Ni_element001  label="Ni_element : 1"  # scripted group (container) (typed FeaturePython)
  n = 1
  ref = Ni_element
FEATURE [App::DocumentObjectGroupPython] G4_Ni  # scripted group (container) (typed FeaturePython)
  Dunit = g/cm3
  Dvalue = 8.902
  Group = -> [Ni_element001]
  conduct = 2
  density = 1
  expand = 3
  formula = Ni
  name = G4_Ni
  specific = 4
FEATURE [App::DocumentObjectGroupPython] Cu_element001  label="Cu_element : 1"  # scripted group (container) (typed FeaturePython)
  n = 1
  ref = Cu_element
FEATURE [App::DocumentObjectGroupPython] G4_Cu  # scripted group (container) (typed FeaturePython)
  Dunit = g/cm3
  Dvalue = 8.96
  Group = -> [Cu_element001]
  conduct = 2
  density = 1
  expand = 3
  formula = Cu
  name = G4_Cu
  specific = 4
FEATURE [App::DocumentObjectGroupPython] Zn_element001  label="Zn_element : 1"  # scripted group (container) (typed FeaturePython)
  n = 1
  ref = Zn_element
FEATURE [App::DocumentObjectGroupPython] G4_Zn  # scripted group (container) (typed FeaturePython)
  Dunit = g/cm3
  Dvalue = 7.133
  Group = -> [Zn_element001]
  conduct = 2
  density = 1
  expand = 3
  formula = Zn
  name = G4_Zn
  specific = 4
FEATURE [App::DocumentObjectGroupPython] Ga_element002  label="Ga_element : 002"  # scripted group (container) (typed FeaturePython)
  n = 1
  ref = Ga_element
FEATURE [App::DocumentObjectGroupPython] G4_Ga  # scripted group (container) (typed FeaturePython)
  Dunit = g/cm3
  Dvalue = 5.904
  Group = -> [Ga_element002]
  conduct = 2
  density = 1
  expand = 3
  formula = Ga
  name = G4_Ga
  specific = 4
FEATURE [App::DocumentObjectGroupPython] Ge_element002  label="Ge_element : 1"  # scripted group (container) (typed FeaturePython)
  n = 1
  ref = Ge_element
FEATURE [App::DocumentObjectGroupPython] G4_Ge  # scripted group (container) (typed FeaturePython)
  Dunit = g/cm3
  Dvalue = 5.323
  Group = -> [Ge_element002]
  conduct = 2
  density = 1
  expand = 3
  formula = Ge
  name = G4_Ge
  specific = 4
FEATURE [App::DocumentObjectGroupPython] As_element003  label="As_element : 002"  # scripted group (container) (typed FeaturePython)
  n = 1
  ref = As_element
FEATURE [App::DocumentObjectGroupPython] G4_As  # scripted group (container) (typed FeaturePython)
  Dunit = g/cm3
  Dvalue = 5.73
  Group = -> [As_element003]
  conduct = 2
  density = 1
  expand = 3
  formula = As
  name = G4_As
  specific = 4
FEATURE [App::DocumentObjectGroupPython] Se_element001  label="Se_element : 1"  # scripted group (container) (typed FeaturePython)
  n = 1
  ref = Se_element
FEATURE [App::DocumentObjectGroupPython] G4_Se  # scripted group (container) (typed FeaturePython)
  Dunit = g/cm3
  Dvalue = 4.5
  Group = -> [Se_element001]
  conduct = 2
  density = 1
  expand = 3
  formula = Se
  name = G4_Se
  specific = 4
FEATURE [App::DocumentObjectGroupPython] Br_element007  label="Br_element : 004"  # scripted group (container) (typed FeaturePython)
  n = 1
  ref = Br_element
FEATURE [App::DocumentObjectGroupPython] G4_Br  # scripted group (container) (typed FeaturePython)
  Dunit = g/cm3
  Dvalue = 0.0070721
  Group = -> [Br_element007]
  conduct = 2
  density = 1
  expand = 3
  formula = Br
  name = G4_Br
  specific = 4
FEATURE [App::DocumentObjectGroupPython] Kr_element001  label="Kr_element : 1"  # scripted group (container) (typed FeaturePython)
  n = 1
  ref = Kr_element
FEATURE [App::DocumentObjectGroupPython] G4_Kr  # scripted group (container) (typed FeaturePython)
  Dunit = g/cm3
  Dvalue = 0.00347832
  Group = -> [Kr_element001]
  conduct = 2
  density = 1
  expand = 3
  formula = Kr
  name = G4_Kr
  specific = 4
FEATURE [App::DocumentObjectGroupPython] Rb_element001  label="Rb_element : 1"  # scripted group (container) (typed FeaturePython)
  n = 1
  ref = Rb_element
FEATURE [App::DocumentObjectGroupPython] G4_Rb  # scripted group (container) (typed FeaturePython)
  Dunit = g/cm3
  Dvalue = 1.532
  Group = -> [Rb_element001]
  conduct = 2
  density = 1
  expand = 3
  formula = Rb
  name = G4_Rb
  specific = 4
FEATURE [App::DocumentObjectGroupPython] Sr_element001  label="Sr_element : 1"  # scripted group (container) (typed FeaturePython)
  n = 1
  ref = Sr_element
FEATURE [App::DocumentObjectGroupPython] G4_Sr  # scripted group (container) (typed FeaturePython)
  Dunit = g/cm3
  Dvalue = 2.54
  Group = -> [Sr_element001]
  conduct = 2
  density = 1
  expand = 3
  formula = Sr
  name = G4_Sr
  specific = 4
FEATURE [App::DocumentObjectGroupPython] Y_element001  label="Y_element : 1"  # scripted group (container) (typed FeaturePython)
  n = 1
  ref = Y_element
FEATURE [App::DocumentObjectGroupPython] G4_Y  # scripted group (container) (typed FeaturePython)
  Dunit = g/cm3
  Dvalue = 4.469
  Group = -> [Y_element001]
  conduct = 2
  density = 1
  expand = 3
  formula = Y
  name = G4_Y
  specific = 4
FEATURE [App::DocumentObjectGroupPython] Zr_element001  label="Zr_element : 1"  # scripted group (container) (typed FeaturePython)
  n = 1
  ref = Zr_element
FEATURE [App::DocumentObjectGroupPython] G4_Zr  # scripted group (container) (typed FeaturePython)
  Dunit = g/cm3
  Dvalue = 6.506
  Group = -> [Zr_element001]
  conduct = 2
  density = 1
  expand = 3
  formula = Zr
  name = G4_Zr
  specific = 4
FEATURE [App::DocumentObjectGroupPython] Nb_element001  label="Nb_element : 1"  # scripted group (container) (typed FeaturePython)
  n = 1
  ref = Nb_element
FEATURE [App::DocumentObjectGroupPython] G4_Nb  # scripted group (container) (typed FeaturePython)
  Dunit = g/cm3
  Dvalue = 8.57
  Group = -> [Nb_element001]
  conduct = 2
  density = 1
  expand = 3
  formula = Nb
  name = G4_Nb
  specific = 4
FEATURE [App::DocumentObjectGroupPython] Mo_element001  label="Mo_element : 1"  # scripted group (container) (typed FeaturePython)
  n = 1
  ref = Mo_element
FEATURE [App::DocumentObjectGroupPython] G4_Mo  # scripted group (container) (typed FeaturePython)
  Dunit = g/cm3
  Dvalue = 10.22
  Group = -> [Mo_element001]
  conduct = 2
  density = 1
  expand = 3
  formula = Mo
  name = G4_Mo
  specific = 4
FEATURE [App::DocumentObjectGroupPython] Tc_element001  label="Tc_element : 1"  # scripted group (container) (typed FeaturePython)
  n = 1
  ref = Tc_element
FEATURE [App::DocumentObjectGroupPython] G4_Tc  # scripted group (container) (typed FeaturePython)
  Dunit = g/cm3
  Dvalue = 11.5
  Group = -> [Tc_element001]
  conduct = 2
  density = 1
  expand = 3
  formula = Tc
  name = G4_Tc
  specific = 4
FEATURE [App::DocumentObjectGroupPython] Ru_element001  label="Ru_element : 1"  # scripted group (container) (typed FeaturePython)
  n = 1
  ref = Ru_element
FEATURE [App::DocumentObjectGroupPython] G4_Ru  # scripted group (container) (typed FeaturePython)
  Dunit = g/cm3
  Dvalue = 12.41
  Group = -> [Ru_element001]
  conduct = 2
  density = 1
  expand = 3
  formula = Ru
  name = G4_Ru
  specific = 4
FEATURE [App::DocumentObjectGroupPython] Rh_element001  label="Rh_element : 1"  # scripted group (container) (typed FeaturePython)
  n = 1
  ref = Rh_element
FEATURE [App::DocumentObjectGroupPython] G4_Rh  # scripted group (container) (typed FeaturePython)
  Dunit = g/cm3
  Dvalue = 12.41
  Group = -> [Rh_element001]
  conduct = 2
  density = 1
  expand = 3
  formula = Rh
  name = G4_Rh
  specific = 4
FEATURE [App::DocumentObjectGroupPython] Pd_element001  label="Pd_element : 1"  # scripted group (container) (typed FeaturePython)
  n = 1
  ref = Pd_element
FEATURE [App::DocumentObjectGroupPython] G4_Pd  # scripted group (container) (typed FeaturePython)
  Dunit = g/cm3
  Dvalue = 12.02
  Group = -> [Pd_element001]
  conduct = 2
  density = 1
  expand = 3
  formula = Pd
  name = G4_Pd
  specific = 4
FEATURE [App::DocumentObjectGroupPython] Ag_element006  label="Ag_element : 004"  # scripted group (container) (typed FeaturePython)
  n = 1
  ref = Ag_element
FEATURE [App::DocumentObjectGroupPython] G4_Ag  # scripted group (container) (typed FeaturePython)
  Dunit = g/cm3
  Dvalue = 10.5
  Group = -> [Ag_element006]
  conduct = 2
  density = 1
  expand = 3
  formula = Ag
  name = G4_Ag
  specific = 4
FEATURE [App::DocumentObjectGroupPython] Cd_element003  label="Cd_element : 003"  # scripted group (container) (typed FeaturePython)
  n = 1
  ref = Cd_element
FEATURE [App::DocumentObjectGroupPython] G4_Cd  # scripted group (container) (typed FeaturePython)
  Dunit = g/cm3
  Dvalue = 8.65
  Group = -> [Cd_element003]
  conduct = 2
  density = 1
  expand = 3
  formula = Cd
  name = G4_Cd
  specific = 4
FEATURE [App::DocumentObjectGroupPython] In_element001  label="In_element : 1"  # scripted group (container) (typed FeaturePython)
  n = 1
  ref = In_element
FEATURE [App::DocumentObjectGroupPython] G4_In  # scripted group (container) (typed FeaturePython)
  Dunit = g/cm3
  Dvalue = 7.31
  Group = -> [In_element001]
  conduct = 2
  density = 1
  expand = 3
  formula = In
  name = G4_In
  specific = 4
FEATURE [App::DocumentObjectGroupPython] Sn_element001  label="Sn_element : 1"  # scripted group (container) (typed FeaturePython)
  n = 1
  ref = Sn_element
FEATURE [App::DocumentObjectGroupPython] G4_Sn  # scripted group (container) (typed FeaturePython)
  Dunit = g/cm3
  Dvalue = 7.31
  Group = -> [Sn_element001]
  conduct = 2
  density = 1
  expand = 3
  formula = Sn
  name = G4_Sn
  specific = 4
FEATURE [App::DocumentObjectGroupPython] Sb_element001  label="Sb_element : 1"  # scripted group (container) (typed FeaturePython)
  n = 1
  ref = Sb_element
FEATURE [App::DocumentObjectGroupPython] G4_Sb  # scripted group (container) (typed FeaturePython)
  Dunit = g/cm3
  Dvalue = 6.691
  Group = -> [Sb_element001]
  conduct = 2
  density = 1
  expand = 3
  formula = Sb
  name = G4_Sb
  specific = 4
FEATURE [App::DocumentObjectGroupPython] Te_element002  label="Te_element : 002"  # scripted group (container) (typed FeaturePython)
  n = 1
  ref = Te_element
FEATURE [App::DocumentObjectGroupPython] G4_Te  # scripted group (container) (typed FeaturePython)
  Dunit = g/cm3
  Dvalue = 6.24
  Group = -> [Te_element002]
  conduct = 2
  density = 1
  expand = 3
  formula = Te
  name = G4_Te
  specific = 4
FEATURE [App::DocumentObjectGroupPython] I_element010  label="I_element : 006"  # scripted group (container) (typed FeaturePython)
  n = 1
  ref = I_element
FEATURE [App::DocumentObjectGroupPython] G4_I  # scripted group (container) (typed FeaturePython)
  Dunit = g/cm3
  Dvalue = 4.93
  Group = -> [I_element010]
  conduct = 2
  density = 1
  expand = 3
  formula = I
  name = G4_I
  specific = 4
FEATURE [App::DocumentObjectGroupPython] Xe_element001  label="Xe_element : 1"  # scripted group (container) (typed FeaturePython)
  n = 1
  ref = Xe_element
FEATURE [App::DocumentObjectGroupPython] G4_Xe  # scripted group (container) (typed FeaturePython)
  Dunit = g/cm3
  Dvalue = 0.00548536
  Group = -> [Xe_element001]
  conduct = 2
  density = 1
  expand = 3
  formula = Xe
  name = G4_Xe
  specific = 4
FEATURE [App::DocumentObjectGroupPython] Cs_element003  label="Cs_element : 003"  # scripted group (container) (typed FeaturePython)
  n = 1
  ref = Cs_element
FEATURE [App::DocumentObjectGroupPython] G4_Cs  # scripted group (container) (typed FeaturePython)
  Dunit = g/cm3
  Dvalue = 1.873
  Group = -> [Cs_element003]
  conduct = 2
  density = 1
  expand = 3
  formula = Cs
  name = G4_Cs
  specific = 4
FEATURE [App::DocumentObjectGroupPython] Ba_element003  label="Ba_element : 003"  # scripted group (container) (typed FeaturePython)
  n = 1
  ref = Ba_element
FEATURE [App::DocumentObjectGroupPython] G4_Ba  # scripted group (container) (typed FeaturePython)
  Dunit = g/cm3
  Dvalue = 3.5
  Group = -> [Ba_element003]
  conduct = 2
  density = 1
  expand = 3
  formula = Ba
  name = G4_Ba
  specific = 4
FEATURE [App::DocumentObjectGroupPython] La_element003  label="La_element : 003"  # scripted group (container) (typed FeaturePython)
  n = 1
  ref = La_element
FEATURE [App::DocumentObjectGroupPython] G4_La  # scripted group (container) (typed FeaturePython)
  Dunit = g/cm3
  Dvalue = 6.154
  Group = -> [La_element003]
  conduct = 2
  density = 1
  expand = 3
  formula = La
  name = G4_La
  specific = 4
FEATURE [App::DocumentObjectGroupPython] Ce_element002  label="Ce_element : 1"  # scripted group (container) (typed FeaturePython)
  n = 1
  ref = Ce_element
FEATURE [App::DocumentObjectGroupPython] G4_Ce  # scripted group (container) (typed FeaturePython)
  Dunit = g/cm3
  Dvalue = 6.657
  Group = -> [Ce_element002]
  conduct = 2
  density = 1
  expand = 3
  formula = Ce
  name = G4_Ce
  specific = 4
FEATURE [App::DocumentObjectGroupPython] Pr_element001  label="Pr_element : 1"  # scripted group (container) (typed FeaturePython)
  n = 1
  ref = Pr_element
FEATURE [App::DocumentObjectGroupPython] G4_Pr  # scripted group (container) (typed FeaturePython)
  Dunit = g/cm3
  Dvalue = 6.71
  Group = -> [Pr_element001]
  conduct = 2
  density = 1
  expand = 3
  formula = Pr
  name = G4_Pr
  specific = 4
FEATURE [App::DocumentObjectGroupPython] Nd_element001  label="Nd_element : 1"  # scripted group (container) (typed FeaturePython)
  n = 1
  ref = Nd_element
FEATURE [App::DocumentObjectGroupPython] G4_Nd  # scripted group (container) (typed FeaturePython)
  Dunit = g/cm3
  Dvalue = 6.9
  Group = -> [Nd_element001]
  conduct = 2
  density = 1
  expand = 3
  formula = Nd
  name = G4_Nd
  specific = 4
FEATURE [App::DocumentObjectGroupPython] Pm_element001  label="Pm_element : 1"  # scripted group (container) (typed FeaturePython)
  n = 1
  ref = Pm_element
FEATURE [App::DocumentObjectGroupPython] G4_Pm  # scripted group (container) (typed FeaturePython)
  Dunit = g/cm3
  Dvalue = 7.22
  Group = -> [Pm_element001]
  conduct = 2
  density = 1
  expand = 3
  formula = Pm
  name = G4_Pm
  specific = 4
FEATURE [App::DocumentObjectGroupPython] Sm_element001  label="Sm_element : 1"  # scripted group (container) (typed FeaturePython)
  n = 1
  ref = Sm_element
FEATURE [App::DocumentObjectGroupPython] G4_Sm  # scripted group (container) (typed FeaturePython)
  Dunit = g/cm3
  Dvalue = 7.46
  Group = -> [Sm_element001]
  conduct = 2
  density = 1
  expand = 3
  formula = Sm
  name = G4_Sm
  specific = 4
FEATURE [App::DocumentObjectGroupPython] Eu_element001  label="Eu_element : 1"  # scripted group (container) (typed FeaturePython)
  n = 1
  ref = Eu_element
FEATURE [App::DocumentObjectGroupPython] G4_Eu  # scripted group (container) (typed FeaturePython)
  Dunit = g/cm3
  Dvalue = 5.243
  Group = -> [Eu_element001]
  conduct = 2
  density = 1
  expand = 3
  formula = Eu
  name = G4_Eu
  specific = 4
FEATURE [App::DocumentObjectGroupPython] Gd_element002  label="Gd_element : 1"  # scripted group (container) (typed FeaturePython)
  n = 1
  ref = Gd_element
FEATURE [App::DocumentObjectGroupPython] G4_Gd  # scripted group (container) (typed FeaturePython)
  Dunit = g/cm3
  Dvalue = 7.9004
  Group = -> [Gd_element002]
  conduct = 2
  density = 1
  expand = 3
  formula = Gd
  name = G4_Gd
  specific = 4
FEATURE [App::DocumentObjectGroupPython] Tb_element001  label="Tb_element : 1"  # scripted group (container) (typed FeaturePython)
  n = 1
  ref = Tb_element
FEATURE [App::DocumentObjectGroupPython] G4_Tb  # scripted group (container) (typed FeaturePython)
  Dunit = g/cm3
  Dvalue = 8.229
  Group = -> [Tb_element001]
  conduct = 2
  density = 1
  expand = 3
  formula = Tb
  name = G4_Tb
  specific = 4
FEATURE [App::DocumentObjectGroupPython] Dy_element001  label="Dy_element : 1"  # scripted group (container) (typed FeaturePython)
  n = 1
  ref = Dy_element
FEATURE [App::DocumentObjectGroupPython] G4_Dy  # scripted group (container) (typed FeaturePython)
  Dunit = g/cm3
  Dvalue = 8.55
  Group = -> [Dy_element001]
  conduct = 2
  density = 1
  expand = 3
  formula = Dy
  name = G4_Dy
  specific = 4
FEATURE [App::DocumentObjectGroupPython] Ho_element001  label="Ho_element : 1"  # scripted group (container) (typed FeaturePython)
  n = 1
  ref = Ho_element
FEATURE [App::DocumentObjectGroupPython] G4_Ho  # scripted group (container) (typed FeaturePython)
  Dunit = g/cm3
  Dvalue = 8.795
  Group = -> [Ho_element001]
  conduct = 2
  density = 1
  expand = 3
  formula = Ho
  name = G4_Ho
  specific = 4
FEATURE [App::DocumentObjectGroupPython] Er_element001  label="Er_element : 1"  # scripted group (container) (typed FeaturePython)
  n = 1
  ref = Er_element
FEATURE [App::DocumentObjectGroupPython] G4_Er  # scripted group (container) (typed FeaturePython)
  Dunit = g/cm3
  Dvalue = 9.066
  Group = -> [Er_element001]
  conduct = 2
  density = 1
  expand = 3
  formula = Er
  name = G4_Er
  specific = 4
FEATURE [App::DocumentObjectGroupPython] Tm_element001  label="Tm_element : 1"  # scripted group (container) (typed FeaturePython)
  n = 1
  ref = Tm_element
FEATURE [App::DocumentObjectGroupPython] G4_Tm  # scripted group (container) (typed FeaturePython)
  Dunit = g/cm3
  Dvalue = 9.321
  Group = -> [Tm_element001]
  conduct = 2
  density = 1
  expand = 3
  formula = Tm
  name = G4_Tm
  specific = 4
FEATURE [App::DocumentObjectGroupPython] Yb_element001  label="Yb_element : 1"  # scripted group (container) (typed FeaturePython)
  n = 1
  ref = Yb_element
FEATURE [App::DocumentObjectGroupPython] G4_Yb  # scripted group (container) (typed FeaturePython)
  Dunit = g/cm3
  Dvalue = 6.73
  Group = -> [Yb_element001]
  conduct = 2
  density = 1
  expand = 3
  formula = Yb
  name = G4_Yb
  specific = 4
FEATURE [App::DocumentObjectGroupPython] Lu_element001  label="Lu_element : 1"  # scripted group (container) (typed FeaturePython)
  n = 1
  ref = Lu_element
FEATURE [App::DocumentObjectGroupPython] G4_Lu  # scripted group (container) (typed FeaturePython)
  Dunit = g/cm3
  Dvalue = 9.84
  Group = -> [Lu_element001]
  conduct = 2
  density = 1
  expand = 3
  formula = Lu
  name = G4_Lu
  specific = 4
FEATURE [App::DocumentObjectGroupPython] Hf_element001  label="Hf_element : 1"  # scripted group (container) (typed FeaturePython)
  n = 1
  ref = Hf_element
FEATURE [App::DocumentObjectGroupPython] G4_Hf  # scripted group (container) (typed FeaturePython)
  Dunit = g/cm3
  Dvalue = 13.31
  Group = -> [Hf_element001]
  conduct = 2
  density = 1
  expand = 3
  formula = Hf
  name = G4_Hf
  specific = 4
FEATURE [App::DocumentObjectGroupPython] Ta_element001  label="Ta_element : 1"  # scripted group (container) (typed FeaturePython)
  n = 1
  ref = Ta_element
FEATURE [App::DocumentObjectGroupPython] G4_Ta  # scripted group (container) (typed FeaturePython)
  Dunit = g/cm3
  Dvalue = 16.654
  Group = -> [Ta_element001]
  conduct = 2
  density = 1
  expand = 3
  formula = Ta
  name = G4_Ta
  specific = 4
FEATURE [App::DocumentObjectGroupPython] W_element004  label="W_element : 004"  # scripted group (container) (typed FeaturePython)
  n = 1
  ref = W_element
FEATURE [App::DocumentObjectGroupPython] G4_W  # scripted group (container) (typed FeaturePython)
  Dunit = g/cm3
  Dvalue = 19.3
  Group = -> [W_element004]
  conduct = 2
  density = 1
  expand = 3
  formula = W
  name = G4_W
  specific = 4
FEATURE [App::DocumentObjectGroupPython] Re_element001  label="Re_element : 1"  # scripted group (container) (typed FeaturePython)
  n = 1
  ref = Re_element
FEATURE [App::DocumentObjectGroupPython] G4_Re  # scripted group (container) (typed FeaturePython)
  Dunit = g/cm3
  Dvalue = 21.02
  Group = -> [Re_element001]
  conduct = 2
  density = 1
  expand = 3
  formula = Re
  name = G4_Re
  specific = 4
FEATURE [App::DocumentObjectGroupPython] Os_element001  label="Os_element : 1"  # scripted group (container) (typed FeaturePython)
  n = 1
  ref = Os_element
FEATURE [App::DocumentObjectGroupPython] G4_Os  # scripted group (container) (typed FeaturePython)
  Dunit = g/cm3
  Dvalue = 22.57
  Group = -> [Os_element001]
  conduct = 2
  density = 1
  expand = 3
  formula = Os
  name = G4_Os
  specific = 4
FEATURE [App::DocumentObjectGroupPython] Ir_element001  label="Ir_element : 1"  # scripted group (container) (typed FeaturePython)
  n = 1
  ref = Ir_element
FEATURE [App::DocumentObjectGroupPython] G4_Ir  # scripted group (container) (typed FeaturePython)
  Dunit = g/cm3
  Dvalue = 22.42
  Group = -> [Ir_element001]
  conduct = 2
  density = 1
  expand = 3
  formula = Ir
  name = G4_Ir
  specific = 4
FEATURE [App::DocumentObjectGroupPython] Pt_element001  label="Pt_element : 1"  # scripted group (container) (typed FeaturePython)
  n = 1
  ref = Pt_element
FEATURE [App::DocumentObjectGroupPython] G4_Pt  # scripted group (container) (typed FeaturePython)
  Dunit = g/cm3
  Dvalue = 21.45
  Group = -> [Pt_element001]
  conduct = 2
  density = 1
  expand = 3
  formula = Pt
  name = G4_Pt
  specific = 4
FEATURE [App::DocumentObjectGroupPython] Au_element001  label="Au_element : 1"  # scripted group (container) (typed FeaturePython)
  n = 1
  ref = Au_element
FEATURE [App::DocumentObjectGroupPython] G4_Au  # scripted group (container) (typed FeaturePython)
  Dunit = g/cm3
  Dvalue = 19.32
  Group = -> [Au_element001]
  conduct = 2
  density = 1
  expand = 3
  formula = Au
  name = G4_Au
  specific = 4
FEATURE [App::DocumentObjectGroupPython] Hg_element002  label="Hg_element : 002"  # scripted group (container) (typed FeaturePython)
  n = 1
  ref = Hg_element
FEATURE [App::DocumentObjectGroupPython] G4_Hg  # scripted group (container) (typed FeaturePython)
  Dunit = g/cm3
  Dvalue = 13.546
  Group = -> [Hg_element002]
  conduct = 2
  density = 1
  expand = 3
  formula = Hg
  name = G4_Hg
  specific = 4
FEATURE [App::DocumentObjectGroupPython] Tl_element002  label="Tl_element : 002"  # scripted group (container) (typed FeaturePython)
  n = 1
  ref = Tl_element
FEATURE [App::DocumentObjectGroupPython] G4_Tl  # scripted group (container) (typed FeaturePython)
  Dunit = g/cm3
  Dvalue = 11.72
  Group = -> [Tl_element002]
  conduct = 2
  density = 1
  expand = 3
  formula = Tl
  name = G4_Tl
  specific = 4
FEATURE [App::DocumentObjectGroupPython] Pb_element003  label="Pb_element : 1"  # scripted group (container) (typed FeaturePython)
  n = 1
  ref = Pb_element
FEATURE [App::DocumentObjectGroupPython] G4_Pb  # scripted group (container) (typed FeaturePython)
  Dunit = g/cm3
  Dvalue = 11.35
  Group = -> [Pb_element003]
  conduct = 2
  density = 1
  expand = 3
  formula = Pb
  name = G4_Pb
  specific = 4
FEATURE [App::DocumentObjectGroupPython] Bi_element002  label="Bi_element : 1"  # scripted group (container) (typed FeaturePython)
  n = 1
  ref = Bi_element
FEATURE [App::DocumentObjectGroupPython] G4_Bi  # scripted group (container) (typed FeaturePython)
  Dunit = g/cm3
  Dvalue = 9.747
  Group = -> [Bi_element002]
  conduct = 2
  density = 1
  expand = 3
  formula = Bi
  name = G4_Bi
  specific = 4
FEATURE [App::DocumentObjectGroupPython] Po_element001  label="Po_element : 1"  # scripted group (container) (typed FeaturePython)
  n = 1
  ref = Po_element
FEATURE [App::DocumentObjectGroupPython] G4_Po  # scripted group (container) (typed FeaturePython)
  Dunit = g/cm3
  Dvalue = 9.32
  Group = -> [Po_element001]
  conduct = 2
  density = 1
  expand = 3
  formula = Po
  name = G4_Po
  specific = 4
FEATURE [App::DocumentObjectGroupPython] At_element001  label="At_element : 1"  # scripted group (container) (typed FeaturePython)
  n = 1
  ref = At_element
FEATURE [App::DocumentObjectGroupPython] G4_At  # scripted group (container) (typed FeaturePython)
  Dunit = g/cm3
  Dvalue = 9.32
  Group = -> [At_element001]
  conduct = 2
  density = 1
  expand = 3
  formula = At
  name = G4_At
  specific = 4
FEATURE [App::DocumentObjectGroupPython] Rn_element001  label="Rn_element : 1"  # scripted group (container) (typed FeaturePython)
  n = 1
  ref = Rn_element
FEATURE [App::DocumentObjectGroupPython] G4_Rn  # scripted group (container) (typed FeaturePython)
  Dunit = g/cm3
  Dvalue = 0.00900662
  Group = -> [Rn_element001]
  conduct = 2
  density = 1
  expand = 3
  formula = Rn
  name = G4_Rn
  specific = 4
FEATURE [App::DocumentObjectGroupPython] Fr_element001  label="Fr_element : 1"  # scripted group (container) (typed FeaturePython)
  n = 1
  ref = Fr_element
FEATURE [App::DocumentObjectGroupPython] G4_Fr  # scripted group (container) (typed FeaturePython)
  Dunit = g/cm3
  Dvalue = 1
  Group = -> [Fr_element001]
  conduct = 2
  density = 1
  expand = 3
  formula = Fr
  name = G4_Fr
  specific = 4
FEATURE [App::DocumentObjectGroupPython] Ra_element001  label="Ra_element : 1"  # scripted group (container) (typed FeaturePython)
  n = 1
  ref = Ra_element
FEATURE [App::DocumentObjectGroupPython] G4_Ra  # scripted group (container) (typed FeaturePython)
  Dunit = g/cm3
  Dvalue = 5
  Group = -> [Ra_element001]
  conduct = 2
  density = 1
  expand = 3
  formula = Ra
  name = G4_Ra
  specific = 4
FEATURE [App::DocumentObjectGroupPython] Ac_element001  label="Ac_element : 1"  # scripted group (container) (typed FeaturePython)
  n = 1
  ref = Ac_element
FEATURE [App::DocumentObjectGroupPython] G4_Ac  # scripted group (container) (typed FeaturePython)
  Dunit = g/cm3
  Dvalue = 10.07
  Group = -> [Ac_element001]
  conduct = 2
  density = 1
  expand = 3
  formula = Ac
  name = G4_Ac
  specific = 4
FEATURE [App::DocumentObjectGroupPython] Th_element001  label="Th_element : 1"  # scripted group (container) (typed FeaturePython)
  n = 1
  ref = Th_element
FEATURE [App::DocumentObjectGroupPython] G4_Th  # scripted group (container) (typed FeaturePython)
  Dunit = g/cm3
  Dvalue = 11.72
  Group = -> [Th_element001]
  conduct = 2
  density = 1
  expand = 3
  formula = Th
  name = G4_Th
  specific = 4
FEATURE [App::DocumentObjectGroupPython] Pa_element001  label="Pa_element : 1"  # scripted group (container) (typed FeaturePython)
  n = 1
  ref = Pa_element
FEATURE [App::DocumentObjectGroupPython] G4_Pa  # scripted group (container) (typed FeaturePython)
  Dunit = g/cm3
  Dvalue = 15.37
  Group = -> [Pa_element001]
  conduct = 2
  density = 1
  expand = 3
  formula = Pa
  name = G4_Pa
  specific = 4
FEATURE [App::DocumentObjectGroupPython] U_element004  label="U_element : 004"  # scripted group (container) (typed FeaturePython)
  n = 1
  ref = U_element
FEATURE [App::DocumentObjectGroupPython] G4_U  # scripted group (container) (typed FeaturePython)
  Dunit = g/cm3
  Dvalue = 18.95
  Group = -> [U_element004]
  conduct = 2
  density = 1
  expand = 3
  formula = U
  name = G4_U
  specific = 4
FEATURE [App::DocumentObjectGroupPython] Np_element001  label="Np_element : 1"  # scripted group (container) (typed FeaturePython)
  n = 1
  ref = Np_element
FEATURE [App::DocumentObjectGroupPython] G4_Np  # scripted group (container) (typed FeaturePython)
  Dunit = g/cm3
  Dvalue = 20.25
  Group = -> [Np_element001]
  conduct = 2
  density = 1
  expand = 3
  formula = Np
  name = G4_Np
  specific = 4
FEATURE [App::DocumentObjectGroupPython] Pu_element002  label="Pu_element : 002"  # scripted group (container) (typed FeaturePython)
  n = 1
  ref = Pu_element
FEATURE [App::DocumentObjectGroupPython] G4_Pu  # scripted group (container) (typed FeaturePython)
  Dunit = g/cm3
  Dvalue = 19.84
  Group = -> [Pu_element002]
  conduct = 2
  density = 1
  expand = 3
  formula = Pu
  name = G4_Pu
  specific = 4
FEATURE [App::DocumentObjectGroupPython] Am_element001  label="Am_element : 1"  # scripted group (container) (typed FeaturePython)
  n = 1
  ref = Am_element
FEATURE [App::DocumentObjectGroupPython] G4_Am  # scripted group (container) (typed FeaturePython)
  Dunit = g/cm3
  Dvalue = 13.67
  Group = -> [Am_element001]
  conduct = 2
  density = 1
  expand = 3
  formula = Am
  name = G4_Am
  specific = 4
FEATURE [App::DocumentObjectGroupPython] Cm_element001  label="Cm_element : 1"  # scripted group (container) (typed FeaturePython)
  n = 1
  ref = Cm_element
FEATURE [App::DocumentObjectGroupPython] G4_Cm  # scripted group (container) (typed FeaturePython)
  Dunit = g/cm3
  Dvalue = 13.51
  Group = -> [Cm_element001]
  conduct = 2
  density = 1
  expand = 3
  formula = Cm
  name = G4_Cm
  specific = 4
FEATURE [App::DocumentObjectGroupPython] Bk_element001  label="Bk_element : 1"  # scripted group (container) (typed FeaturePython)
  n = 1
  ref = Bk_element
FEATURE [App::DocumentObjectGroupPython] G4_Bk  # scripted group (container) (typed FeaturePython)
  Dunit = g/cm3
  Dvalue = 14
  Group = -> [Bk_element001]
  conduct = 2
  density = 1
  expand = 3
  formula = Bk
  name = G4_Bk
  specific = 4
FEATURE [App::DocumentObjectGroupPython] Cf_element001  label="Cf_element : 1"  # scripted group (container) (typed FeaturePython)
  n = 1
  ref = Cf_element
FEATURE [App::DocumentObjectGroupPython] G4_Cf  # scripted group (container) (typed FeaturePython)
  Dunit = g/cm3
  Dvalue = 10
  Group = -> [Cf_element001]
  conduct = 2
  density = 1
  expand = 3
  formula = Cf
  name = G4_Cf
  specific = 4
FEATURE [App::DocumentObjectGroupPython] Element  # scripted group (container) (typed FeaturePython)
  Group = -> [G4_H,G4_He,G4_Li,G4_Be,G4_B,G4_C,G4_N,G4_O,G4_F,G4_Ne,G4_Na,G4_Mg,G4_Al,G4_Si,G4_P,G4_S,G4_Cl,G4_Ar,G4_K,G4_Ca,G4_Sc,G4_Ti,G4_V,G4_Cr,G4_Mn,G4_Fe,G4_Co,G4_Ni,G4_Cu,G4_Zn,G4_Ga,G4_Ge,G4_As,G4_Se,G4_Br,G4_Kr,G4_Rb,G4_Sr,G4_Y,G4_Zr,G4_Nb,G4_Mo,G4_Tc,G4_Ru,G4_Rh,G4_Pd,G4_Ag,G4_Cd,G4_In,G4_Sn,G4_Sb,G4_Te,G4_I,G4_Xe,G4_Cs,G4_Ba,G4_La,G4_Ce,G4_Pr,G4_Nd,G4_Pm,G4_Sm,G4_Eu,G4_Gd,G4_Tb,G4_Dy,G4_Ho,G4_Er,+30 more]
FEATURE [App::DocumentObjectGroupPython] H_element114  label="H_element : 063"  # scripted group (container) (typed FeaturePython)
  n = 2
  ref = H_element
FEATURE [App::DocumentObjectGroupPython] G4_lH2  # scripted group (container) (typed FeaturePython)
  Dunit = g/cm3
  Dvalue = 0.0708
  Group = -> [H_element114]
  conduct = 2
  density = 1
  expand = 3
  formula = G4_lH2
  name = G4_lH2
  specific = 4
FEATURE [App::DocumentObjectGroupPython] N_element049  label="N_element : 022"  # scripted group (container) (typed FeaturePython)
  n = 2
  ref = N_element
FEATURE [App::DocumentObjectGroupPython] G4_lN2  # scripted group (container) (typed FeaturePython)
  Dunit = g/cm3
  Dvalue = 0.807
  Group = -> [N_element049]
  conduct = 2
  density = 1
  expand = 3
  formula = G4_lN2
  name = G4_lN2
  specific = 4
FEATURE [App::DocumentObjectGroupPython] O_element106  label="O_element : 060"  # scripted group (container) (typed FeaturePython)
  n = 2
  ref = O_element
FEATURE [App::DocumentObjectGroupPython] G4_lO2  # scripted group (container) (typed FeaturePython)
  Dunit = g/cm3
  Dvalue = 1.141
  Group = -> [O_element106]
  conduct = 2
  density = 1
  expand = 3
  formula = G4_lO2
  name = G4_lO2
  specific = 4
FEATURE [App::DocumentObjectGroupPython] Ar_element003  label="Ar_element : 002"  # scripted group (container) (typed FeaturePython)
  n = 1
  ref = Ar_element
FEATURE [App::DocumentObjectGroupPython] G4_lAr  # scripted group (container) (typed FeaturePython)
  Dunit = g/cm3
  Dvalue = 1.396
  Group = -> [Ar_element003]
  conduct = 2
  density = 1
  expand = 3
  formula = G4_lAr
  name = G4_lAr
  specific = 4
FEATURE [App::DocumentObjectGroupPython] Br_element008  label="Br_element : 005"  # scripted group (container) (typed FeaturePython)
  n = 1
  ref = Br_element
FEATURE [App::DocumentObjectGroupPython] G4_lBr  # scripted group (container) (typed FeaturePython)
  Dunit = g/cm3
  Dvalue = 3.1028
  Group = -> [Br_element008]
  conduct = 2
  density = 1
  expand = 3
  formula = G4_lBr
  name = G4_lBr
  specific = 4
FEATURE [App::DocumentObjectGroupPython] Kr_element002  label="Kr_element : 002"  # scripted group (container) (typed FeaturePython)
  n = 1
  ref = Kr_element
FEATURE [App::DocumentObjectGroupPython] G4_lKr  # scripted group (container) (typed FeaturePython)
  Dunit = g/cm3
  Dvalue = 2.418
  Group = -> [Kr_element002]
  conduct = 2
  density = 1
  expand = 3
  formula = G4_lKr
  name = G4_lKr
  specific = 4
FEATURE [App::DocumentObjectGroupPython] Xe_element002  label="Xe_element : 002"  # scripted group (container) (typed FeaturePython)
  n = 1
  ref = Xe_element
FEATURE [App::DocumentObjectGroupPython] G4_lXe  # scripted group (container) (typed FeaturePython)
  Dunit = g/cm3
  Dvalue = 2.953
  Group = -> [Xe_element002]
  conduct = 2
  density = 1
  expand = 3
  formula = G4_lXe
  name = G4_lXe
  specific = 4
FEATURE [App::DocumentObjectGroupPython] O_element107  label="O_element : 061"  # scripted group (container) (typed FeaturePython)
  n = 4
  ref = O_element
FEATURE [App::DocumentObjectGroupPython] Pb_element004  label="Pb_element : 002"  # scripted group (container) (typed FeaturePython)
  n = 1
  ref = Pb_element
FEATURE [App::DocumentObjectGroupPython] W_element005  label="W_element : 005"  # scripted group (container) (typed FeaturePython)
  n = 1
  ref = W_element
FEATURE [App::DocumentObjectGroupPython] G4_PbWO4  # scripted group (container) (typed FeaturePython)
  Dunit = g/cm3
  Dvalue = 8.28
  Group = -> [O_element107,Pb_element004,W_element005]
  conduct = 2
  density = 1
  expand = 3
  formula = G4_PbWO4
  name = G4_PbWO4
  specific = 4
FEATURE [App::DocumentObjectGroupPython] H_element115  label="H_element : 064"  # scripted group (container) (typed FeaturePython)
  n = 1
  ref = H_element
FEATURE [App::DocumentObjectGroupPython] G4_Galactic  # scripted group (container) (typed FeaturePython)
  Dunit = g/cm3
  Dvalue = 0
  Group = -> [H_element115]
  conduct = 2
  density = 1
  expand = 3
  formula = G4_Galactic
  name = G4_Galactic
  specific = 4
FEATURE [App::DocumentObjectGroupPython] C_element125  label="C_element : 071"  # scripted group (container) (typed FeaturePython)
  n = 1
  ref = C_element
FEATURE [App::DocumentObjectGroupPython] G4_GRAPHITE_POROUS  # scripted group (container) (typed FeaturePython)
  Dunit = g/cm3
  Dvalue = 1.7
  Group = -> [C_element125]
  conduct = 2
  density = 1
  expand = 3
  formula = G4_GRAPHITE_POROUS
  name = G4_GRAPHITE_POROUS
  specific = 4
FEATURE [App::DocumentObjectGroupPython] H_element116  label="H_element : 0.150"  # scripted group (container) (typed FeaturePython)
  n = 0.080538
FEATURE [App::DocumentObjectGroupPython] C_element126  label="C_element : 0.600"  # scripted group (container) (typed FeaturePython)
  n = 0.599848
FEATURE [App::DocumentObjectGroupPython] O_element108  label="O_element : 0.320"  # scripted group (container) (typed FeaturePython)
  n = 0.319614
FEATURE [App::DocumentObjectGroupPython] G4_LUCITE  # scripted group (container) (typed FeaturePython)
  Dunit = g/cm3
  Dvalue = 1.19
  Group = -> [H_element116,C_element126,O_element108]
  conduct = 2
  density = 1
  expand = 3
  formula = G4_LUCITE
  name = G4_LUCITE
  specific = 4
FEATURE [App::DocumentObjectGroupPython] Cu_element002  label="Cu_element : 62"  # scripted group (container) (typed FeaturePython)
  n = 62
  ref = Cu_element
FEATURE [App::DocumentObjectGroupPython] Zn_element002  label="Zn_element : 35"  # scripted group (container) (typed FeaturePython)
  n = 35
  ref = Zn_element
FEATURE [App::DocumentObjectGroupPython] Pb_element005  label="Pb_element : 3"  # scripted group (container) (typed FeaturePython)
  n = 3
  ref = Pb_element
FEATURE [App::DocumentObjectGroupPython] G4_BRASS  # scripted group (container) (typed FeaturePython)
  Dunit = g/cm3
  Dvalue = 8.52
  Group = -> [Cu_element002,Zn_element002,Pb_element005]
  conduct = 2
  density = 1
  expand = 3
  formula = G4_BRASS
  name = G4_BRASS
  specific = 4
FEATURE [App::DocumentObjectGroupPython] Cu_element003  label="Cu_element : 89"  # scripted group (container) (typed FeaturePython)
  n = 89
  ref = Cu_element
FEATURE [App::DocumentObjectGroupPython] Zn_element003  label="Zn_element : 9"  # scripted group (container) (typed FeaturePython)
  n = 9
  ref = Zn_element
FEATURE [App::DocumentObjectGroupPython] Pb_element006  label="Pb_element : 2"  # scripted group (container) (typed FeaturePython)
  n = 2
  ref = Pb_element
FEATURE [App::DocumentObjectGroupPython] G4_BRONZE  # scripted group (container) (typed FeaturePython)
  Dunit = g/cm3
  Dvalue = 8.82
  Group = -> [Cu_element003,Zn_element003,Pb_element006]
  conduct = 2
  density = 1
  expand = 3
  formula = G4_BRONZE
  name = G4_BRONZE
  specific = 4
FEATURE [App::DocumentObjectGroupPython] Fe_element008  label="Fe_element : 74"  # scripted group (container) (typed FeaturePython)
  n = 74
  ref = Fe_element
FEATURE [App::DocumentObjectGroupPython] Cr_element002  label="Cr_element : 18"  # scripted group (container) (typed FeaturePython)
  n = 18
  ref = Cr_element
FEATURE [App::DocumentObjectGroupPython] Ni_element002  label="Ni_element : 8"  # scripted group (container) (typed FeaturePython)
  n = 8
  ref = Ni_element
FEATURE [App::DocumentObjectGroupPython] G4_STAINLESS_STEEL  label="G4_STAINLESS-STEEL"  # scripted group (container) (typed FeaturePython)
  Dunit = g/cm3
  Dvalue = 8
  Group = -> [Fe_element008,Cr_element002,Ni_element002]
  conduct = 2
  density = 1
  expand = 3
  formula = G4_STAINLESS-STEEL
  name = G4_STAINLESS-STEEL
  specific = 4
FEATURE [App::DocumentObjectGroupPython] H_element117  label="H_element : 065"  # scripted group (container) (typed FeaturePython)
  n = 18
  ref = H_element
FEATURE [App::DocumentObjectGroupPython] C_element127  label="C_element : 072"  # scripted group (container) (typed FeaturePython)
  n = 12
  ref = C_element
FEATURE [App::DocumentObjectGroupPython] O_element109  label="O_element : 062"  # scripted group (container) (typed FeaturePython)
  n = 7
  ref = O_element
FEATURE [App::DocumentObjectGroupPython] G4_CR39  # scripted group (container) (typed FeaturePython)
  Dunit = g/cm3
  Dvalue = 1.32
  Group = -> [H_element117,C_element127,O_element109]
  conduct = 2
  density = 1
  expand = 3
  formula = G4_CR39
  name = G4_CR39
  specific = 4
FEATURE [App::DocumentObjectGroupPython] H_element118  label="H_element : 38"  # scripted group (container) (typed FeaturePython)
  n = 38
  ref = H_element
FEATURE [App::DocumentObjectGroupPython] C_element128  label="C_element : 073"  # scripted group (container) (typed FeaturePython)
  n = 18
  ref = C_element
FEATURE [App::DocumentObjectGroupPython] O_element110  label="O_element : 063"  # scripted group (container) (typed FeaturePython)
  n = 1
  ref = O_element
FEATURE [App::DocumentObjectGroupPython] G4_OCTADECANOL  # scripted group (container) (typed FeaturePython)
  Dunit = g/cm3
  Dvalue = 0.812
  Group = -> [H_element118,C_element128,O_element110]
  conduct = 2
  density = 1
  expand = 3
  formula = G4_OCTADECANOL
  name = G4_OCTADECANOL
  specific = 4
FEATURE [App::DocumentObjectGroupPython] HEP  # scripted group (container) (typed FeaturePython)
  Group = -> [G4_lH2,G4_lN2,G4_lO2,G4_lAr,G4_lBr,G4_lKr,G4_lXe,G4_PbWO4,G4_Galactic,G4_GRAPHITE_POROUS,G4_LUCITE,G4_BRASS,G4_BRONZE,G4_STAINLESS_STEEL,G4_CR39,G4_OCTADECANOL]
FEATURE [App::DocumentObjectGroupPython] C_element129  label="C_element : 074"  # scripted group (container) (typed FeaturePython)
  n = 14
  ref = C_element
FEATURE [App::DocumentObjectGroupPython] H_element119  label="H_element : 066"  # scripted group (container) (typed FeaturePython)
  n = 10
  ref = H_element
FEATURE [App::DocumentObjectGroupPython] O_element111  label="O_element : 064"  # scripted group (container) (typed FeaturePython)
  n = 2
  ref = O_element
FEATURE [App::DocumentObjectGroupPython] N_element050  label="N_element : 023"  # scripted group (container) (typed FeaturePython)
  n = 2
  ref = N_element
FEATURE [App::DocumentObjectGroupPython] G4_KEVLAR  # scripted group (container) (typed FeaturePython)
  Dunit = g/cm3
  Dvalue = 1.44
  Group = -> [C_element129,H_element119,O_element111,N_element050]
  conduct = 2
  density = 1
  expand = 3
  formula = G4_KEVLAR
  name = G4_KEVLAR
  specific = 4
FEATURE [App::DocumentObjectGroupPython] C_element130  label="C_element : 075"  # scripted group (container) (typed FeaturePython)
  n = 10
  ref = C_element
FEATURE [App::DocumentObjectGroupPython] H_element120  label="H_element : 067"  # scripted group (container) (typed FeaturePython)
  n = 8
  ref = H_element
FEATURE [App::DocumentObjectGroupPython] O_element112  label="O_element : 065"  # scripted group (container) (typed FeaturePython)
  n = 4
  ref = O_element
FEATURE [App::DocumentObjectGroupPython] G4_DACRON  # scripted group (container) (typed FeaturePython)
  Dunit = g/cm3
  Dvalue = 1.4
  Group = -> [C_element130,H_element120,O_element112]
  conduct = 2
  density = 1
  expand = 3
  formula = G4_DACRON
  name = G4_DACRON
  specific = 4
FEATURE [App::DocumentObjectGroupPython] C_element131  label="C_element : 076"  # scripted group (container) (typed FeaturePython)
  n = 4
  ref = C_element
FEATURE [App::DocumentObjectGroupPython] H_element121  label="H_element : 068"  # scripted group (container) (typed FeaturePython)
  n = 5
  ref = H_element
FEATURE [App::DocumentObjectGroupPython] Cl_element030  label="Cl_element : 016"  # scripted group (container) (typed FeaturePython)
  n = 1
  ref = Cl_element
FEATURE [App::DocumentObjectGroupPython] G4_NEOPRENE  # scripted group (container) (typed FeaturePython)
  Dunit = g/cm3
  Dvalue = 1.23
  Group = -> [C_element131,H_element121,Cl_element030]
  conduct = 2
  density = 1
  expand = 3
  formula = G4_NEOPRENE
  name = G4_NEOPRENE
  specific = 4
FEATURE [App::DocumentObjectGroupPython] Space  # scripted group (container) (typed FeaturePython)
  Group = -> [G4_KEVLAR,G4_DACRON,G4_NEOPRENE]
FEATURE [App::DocumentObjectGroupPython] H_element122  label="H_element : 069"  # scripted group (container) (typed FeaturePython)
  n = 5
  ref = H_element
FEATURE [App::DocumentObjectGroupPython] C_element132  label="C_element : 077"  # scripted group (container) (typed FeaturePython)
  n = 4
  ref = C_element
FEATURE [App::DocumentObjectGroupPython] N_element051  label="N_element : 3"  # scripted group (container) (typed FeaturePython)
  n = 3
  ref = N_element
FEATURE [App::DocumentObjectGroupPython] O_element113  label="O_element : 066"  # scripted group (container) (typed FeaturePython)
  n = 1
  ref = O_element
FEATURE [App::DocumentObjectGroupPython] G4_CYTOSINE  # scripted group (container) (typed FeaturePython)
  Dunit = g/cm3
  Dvalue = 1.55
  Group = -> [H_element122,C_element132,N_element051,O_element113]
  conduct = 2
  density = 1
  expand = 3
  formula = G4_CYTOSINE
  name = G4_CYTOSINE
  specific = 4
FEATURE [App::DocumentObjectGroupPython] H_element123  label="H_element : 070"  # scripted group (container) (typed FeaturePython)
  n = 6
  ref = H_element
FEATURE [App::DocumentObjectGroupPython] C_element133  label="C_element : 078"  # scripted group (container) (typed FeaturePython)
  n = 5
  ref = C_element
FEATURE [App::DocumentObjectGroupPython] N_element052  label="N_element : 024"  # scripted group (container) (typed FeaturePython)
  n = 2
  ref = N_element
FEATURE [App::DocumentObjectGroupPython] O_element114  label="O_element : 067"  # scripted group (container) (typed FeaturePython)
  n = 2
  ref = O_element
FEATURE [App::DocumentObjectGroupPython] G4_THYMINE  # scripted group (container) (typed FeaturePython)
  Dunit = g/cm3
  Dvalue = 1.23
  Group = -> [H_element123,C_element133,N_element052,O_element114]
  conduct = 2
  density = 1
  expand = 3
  formula = G4_THYMINE
  name = G4_THYMINE
  specific = 4
FEATURE [App::DocumentObjectGroupPython] H_element124  label="H_element : 071"  # scripted group (container) (typed FeaturePython)
  n = 4
  ref = H_element
FEATURE [App::DocumentObjectGroupPython] C_element134  label="C_element : 079"  # scripted group (container) (typed FeaturePython)
  n = 4
  ref = C_element
FEATURE [App::DocumentObjectGroupPython] N_element053  label="N_element : 025"  # scripted group (container) (typed FeaturePython)
  n = 2
  ref = N_element
FEATURE [App::DocumentObjectGroupPython] O_element115  label="O_element : 068"  # scripted group (container) (typed FeaturePython)
  n = 2
  ref = O_element
FEATURE [App::DocumentObjectGroupPython] G4_URACIL  # scripted group (container) (typed FeaturePython)
  Dunit = g/cm3
  Dvalue = 1.32
  Group = -> [H_element124,C_element134,N_element053,O_element115]
  conduct = 2
  density = 1
  expand = 3
  formula = G4_URACIL
  name = G4_URACIL
  specific = 4
FEATURE [App::DocumentObjectGroupPython] H_element125  label="H_element : 072"  # scripted group (container) (typed FeaturePython)
  n = 4
  ref = H_element
FEATURE [App::DocumentObjectGroupPython] C_element135  label="C_element : 080"  # scripted group (container) (typed FeaturePython)
  n = 5
  ref = C_element
FEATURE [App::DocumentObjectGroupPython] N_element054  label="N_element : 026"  # scripted group (container) (typed FeaturePython)
  n = 5
  ref = N_element
FEATURE [App::DocumentObjectGroupPython] G4_DNA_ADENINE  # scripted group (container) (typed FeaturePython)
  Dunit = g/cm3
  Dvalue = 1
  Group = -> [H_element125,C_element135,N_element054]
  conduct = 2
  density = 1
  expand = 3
  formula = G4_DNA_ADENINE
  name = G4_DNA_ADENINE
  specific = 4
FEATURE [App::DocumentObjectGroupPython] H_element126  label="H_element : 073"  # scripted group (container) (typed FeaturePython)
  n = 4
  ref = H_element
FEATURE [App::DocumentObjectGroupPython] C_element136  label="C_element : 081"  # scripted group (container) (typed FeaturePython)
  n = 5
  ref = C_element
FEATURE [App::DocumentObjectGroupPython] N_element055  label="N_element : 027"  # scripted group (container) (typed FeaturePython)
  n = 5
  ref = N_element
FEATURE [App::DocumentObjectGroupPython] O_element116  label="O_element : 069"  # scripted group (container) (typed FeaturePython)
  n = 1
  ref = O_element
FEATURE [App::DocumentObjectGroupPython] G4_DNA_GUANINE  # scripted group (container) (typed FeaturePython)
  Dunit = g/cm3
  Dvalue = 1
  Group = -> [H_element126,C_element136,N_element055,O_element116]
  conduct = 2
  density = 1
  expand = 3
  formula = G4_DNA_GUANINE
  name = G4_DNA_GUANINE
  specific = 4
FEATURE [App::DocumentObjectGroupPython] H_element127  label="H_element : 074"  # scripted group (container) (typed FeaturePython)
  n = 4
  ref = H_element
FEATURE [App::DocumentObjectGroupPython] C_element137  label="C_element : 082"  # scripted group (container) (typed FeaturePython)
  n = 4
  ref = C_element
FEATURE [App::DocumentObjectGroupPython] N_element056  label="N_element : 028"  # scripted group (container) (typed FeaturePython)
  n = 3
  ref = N_element
FEATURE [App::DocumentObjectGroupPython] O_element117  label="O_element : 070"  # scripted group (container) (typed FeaturePython)
  n = 1
  ref = O_element
FEATURE [App::DocumentObjectGroupPython] G4_DNA_CYTOSINE  # scripted group (container) (typed FeaturePython)
  Dunit = g/cm3
  Dvalue = 1
  Group = -> [H_element127,C_element137,N_element056,O_element117]
  conduct = 2
  density = 1
  expand = 3
  formula = G4_DNA_CYTOSINE
  name = G4_DNA_CYTOSINE
  specific = 4
FEATURE [App::DocumentObjectGroupPython] H_element128  label="H_element : 075"  # scripted group (container) (typed FeaturePython)
  n = 5
  ref = H_element
FEATURE [App::DocumentObjectGroupPython] C_element138  label="C_element : 083"  # scripted group (container) (typed FeaturePython)
  n = 5
  ref = C_element
FEATURE [App::DocumentObjectGroupPython] N_element057  label="N_element : 029"  # scripted group (container) (typed FeaturePython)
  n = 2
  ref = N_element
FEATURE [App::DocumentObjectGroupPython] O_element118  label="O_element : 071"  # scripted group (container) (typed FeaturePython)
  n = 2
  ref = O_element
FEATURE [App::DocumentObjectGroupPython] G4_DNA_THYMINE  # scripted group (container) (typed FeaturePython)
  Dunit = g/cm3
  Dvalue = 1
  Group = -> [H_element128,C_element138,N_element057,O_element118]
  conduct = 2
  density = 1
  expand = 3
  formula = G4_DNA_THYMINE
  name = G4_DNA_THYMINE
  specific = 4
FEATURE [App::DocumentObjectGroupPython] H_element129  label="H_element : 076"  # scripted group (container) (typed FeaturePython)
  n = 3
  ref = H_element
FEATURE [App::DocumentObjectGroupPython] C_element139  label="C_element : 084"  # scripted group (container) (typed FeaturePython)
  n = 4
  ref = C_element
FEATURE [App::DocumentObjectGroupPython] N_element058  label="N_element : 030"  # scripted group (container) (typed FeaturePython)
  n = 2
  ref = N_element
FEATURE [App::DocumentObjectGroupPython] O_element119  label="O_element : 072"  # scripted group (container) (typed FeaturePython)
  n = 2
  ref = O_element
FEATURE [App::DocumentObjectGroupPython] G4_DNA_URACIL  # scripted group (container) (typed FeaturePython)
  Dunit = g/cm3
  Dvalue = 1
  Group = -> [H_element129,C_element139,N_element058,O_element119]
  conduct = 2
  density = 1
  expand = 3
  formula = G4_DNA_URACIL
  name = G4_DNA_URACIL
  specific = 4
FEATURE [App::DocumentObjectGroupPython] H_element130  label="H_element : 077"  # scripted group (container) (typed FeaturePython)
  n = 10
  ref = H_element
FEATURE [App::DocumentObjectGroupPython] C_element140  label="C_element : 085"  # scripted group (container) (typed FeaturePython)
  n = 10
  ref = C_element
FEATURE [App::DocumentObjectGroupPython] N_element059  label="N_element : 031"  # scripted group (container) (typed FeaturePython)
  n = 5
  ref = N_element
FEATURE [App::DocumentObjectGroupPython] O_element120  label="O_element : 073"  # scripted group (container) (typed FeaturePython)
  n = 4
  ref = O_element
FEATURE [App::DocumentObjectGroupPython] G4_DNA_ADENOSINE  # scripted group (container) (typed FeaturePython)
  Dunit = g/cm3
  Dvalue = 1
  Group = -> [H_element130,C_element140,N_element059,O_element120]
  conduct = 2
  density = 1
  expand = 3
  formula = G4_DNA_ADENOSINE
  name = G4_DNA_ADENOSINE
  specific = 4
FEATURE [App::DocumentObjectGroupPython] H_element131  label="H_element : 078"  # scripted group (container) (typed FeaturePython)
  n = 10
  ref = H_element
FEATURE [App::DocumentObjectGroupPython] C_element141  label="C_element : 086"  # scripted group (container) (typed FeaturePython)
  n = 10
  ref = C_element
FEATURE [App::DocumentObjectGroupPython] N_element060  label="N_element : 032"  # scripted group (container) (typed FeaturePython)
  n = 5
  ref = N_element
FEATURE [App::DocumentObjectGroupPython] O_element121  label="O_element : 074"  # scripted group (container) (typed FeaturePython)
  n = 5
  ref = O_element
FEATURE [App::DocumentObjectGroupPython] G4_DNA_GUANOSINE  # scripted group (container) (typed FeaturePython)
  Dunit = g/cm3
  Dvalue = 1
  Group = -> [H_element131,C_element141,N_element060,O_element121]
  conduct = 2
  density = 1
  expand = 3
  formula = G4_DNA_GUANOSINE
  name = G4_DNA_GUANOSINE
  specific = 4
FEATURE [App::DocumentObjectGroupPython] H_element132  label="H_element : 079"  # scripted group (container) (typed FeaturePython)
  n = 10
  ref = H_element
FEATURE [App::DocumentObjectGroupPython] C_element142  label="C_element : 087"  # scripted group (container) (typed FeaturePython)
  n = 9
  ref = C_element
FEATURE [App::DocumentObjectGroupPython] N_element061  label="N_element : 033"  # scripted group (container) (typed FeaturePython)
  n = 3
  ref = N_element
FEATURE [App::DocumentObjectGroupPython] O_element122  label="O_element : 075"  # scripted group (container) (typed FeaturePython)
  n = 5
  ref = O_element
FEATURE [App::DocumentObjectGroupPython] G4_DNA_CYTIDINE  # scripted group (container) (typed FeaturePython)
  Dunit = g/cm3
  Dvalue = 1
  Group = -> [H_element132,C_element142,N_element061,O_element122]
  conduct = 2
  density = 1
  expand = 3
  formula = G4_DNA_CYTIDINE
  name = G4_DNA_CYTIDINE
  specific = 4
FEATURE [App::DocumentObjectGroupPython] H_element133  label="H_element : 080"  # scripted group (container) (typed FeaturePython)
  n = 9
  ref = H_element
FEATURE [App::DocumentObjectGroupPython] C_element143  label="C_element : 088"  # scripted group (container) (typed FeaturePython)
  n = 9
  ref = C_element
FEATURE [App::DocumentObjectGroupPython] N_element062  label="N_element : 034"  # scripted group (container) (typed FeaturePython)
  n = 2
  ref = N_element
FEATURE [App::DocumentObjectGroupPython] O_element123  label="O_element : 076"  # scripted group (container) (typed FeaturePython)
  n = 6
  ref = O_element
FEATURE [App::DocumentObjectGroupPython] G4_DNA_URIDINE  # scripted group (container) (typed FeaturePython)
  Dunit = g/cm3
  Dvalue = 1
  Group = -> [H_element133,C_element143,N_element062,O_element123]
  conduct = 2
  density = 1
  expand = 3
  formula = G4_DNA_URIDINE
  name = G4_DNA_URIDINE
  specific = 4
FEATURE [App::DocumentObjectGroupPython] H_element134  label="H_element : 081"  # scripted group (container) (typed FeaturePython)
  n = 11
  ref = H_element
FEATURE [App::DocumentObjectGroupPython] C_element144  label="C_element : 089"  # scripted group (container) (typed FeaturePython)
  n = 10
  ref = C_element
FEATURE [App::DocumentObjectGroupPython] N_element063  label="N_element : 035"  # scripted group (container) (typed FeaturePython)
  n = 2
  ref = N_element
FEATURE [App::DocumentObjectGroupPython] O_element124  label="O_element : 077"  # scripted group (container) (typed FeaturePython)
  n = 6
  ref = O_element
FEATURE [App::DocumentObjectGroupPython] G4_DNA_METHYLURIDINE  # scripted group (container) (typed FeaturePython)
  Dunit = g/cm3
  Dvalue = 1
  Group = -> [H_element134,C_element144,N_element063,O_element124]
  conduct = 2
  density = 1
  expand = 3
  formula = G4_DNA_METHYLURIDINE
  name = G4_DNA_METHYLURIDINE
  specific = 4
FEATURE [App::DocumentObjectGroupPython] P_element014  label="P_element : 003"  # scripted group (container) (typed FeaturePython)
  n = 1
  ref = P_element
FEATURE [App::DocumentObjectGroupPython] O_element125  label="O_element : 078"  # scripted group (container) (typed FeaturePython)
  n = 3
  ref = O_element
FEATURE [App::DocumentObjectGroupPython] G4_DNA_MONOPHOSPHATE  # scripted group (container) (typed FeaturePython)
  Dunit = g/cm3
  Dvalue = 1
  Group = -> [P_element014,O_element125]
  conduct = 2
  density = 1
  expand = 3
  formula = G4_DNA_MONOPHOSPHATE
  name = G4_DNA_MONOPHOSPHATE
  specific = 4
FEATURE [App::DocumentObjectGroupPython] H_element135  label="H_element : 082"  # scripted group (container) (typed FeaturePython)
  n = 10
  ref = H_element
FEATURE [App::DocumentObjectGroupPython] C_element145  label="C_element : 090"  # scripted group (container) (typed FeaturePython)
  n = 10
  ref = C_element
FEATURE [App::DocumentObjectGroupPython] N_element064  label="N_element : 036"  # scripted group (container) (typed FeaturePython)
  n = 5
  ref = N_element
FEATURE [App::DocumentObjectGroupPython] O_element126  label="O_element : 079"  # scripted group (container) (typed FeaturePython)
  n = 7
  ref = O_element
FEATURE [App::DocumentObjectGroupPython] P_element015  label="P_element : 004"  # scripted group (container) (typed FeaturePython)
  n = 1
  ref = P_element
FEATURE [App::DocumentObjectGroupPython] G4_DNA_A  # scripted group (container) (typed FeaturePython)
  Dunit = g/cm3
  Dvalue = 1
  Group = -> [H_element135,C_element145,N_element064,O_element126,P_element015]
  conduct = 2
  density = 1
  expand = 3
  formula = G4_DNA_A
  name = G4_DNA_A
  specific = 4
FEATURE [App::DocumentObjectGroupPython] H_element136  label="H_element : 083"  # scripted group (container) (typed FeaturePython)
  n = 10
  ref = H_element
FEATURE [App::DocumentObjectGroupPython] C_element146  label="C_element : 091"  # scripted group (container) (typed FeaturePython)
  n = 10
  ref = C_element
FEATURE [App::DocumentObjectGroupPython] N_element065  label="N_element : 037"  # scripted group (container) (typed FeaturePython)
  n = 5
  ref = N_element
FEATURE [App::DocumentObjectGroupPython] O_element127  label="O_element : 8"  # scripted group (container) (typed FeaturePython)
  n = 8
  ref = O_element
FEATURE [App::DocumentObjectGroupPython] P_element016  label="P_element : 005"  # scripted group (container) (typed FeaturePython)
  n = 1
  ref = P_element
FEATURE [App::DocumentObjectGroupPython] G4_DNA_G  # scripted group (container) (typed FeaturePython)
  Dunit = g/cm3
  Dvalue = 1
  Group = -> [H_element136,C_element146,N_element065,O_element127,P_element016]
  conduct = 2
  density = 1
  expand = 3
  formula = G4_DNA_G
  name = G4_DNA_G
  specific = 4
FEATURE [App::DocumentObjectGroupPython] H_element137  label="H_element : 084"  # scripted group (container) (typed FeaturePython)
  n = 10
  ref = H_element
FEATURE [App::DocumentObjectGroupPython] C_element147  label="C_element : 092"  # scripted group (container) (typed FeaturePython)
  n = 9
  ref = C_element
FEATURE [App::DocumentObjectGroupPython] N_element066  label="N_element : 038"  # scripted group (container) (typed FeaturePython)
  n = 3
  ref = N_element
FEATURE [App::DocumentObjectGroupPython] O_element128  label="O_element : 080"  # scripted group (container) (typed FeaturePython)
  n = 8
  ref = O_element
FEATURE [App::DocumentObjectGroupPython] P_element017  label="P_element : 006"  # scripted group (container) (typed FeaturePython)
  n = 1
  ref = P_element
FEATURE [App::DocumentObjectGroupPython] G4_DNA_C  # scripted group (container) (typed FeaturePython)
  Dunit = g/cm3
  Dvalue = 1
  Group = -> [H_element137,C_element147,N_element066,O_element128,P_element017]
  conduct = 2
  density = 1
  expand = 3
  formula = G4_DNA_C
  name = G4_DNA_C
  specific = 4
FEATURE [App::DocumentObjectGroupPython] H_element138  label="H_element : 085"  # scripted group (container) (typed FeaturePython)
  n = 9
  ref = H_element
FEATURE [App::DocumentObjectGroupPython] C_element148  label="C_element : 093"  # scripted group (container) (typed FeaturePython)
  n = 9
  ref = C_element
FEATURE [App::DocumentObjectGroupPython] N_element067  label="N_element : 039"  # scripted group (container) (typed FeaturePython)
  n = 2
  ref = N_element
FEATURE [App::DocumentObjectGroupPython] O_element129  label="O_element : 9"  # scripted group (container) (typed FeaturePython)
  n = 9
  ref = O_element
FEATURE [App::DocumentObjectGroupPython] P_element018  label="P_element : 007"  # scripted group (container) (typed FeaturePython)
  n = 1
  ref = P_element
FEATURE [App::DocumentObjectGroupPython] G4_DNA_U  # scripted group (container) (typed FeaturePython)
  Dunit = g/cm3
  Dvalue = 1
  Group = -> [H_element138,C_element148,N_element067,O_element129,P_element018]
  conduct = 2
  density = 1
  expand = 3
  formula = G4_DNA_U
  name = G4_DNA_U
  specific = 4
FEATURE [App::DocumentObjectGroupPython] H_element139  label="H_element : 086"  # scripted group (container) (typed FeaturePython)
  n = 11
  ref = H_element
FEATURE [App::DocumentObjectGroupPython] C_element149  label="C_element : 094"  # scripted group (container) (typed FeaturePython)
  n = 10
  ref = C_element
FEATURE [App::DocumentObjectGroupPython] N_element068  label="N_element : 040"  # scripted group (container) (typed FeaturePython)
  n = 2
  ref = N_element
FEATURE [App::DocumentObjectGroupPython] O_element130  label="O_element : 081"  # scripted group (container) (typed FeaturePython)
  n = 9
  ref = O_element
FEATURE [App::DocumentObjectGroupPython] P_element019  label="P_element : 008"  # scripted group (container) (typed FeaturePython)
  n = 1
  ref = P_element
FEATURE [App::DocumentObjectGroupPython] G4_DNA_MU  # scripted group (container) (typed FeaturePython)
  Dunit = g/cm3
  Dvalue = 1
  Group = -> [H_element139,C_element149,N_element068,O_element130,P_element019]
  conduct = 2
  density = 1
  expand = 3
  formula = G4_DNA_MU
  name = G4_DNA_MU
  specific = 4
FEATURE [App::DocumentObjectGroupPython] BioChemical  # scripted group (container) (typed FeaturePython)
  Group = -> [G4_CYTOSINE,G4_THYMINE,G4_URACIL,G4_DNA_ADENINE,G4_DNA_GUANINE,G4_DNA_CYTOSINE,G4_DNA_THYMINE,G4_DNA_URACIL,G4_DNA_ADENOSINE,G4_DNA_GUANOSINE,G4_DNA_CYTIDINE,G4_DNA_URIDINE,G4_DNA_METHYLURIDINE,G4_DNA_MONOPHOSPHATE,G4_DNA_A,G4_DNA_G,G4_DNA_C,G4_DNA_U,G4_DNA_MU]
FEATURE [App::DocumentObjectGroupPython] G4Materials  # scripted group (container) (typed FeaturePython)
  Group = -> [NIST,Element,HEP,Space,BioChemical]
  version = 1
FEATURE [App::DocumentObjectGroupPython] Geant4  # scripted group (container) (typed FeaturePython)
  Group = -> [G4Isotopes,G4Elements,G4Materials]
FEATURE [App::DocumentObjectGroupPython] Materials  # scripted group (container) (typed FeaturePython)
  Group = -> [Geant4]
FEATURE [Part::FeaturePython] GDMLBox_WorldBox  # WARN: FeaturePython — macro-defined, semantics opaque (R4)
  lunit = 2
  material = 5
  x = 260.26
  y = 182
  z = 169
FEATURE [Part::FeaturePython] GDMLBox_Box  # WARN: FeaturePython — macro-defined, semantics opaque (R4)
  Placement = pos=(30,0,0) rot=(0,0,1;0rad)
  lunit = 2
  material = 0
  x = 10
  y = 10
  z = 10
FEATURE [Part::FeaturePython] GDMLTorus  # WARN: FeaturePython — macro-defined, semantics opaque (R4)
  Placement = pos=(30,0,0) rot=(0,1,0;1.5708rad)
  aunit = deg
  deltaphi = 360
  lunit = 2
  material = 0
  rmax = 2
  rmin = 0
  rtor = 8
  startphi = 0
FEATURE [Part::MultiFuse] Fusion
  Placement = pos=(0,-25,0) rot=(0,0,1;0.523599rad)
  Shapes = -> [GDMLBox_Box,GDMLTorus]
FEATURE [Part::FeaturePython] Array  # Draft array (typed FeaturePython)
  AlwaysSyncPlacement = false
  Angle = 180
  ArrayType = 1
  Axis = (0,0,1)
  Base = -> Fusion
  Center = (0,0,0)
  Count = 5
  ExpandArray = false
  Fuse = false
  IntervalAxis = (0,0,0)
  IntervalX = (50,0,0)
  IntervalY = (0,50,0)
  IntervalZ = (0,0,50)
  NumberCircles = 3
  NumberPolar = 5
  NumberX = 2
  NumberY = 2
  NumberZ = 1
  Placement = pos=(42,35,0) rot=(0,0,1;0.785398rad)
  PlacementList = 5 placements: [(0,-25,0),(17.6777,-17.6777,0),(25,-5.55112e-15,0),(17.6777,17.6777,0),(3.06162e-15,25,0)]
  RadialDistance = 50
  ScaleList = (5) [(1,1,1),(1,1,1),(1,1,1),(1,1,1),(1,1,1)]
  Symmetry = 1
  TangentialDistance = 25
FEATURE [App::Part] Part001
  Group = -> [Array]
  Origin = -> Origin004
FEATURE [App::Part] worldVOL
  Group = -> [GDMLBox_WorldBox,Part001]
  Origin = -> Origin
